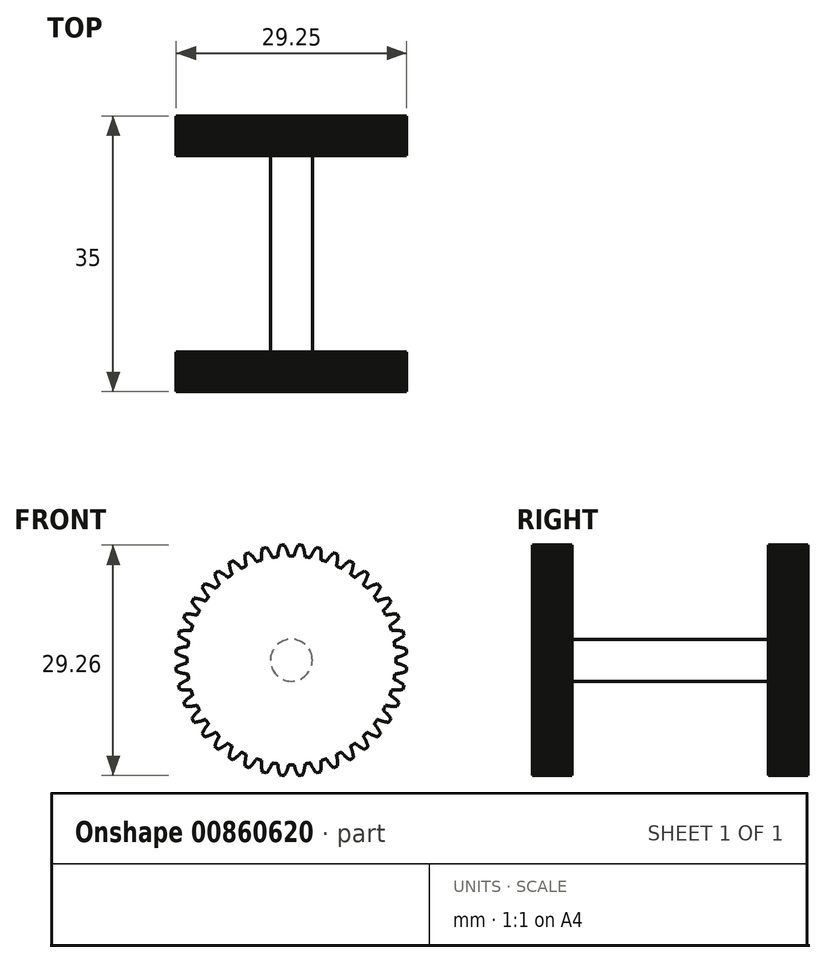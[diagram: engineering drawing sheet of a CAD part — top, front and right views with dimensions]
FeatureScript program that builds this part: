
annotation { "Feature Type Name" : "Feature", "Feature Type Description" : "" }
export const myFeature = defineFeature(function(context is Context, id is Id, definition is map)
    precondition{}
    {
        {
            var Q0;
            Q0=qCreatedBy(makeId("Front.planeOp"),FACE);
            var sketch = newSketch(context, id + "F0", { "sketchPlane" : qUnion([Q0])});
            skLineSegment(sketch, "E0", {"start": v(-13.67, 1.41) * mm, "end": v(-13.71, 1.13) * mm});
            skLineSegment(sketch, "E1", {"start": v(-13.71, 1.13) * mm, "end": v(-13.71, 0.85) * mm});
            skLineSegment(sketch, "E2", {"start": v(-13.71, 0.85) * mm, "end": v(-13.66, 0.82) * mm});
            skLineSegment(sketch, "E3", {"start": v(-13.66, 0.82) * mm, "end": v(-13.57, 0.77) * mm});
            skLineSegment(sketch, "E4", {"start": v(-13.57, 0.77) * mm, "end": v(-13.5, 0.73) * mm});
            skLineSegment(sketch, "E5", {"start": v(-13.5, 0.73) * mm, "end": v(-13.41, 0.7) * mm});
            skLineSegment(sketch, "E6", {"start": v(-13.41, 0.7) * mm, "end": v(-13.33, 0.65) * mm});
            skLineSegment(sketch, "E7", {"start": v(-13.33, 0.65) * mm, "end": v(-13.26, 0.62) * mm});
            skLineSegment(sketch, "E8", {"start": v(-13.26, 0.62) * mm, "end": v(-13.19, 0.59) * mm});
            skLineSegment(sketch, "E9", {"start": v(-13.19, 0.59) * mm, "end": v(-13.12, 0.56) * mm});
            skLineSegment(sketch, "E10", {"start": v(-13.12, 0.56) * mm, "end": v(-13.05, 0.53) * mm});
            skLineSegment(sketch, "E11", {"start": v(-13.05, 0.53) * mm, "end": v(-12.98, 0.5) * mm});
            skLineSegment(sketch, "E12", {"start": v(-12.98, 0.5) * mm, "end": v(-12.92, 0.49) * mm});
            skLineSegment(sketch, "E13", {"start": v(-12.92, 0.49) * mm, "end": v(-12.86, 0.47) * mm});
            skLineSegment(sketch, "E14", {"start": v(-12.86, 0.47) * mm, "end": v(-12.8, 0.45) * mm});
            skLineSegment(sketch, "E15", {"start": v(-12.8, 0.45) * mm, "end": v(-12.75, 0.43) * mm});
            skLineSegment(sketch, "E16", {"start": v(-12.75, 0.43) * mm, "end": v(-12.7, 0.42) * mm});
            skLineSegment(sketch, "E17", {"start": v(-12.7, 0.42) * mm, "end": v(-12.65, 0.4) * mm});
            skLineSegment(sketch, "E18", {"start": v(-12.65, 0.4) * mm, "end": v(-12.6, 0.4) * mm});
            skLineSegment(sketch, "E19", {"start": v(-12.6, 0.4) * mm, "end": v(-12.57, 0.38) * mm});
            skLineSegment(sketch, "E20", {"start": v(-12.57, 0.38) * mm, "end": v(-12.53, 0.37) * mm});
            skLineSegment(sketch, "E21", {"start": v(-12.53, 0.37) * mm, "end": v(-12.5, 0.37) * mm});
            skLineSegment(sketch, "E22", {"start": v(-12.5, 0.37) * mm, "end": v(-12.48, 0.36) * mm});
            skLineSegment(sketch, "E23", {"start": v(-12.48, 0.36) * mm, "end": v(-12.45, 0.35) * mm});
            skLineSegment(sketch, "E24", {"start": v(-12.45, 0.35) * mm, "end": v(-12.42, 0.34) * mm});
            skLineSegment(sketch, "E25", {"start": v(-12.42, 0.34) * mm, "end": v(-12.4, 0.33) * mm});
            skLineSegment(sketch, "E26", {"start": v(-12.4, 0.33) * mm, "end": v(-12.38, 0.32) * mm});
            skLineSegment(sketch, "E27", {"start": v(-12.38, 0.32) * mm, "end": v(-12.37, 0.31) * mm});
            skLineSegment(sketch, "E28", {"start": v(-12.37, 0.31) * mm, "end": v(-12.36, 0.3) * mm});
            skLineSegment(sketch, "E29", {"start": v(-12.36, 0.3) * mm, "end": v(-12.35, 0.3) * mm});
            skLineSegment(sketch, "E30", {"start": v(-12.35, 0.3) * mm, "end": v(-12.35, 0.28) * mm});
            skLineSegment(sketch, "E31", {"start": v(-12.35, 0.28) * mm, "end": v(-12.35, 0.08) * mm});
            skLineSegment(sketch, "E32", {"start": v(-12.35, 0.08) * mm, "end": v(-12.35, -0.12) * mm});
            skLineSegment(sketch, "E33", {"start": v(-12.35, -0.12) * mm, "end": v(-12.35, -0.32) * mm});
            skLineSegment(sketch, "E34", {"start": v(-12.35, -0.32) * mm, "end": v(-12.35, -0.33) * mm});
            skLineSegment(sketch, "E35", {"start": v(-12.35, -0.33) * mm, "end": v(-12.36, -0.34) * mm});
            skLineSegment(sketch, "E36", {"start": v(-12.36, -0.34) * mm, "end": v(-12.37, -0.35) * mm});
            skLineSegment(sketch, "E37", {"start": v(-12.37, -0.35) * mm, "end": v(-12.38, -0.36) * mm});
            skLineSegment(sketch, "E38", {"start": v(-12.38, -0.36) * mm, "end": v(-12.4, -0.37) * mm});
            skLineSegment(sketch, "E39", {"start": v(-12.4, -0.37) * mm, "end": v(-12.42, -0.38) * mm});
            skLineSegment(sketch, "E40", {"start": v(-12.42, -0.38) * mm, "end": v(-12.45, -0.4) * mm});
            skLineSegment(sketch, "E41", {"start": v(-12.45, -0.4) * mm, "end": v(-12.48, -0.4) * mm});
            skLineSegment(sketch, "E42", {"start": v(-12.48, -0.4) * mm, "end": v(-12.5, -0.4) * mm});
            skLineSegment(sketch, "E43", {"start": v(-12.5, -0.4) * mm, "end": v(-12.53, -0.41) * mm});
            skLineSegment(sketch, "E44", {"start": v(-12.53, -0.41) * mm, "end": v(-12.57, -0.42) * mm});
            skLineSegment(sketch, "E45", {"start": v(-12.57, -0.42) * mm, "end": v(-12.6, -0.43) * mm});
            skLineSegment(sketch, "E46", {"start": v(-12.6, -0.43) * mm, "end": v(-12.65, -0.44) * mm});
            skLineSegment(sketch, "E47", {"start": v(-12.65, -0.44) * mm, "end": v(-12.7, -0.46) * mm});
            skLineSegment(sketch, "E48", {"start": v(-12.7, -0.46) * mm, "end": v(-12.75, -0.47) * mm});
            skLineSegment(sketch, "E49", {"start": v(-12.75, -0.47) * mm, "end": v(-12.8, -0.49) * mm});
            skLineSegment(sketch, "E50", {"start": v(-12.8, -0.49) * mm, "end": v(-12.86, -0.5) * mm});
            skLineSegment(sketch, "E51", {"start": v(-12.86, -0.5) * mm, "end": v(-12.92, -0.53) * mm});
            skLineSegment(sketch, "E52", {"start": v(-12.92, -0.53) * mm, "end": v(-12.98, -0.55) * mm});
            skLineSegment(sketch, "E53", {"start": v(-12.98, -0.55) * mm, "end": v(-13.05, -0.57) * mm});
            skLineSegment(sketch, "E54", {"start": v(-13.05, -0.57) * mm, "end": v(-13.12, -0.6) * mm});
            skLineSegment(sketch, "E55", {"start": v(-13.12, -0.6) * mm, "end": v(-13.19, -0.63) * mm});
            skLineSegment(sketch, "E56", {"start": v(-13.19, -0.63) * mm, "end": v(-13.26, -0.66) * mm});
            skLineSegment(sketch, "E57", {"start": v(-13.26, -0.66) * mm, "end": v(-13.33, -0.7) * mm});
            skLineSegment(sketch, "E58", {"start": v(-13.33, -0.7) * mm, "end": v(-13.41, -0.73) * mm});
            skLineSegment(sketch, "E59", {"start": v(-13.41, -0.73) * mm, "end": v(-13.5, -0.77) * mm});
            skLineSegment(sketch, "E60", {"start": v(-13.5, -0.77) * mm, "end": v(-13.57, -0.81) * mm});
            skLineSegment(sketch, "E61", {"start": v(-13.57, -0.81) * mm, "end": v(-13.66, -0.86) * mm});
            skLineSegment(sketch, "E62", {"start": v(-13.66, -0.86) * mm, "end": v(-13.71, -0.89) * mm});
            skLineSegment(sketch, "E63", {"start": v(-13.71, -0.89) * mm, "end": v(-13.71, -1.17) * mm});
            skLineSegment(sketch, "E64", {"start": v(-13.71, -1.17) * mm, "end": v(-13.67, -1.45) * mm});
            skLineSegment(sketch, "E65", {"start": v(-13.67, -1.45) * mm, "end": v(-13.6, -1.47) * mm});
            skLineSegment(sketch, "E66", {"start": v(-13.6, -1.47) * mm, "end": v(-13.52, -1.5) * mm});
            skLineSegment(sketch, "E67", {"start": v(-13.52, -1.5) * mm, "end": v(-13.43, -1.53) * mm});
            skLineSegment(sketch, "E68", {"start": v(-13.43, -1.53) * mm, "end": v(-13.35, -1.56) * mm});
            skLineSegment(sketch, "E69", {"start": v(-13.35, -1.56) * mm, "end": v(-13.26, -1.58) * mm});
            skLineSegment(sketch, "E70", {"start": v(-13.26, -1.58) * mm, "end": v(-13.18, -1.6) * mm});
            skLineSegment(sketch, "E71", {"start": v(-13.18, -1.6) * mm, "end": v(-13.1, -1.62) * mm});
            skLineSegment(sketch, "E72", {"start": v(-13.1, -1.62) * mm, "end": v(-13.03, -1.64) * mm});
            skLineSegment(sketch, "E73", {"start": v(-13.03, -1.64) * mm, "end": v(-12.96, -1.66) * mm});
            skLineSegment(sketch, "E74", {"start": v(-12.96, -1.66) * mm, "end": v(-12.9, -1.67) * mm});
            skLineSegment(sketch, "E75", {"start": v(-12.9, -1.67) * mm, "end": v(-12.83, -1.68) * mm});
            skLineSegment(sketch, "E76", {"start": v(-12.83, -1.68) * mm, "end": v(-12.77, -1.7) * mm});
            skLineSegment(sketch, "E77", {"start": v(-12.77, -1.7) * mm, "end": v(-12.7, -1.7) * mm});
            skLineSegment(sketch, "E78", {"start": v(-12.7, -1.7) * mm, "end": v(-12.65, -1.71) * mm});
            skLineSegment(sketch, "E79", {"start": v(-12.65, -1.71) * mm, "end": v(-12.6, -1.72) * mm});
            skLineSegment(sketch, "E80", {"start": v(-12.6, -1.72) * mm, "end": v(-12.55, -1.72) * mm});
            skLineSegment(sketch, "E81", {"start": v(-12.55, -1.72) * mm, "end": v(-12.5, -1.73) * mm});
            skLineSegment(sketch, "E82", {"start": v(-12.5, -1.73) * mm, "end": v(-12.46, -1.73) * mm});
            skLineSegment(sketch, "E83", {"start": v(-12.46, -1.73) * mm, "end": v(-12.42, -1.73) * mm});
            skLineSegment(sketch, "E84", {"start": v(-12.42, -1.73) * mm, "end": v(-12.4, -1.74) * mm});
            skLineSegment(sketch, "E85", {"start": v(-12.4, -1.74) * mm, "end": v(-12.37, -1.74) * mm});
            skLineSegment(sketch, "E86", {"start": v(-12.37, -1.74) * mm, "end": v(-12.34, -1.74) * mm});
            skLineSegment(sketch, "E87", {"start": v(-12.34, -1.74) * mm, "end": v(-12.32, -1.75) * mm});
            skLineSegment(sketch, "E88", {"start": v(-12.32, -1.75) * mm, "end": v(-12.3, -1.75) * mm});
            skLineSegment(sketch, "E89", {"start": v(-12.3, -1.75) * mm, "end": v(-12.27, -1.76) * mm});
            skLineSegment(sketch, "E90", {"start": v(-12.27, -1.76) * mm, "end": v(-12.26, -1.77) * mm});
            skLineSegment(sketch, "E91", {"start": v(-12.26, -1.77) * mm, "end": v(-12.25, -1.78) * mm});
            skLineSegment(sketch, "E92", {"start": v(-12.25, -1.78) * mm, "end": v(-12.24, -1.79) * mm});
            skLineSegment(sketch, "E93", {"start": v(-12.24, -1.79) * mm, "end": v(-12.23, -1.8) * mm});
            skLineSegment(sketch, "E94", {"start": v(-12.23, -1.8) * mm, "end": v(-12.2, -2) * mm});
            skLineSegment(sketch, "E95", {"start": v(-12.2, -2) * mm, "end": v(-12.17, -2.2) * mm});
            skLineSegment(sketch, "E96", {"start": v(-12.17, -2.2) * mm, "end": v(-12.14, -2.4) * mm});
            skLineSegment(sketch, "E97", {"start": v(-12.14, -2.4) * mm, "end": v(-12.14, -2.4) * mm});
            skLineSegment(sketch, "E98", {"start": v(-12.14, -2.4) * mm, "end": v(-12.15, -2.41) * mm});
            skLineSegment(sketch, "E99", {"start": v(-12.15, -2.41) * mm, "end": v(-12.15, -2.43) * mm});
            skLineSegment(sketch, "E100", {"start": v(-12.15, -2.43) * mm, "end": v(-12.17, -2.44) * mm});
            skLineSegment(sketch, "E101", {"start": v(-12.17, -2.44) * mm, "end": v(-12.18, -2.45) * mm});
            skLineSegment(sketch, "E102", {"start": v(-12.18, -2.45) * mm, "end": v(-12.2, -2.47) * mm});
            skLineSegment(sketch, "E103", {"start": v(-12.2, -2.47) * mm, "end": v(-12.22, -2.48) * mm});
            skLineSegment(sketch, "E104", {"start": v(-12.22, -2.48) * mm, "end": v(-12.25, -2.5) * mm});
            skLineSegment(sketch, "E105", {"start": v(-12.25, -2.5) * mm, "end": v(-12.28, -2.5) * mm});
            skLineSegment(sketch, "E106", {"start": v(-12.28, -2.5) * mm, "end": v(-12.3, -2.5) * mm});
            skLineSegment(sketch, "E107", {"start": v(-12.3, -2.5) * mm, "end": v(-12.34, -2.52) * mm});
            skLineSegment(sketch, "E108", {"start": v(-12.34, -2.52) * mm, "end": v(-12.38, -2.54) * mm});
            skLineSegment(sketch, "E109", {"start": v(-12.38, -2.54) * mm, "end": v(-12.42, -2.56) * mm});
            skLineSegment(sketch, "E110", {"start": v(-12.42, -2.56) * mm, "end": v(-12.46, -2.58) * mm});
            skLineSegment(sketch, "E111", {"start": v(-12.46, -2.58) * mm, "end": v(-12.51, -2.6) * mm});
            skLineSegment(sketch, "E112", {"start": v(-12.51, -2.6) * mm, "end": v(-12.56, -2.63) * mm});
            skLineSegment(sketch, "E113", {"start": v(-12.56, -2.63) * mm, "end": v(-12.62, -2.65) * mm});
            skLineSegment(sketch, "E114", {"start": v(-12.62, -2.65) * mm, "end": v(-12.67, -2.68) * mm});
            skLineSegment(sketch, "E115", {"start": v(-12.67, -2.68) * mm, "end": v(-12.73, -2.72) * mm});
            skLineSegment(sketch, "E116", {"start": v(-12.73, -2.72) * mm, "end": v(-12.79, -2.75) * mm});
            skLineSegment(sketch, "E117", {"start": v(-12.79, -2.75) * mm, "end": v(-12.85, -2.79) * mm});
            skLineSegment(sketch, "E118", {"start": v(-12.85, -2.79) * mm, "end": v(-12.92, -2.83) * mm});
            skLineSegment(sketch, "E119", {"start": v(-12.92, -2.83) * mm, "end": v(-12.98, -2.87) * mm});
            skLineSegment(sketch, "E120", {"start": v(-12.98, -2.87) * mm, "end": v(-13.05, -2.91) * mm});
            skLineSegment(sketch, "E121", {"start": v(-13.05, -2.91) * mm, "end": v(-13.12, -2.96) * mm});
            skLineSegment(sketch, "E122", {"start": v(-13.12, -2.96) * mm, "end": v(-13.2, -3.01) * mm});
            skLineSegment(sketch, "E123", {"start": v(-13.2, -3.01) * mm, "end": v(-13.27, -3.07) * mm});
            skLineSegment(sketch, "E124", {"start": v(-13.27, -3.07) * mm, "end": v(-13.35, -3.12) * mm});
            skLineSegment(sketch, "E125", {"start": v(-13.35, -3.12) * mm, "end": v(-13.4, -3.16) * mm});
            skLineSegment(sketch, "E126", {"start": v(-13.4, -3.16) * mm, "end": v(-13.35, -3.45) * mm});
            skLineSegment(sketch, "E127", {"start": v(-13.35, -3.45) * mm, "end": v(-13.27, -3.72) * mm});
            skLineSegment(sketch, "E128", {"start": v(-13.27, -3.72) * mm, "end": v(-13.2, -3.73) * mm});
            skLineSegment(sketch, "E129", {"start": v(-13.2, -3.73) * mm, "end": v(-13.1, -3.74) * mm});
            skLineSegment(sketch, "E130", {"start": v(-13.1, -3.74) * mm, "end": v(-13.02, -3.76) * mm});
            skLineSegment(sketch, "E131", {"start": v(-13.02, -3.76) * mm, "end": v(-12.93, -3.77) * mm});
            skLineSegment(sketch, "E132", {"start": v(-12.93, -3.77) * mm, "end": v(-12.84, -3.78) * mm});
            skLineSegment(sketch, "E133", {"start": v(-12.84, -3.78) * mm, "end": v(-12.76, -3.8) * mm});
            skLineSegment(sketch, "E134", {"start": v(-12.76, -3.8) * mm, "end": v(-12.68, -3.8) * mm});
            skLineSegment(sketch, "E135", {"start": v(-12.68, -3.8) * mm, "end": v(-12.6, -3.8) * mm});
            skLineSegment(sketch, "E136", {"start": v(-12.6, -3.8) * mm, "end": v(-12.54, -3.8) * mm});
            skLineSegment(sketch, "E137", {"start": v(-12.54, -3.8) * mm, "end": v(-12.47, -3.81) * mm});
            skLineSegment(sketch, "E138", {"start": v(-12.47, -3.81) * mm, "end": v(-12.4, -3.81) * mm});
            skLineSegment(sketch, "E139", {"start": v(-12.4, -3.81) * mm, "end": v(-12.34, -3.81) * mm});
            skLineSegment(sketch, "E140", {"start": v(-12.34, -3.81) * mm, "end": v(-12.28, -3.81) * mm});
            skLineSegment(sketch, "E141", {"start": v(-12.28, -3.81) * mm, "end": v(-12.22, -3.81) * mm});
            skLineSegment(sketch, "E142", {"start": v(-12.22, -3.81) * mm, "end": v(-12.17, -3.81) * mm});
            skLineSegment(sketch, "E143", {"start": v(-12.17, -3.81) * mm, "end": v(-12.12, -3.8) * mm});
            skLineSegment(sketch, "E144", {"start": v(-12.12, -3.8) * mm, "end": v(-12.07, -3.8) * mm});
            skLineSegment(sketch, "E145", {"start": v(-12.07, -3.8) * mm, "end": v(-12.03, -3.8) * mm});
            skLineSegment(sketch, "E146", {"start": v(-12.03, -3.8) * mm, "end": v(-11.99, -3.8) * mm});
            skLineSegment(sketch, "E147", {"start": v(-11.99, -3.8) * mm, "end": v(-11.97, -3.8) * mm});
            skLineSegment(sketch, "E148", {"start": v(-11.97, -3.8) * mm, "end": v(-11.94, -3.8) * mm});
            skLineSegment(sketch, "E149", {"start": v(-11.94, -3.8) * mm, "end": v(-11.9, -3.8) * mm});
            skLineSegment(sketch, "E150", {"start": v(-11.9, -3.8) * mm, "end": v(-11.88, -3.8) * mm});
            skLineSegment(sketch, "E151", {"start": v(-11.88, -3.8) * mm, "end": v(-11.86, -3.8) * mm});
            skLineSegment(sketch, "E152", {"start": v(-11.86, -3.8) * mm, "end": v(-11.84, -3.8) * mm});
            skLineSegment(sketch, "E153", {"start": v(-11.84, -3.8) * mm, "end": v(-11.82, -3.8) * mm});
            skLineSegment(sketch, "E154", {"start": v(-11.82, -3.8) * mm, "end": v(-11.8, -3.81) * mm});
            skLineSegment(sketch, "E155", {"start": v(-11.8, -3.81) * mm, "end": v(-11.8, -3.82) * mm});
            skLineSegment(sketch, "E156", {"start": v(-11.8, -3.82) * mm, "end": v(-11.8, -3.83) * mm});
            skLineSegment(sketch, "E157", {"start": v(-11.8, -3.83) * mm, "end": v(-11.74, -4.02) * mm});
            skLineSegment(sketch, "E158", {"start": v(-11.74, -4.02) * mm, "end": v(-11.67, -4.22) * mm});
            skLineSegment(sketch, "E159", {"start": v(-11.67, -4.22) * mm, "end": v(-11.6, -4.4) * mm});
            skLineSegment(sketch, "E160", {"start": v(-11.6, -4.4) * mm, "end": v(-11.6, -4.42) * mm});
            skLineSegment(sketch, "E161", {"start": v(-11.6, -4.42) * mm, "end": v(-11.61, -4.43) * mm});
            skLineSegment(sketch, "E162", {"start": v(-11.61, -4.43) * mm, "end": v(-11.62, -4.44) * mm});
            skLineSegment(sketch, "E163", {"start": v(-11.62, -4.44) * mm, "end": v(-11.63, -4.46) * mm});
            skLineSegment(sketch, "E164", {"start": v(-11.63, -4.46) * mm, "end": v(-11.64, -4.47) * mm});
            skLineSegment(sketch, "E165", {"start": v(-11.64, -4.47) * mm, "end": v(-11.66, -4.49) * mm});
            skLineSegment(sketch, "E166", {"start": v(-11.66, -4.49) * mm, "end": v(-11.68, -4.5) * mm});
            skLineSegment(sketch, "E167", {"start": v(-11.68, -4.5) * mm, "end": v(-11.7, -4.52) * mm});
            skLineSegment(sketch, "E168", {"start": v(-11.7, -4.52) * mm, "end": v(-11.73, -4.54) * mm});
            skLineSegment(sketch, "E169", {"start": v(-11.73, -4.54) * mm, "end": v(-11.75, -4.55) * mm});
            skLineSegment(sketch, "E170", {"start": v(-11.75, -4.55) * mm, "end": v(-11.78, -4.57) * mm});
            skLineSegment(sketch, "E171", {"start": v(-11.78, -4.57) * mm, "end": v(-11.82, -4.59) * mm});
            skLineSegment(sketch, "E172", {"start": v(-11.82, -4.59) * mm, "end": v(-11.86, -4.61) * mm});
            skLineSegment(sketch, "E173", {"start": v(-11.86, -4.61) * mm, "end": v(-11.9, -4.64) * mm});
            skLineSegment(sketch, "E174", {"start": v(-11.9, -4.64) * mm, "end": v(-11.94, -4.67) * mm});
            skLineSegment(sketch, "E175", {"start": v(-11.94, -4.67) * mm, "end": v(-11.99, -4.7) * mm});
            skLineSegment(sketch, "E176", {"start": v(-11.99, -4.7) * mm, "end": v(-12.04, -4.74) * mm});
            skLineSegment(sketch, "E177", {"start": v(-12.04, -4.74) * mm, "end": v(-12.09, -4.78) * mm});
            skLineSegment(sketch, "E178", {"start": v(-12.09, -4.78) * mm, "end": v(-12.14, -4.82) * mm});
            skLineSegment(sketch, "E179", {"start": v(-12.14, -4.82) * mm, "end": v(-12.2, -4.86) * mm});
            skLineSegment(sketch, "E180", {"start": v(-12.2, -4.86) * mm, "end": v(-12.25, -4.9) * mm});
            skLineSegment(sketch, "E181", {"start": v(-12.25, -4.9) * mm, "end": v(-12.3, -4.96) * mm});
            skLineSegment(sketch, "E182", {"start": v(-12.3, -4.96) * mm, "end": v(-12.37, -5) * mm});
            skLineSegment(sketch, "E183", {"start": v(-12.37, -5) * mm, "end": v(-12.43, -5.06) * mm});
            skLineSegment(sketch, "E184", {"start": v(-12.43, -5.06) * mm, "end": v(-12.5, -5.12) * mm});
            skLineSegment(sketch, "E185", {"start": v(-12.5, -5.12) * mm, "end": v(-12.55, -5.18) * mm});
            skLineSegment(sketch, "E186", {"start": v(-12.55, -5.18) * mm, "end": v(-12.62, -5.25) * mm});
            skLineSegment(sketch, "E187", {"start": v(-12.62, -5.25) * mm, "end": v(-12.69, -5.32) * mm});
            skLineSegment(sketch, "E188", {"start": v(-12.69, -5.32) * mm, "end": v(-12.73, -5.36) * mm});
            skLineSegment(sketch, "E189", {"start": v(-12.73, -5.36) * mm, "end": v(-12.64, -5.63) * mm});
            skLineSegment(sketch, "E190", {"start": v(-12.64, -5.63) * mm, "end": v(-12.51, -5.89) * mm});
            skLineSegment(sketch, "E191", {"start": v(-12.51, -5.89) * mm, "end": v(-12.45, -5.9) * mm});
            skLineSegment(sketch, "E192", {"start": v(-12.45, -5.9) * mm, "end": v(-12.35, -5.9) * mm});
            skLineSegment(sketch, "E193", {"start": v(-12.35, -5.9) * mm, "end": v(-12.26, -5.9) * mm});
            skLineSegment(sketch, "E194", {"start": v(-12.26, -5.9) * mm, "end": v(-12.17, -5.9) * mm});
            skLineSegment(sketch, "E195", {"start": v(-12.17, -5.9) * mm, "end": v(-12.09, -5.89) * mm});
            skLineSegment(sketch, "E196", {"start": v(-12.09, -5.89) * mm, "end": v(-12, -5.88) * mm});
            skLineSegment(sketch, "E197", {"start": v(-12, -5.88) * mm, "end": v(-11.93, -5.88) * mm});
            skLineSegment(sketch, "E198", {"start": v(-11.93, -5.88) * mm, "end": v(-11.85, -5.87) * mm});
            skLineSegment(sketch, "E199", {"start": v(-11.85, -5.87) * mm, "end": v(-11.78, -5.87) * mm});
            skLineSegment(sketch, "E200", {"start": v(-11.78, -5.87) * mm, "end": v(-11.7, -5.86) * mm});
            skLineSegment(sketch, "E201", {"start": v(-11.7, -5.86) * mm, "end": v(-11.64, -5.85) * mm});
            skLineSegment(sketch, "E202", {"start": v(-11.64, -5.85) * mm, "end": v(-11.58, -5.84) * mm});
            skLineSegment(sketch, "E203", {"start": v(-11.58, -5.84) * mm, "end": v(-11.52, -5.83) * mm});
            skLineSegment(sketch, "E204", {"start": v(-11.52, -5.83) * mm, "end": v(-11.47, -5.82) * mm});
            skLineSegment(sketch, "E205", {"start": v(-11.47, -5.82) * mm, "end": v(-11.41, -5.81) * mm});
            skLineSegment(sketch, "E206", {"start": v(-11.41, -5.81) * mm, "end": v(-11.37, -5.8) * mm});
            skLineSegment(sketch, "E207", {"start": v(-11.37, -5.8) * mm, "end": v(-11.32, -5.8) * mm});
            skLineSegment(sketch, "E208", {"start": v(-11.32, -5.8) * mm, "end": v(-11.28, -5.78) * mm});
            skLineSegment(sketch, "E209", {"start": v(-11.28, -5.78) * mm, "end": v(-11.24, -5.77) * mm});
            skLineSegment(sketch, "E210", {"start": v(-11.24, -5.77) * mm, "end": v(-11.22, -5.77) * mm});
            skLineSegment(sketch, "E211", {"start": v(-11.22, -5.77) * mm, "end": v(-11.19, -5.76) * mm});
            skLineSegment(sketch, "E212", {"start": v(-11.19, -5.76) * mm, "end": v(-11.16, -5.75) * mm});
            skLineSegment(sketch, "E213", {"start": v(-11.16, -5.75) * mm, "end": v(-11.13, -5.75) * mm});
            skLineSegment(sketch, "E214", {"start": v(-11.13, -5.75) * mm, "end": v(-11.11, -5.75) * mm});
            skLineSegment(sketch, "E215", {"start": v(-11.11, -5.75) * mm, "end": v(-11.1, -5.75) * mm});
            skLineSegment(sketch, "E216", {"start": v(-11.1, -5.75) * mm, "end": v(-11.07, -5.75) * mm});
            skLineSegment(sketch, "E217", {"start": v(-11.07, -5.75) * mm, "end": v(-11.06, -5.76) * mm});
            skLineSegment(sketch, "E218", {"start": v(-11.06, -5.76) * mm, "end": v(-11.05, -5.77) * mm});
            skLineSegment(sketch, "E219", {"start": v(-11.05, -5.77) * mm, "end": v(-11.04, -5.77) * mm});
            skLineSegment(sketch, "E220", {"start": v(-11.04, -5.77) * mm, "end": v(-10.95, -5.95) * mm});
            skLineSegment(sketch, "E221", {"start": v(-10.95, -5.95) * mm, "end": v(-10.86, -6.14) * mm});
            skLineSegment(sketch, "E222", {"start": v(-10.86, -6.14) * mm, "end": v(-10.77, -6.3) * mm});
            skLineSegment(sketch, "E223", {"start": v(-10.77, -6.3) * mm, "end": v(-10.77, -6.32) * mm});
            skLineSegment(sketch, "E224", {"start": v(-10.77, -6.32) * mm, "end": v(-10.77, -6.33) * mm});
            skLineSegment(sketch, "E225", {"start": v(-10.77, -6.33) * mm, "end": v(-10.77, -6.35) * mm});
            skLineSegment(sketch, "E226", {"start": v(-10.77, -6.35) * mm, "end": v(-10.78, -6.36) * mm});
            skLineSegment(sketch, "E227", {"start": v(-10.78, -6.36) * mm, "end": v(-10.79, -6.38) * mm});
            skLineSegment(sketch, "E228", {"start": v(-10.79, -6.38) * mm, "end": v(-10.8, -6.4) * mm});
            skLineSegment(sketch, "E229", {"start": v(-10.8, -6.4) * mm, "end": v(-10.82, -6.42) * mm});
            skLineSegment(sketch, "E230", {"start": v(-10.82, -6.42) * mm, "end": v(-10.84, -6.44) * mm});
            skLineSegment(sketch, "E231", {"start": v(-10.84, -6.44) * mm, "end": v(-10.87, -6.46) * mm});
            skLineSegment(sketch, "E232", {"start": v(-10.87, -6.46) * mm, "end": v(-10.88, -6.47) * mm});
            skLineSegment(sketch, "E233", {"start": v(-10.88, -6.47) * mm, "end": v(-10.91, -6.5) * mm});
            skLineSegment(sketch, "E234", {"start": v(-10.91, -6.5) * mm, "end": v(-10.95, -6.52) * mm});
            skLineSegment(sketch, "E235", {"start": v(-10.95, -6.52) * mm, "end": v(-10.98, -6.56) * mm});
            skLineSegment(sketch, "E236", {"start": v(-10.98, -6.56) * mm, "end": v(-11.02, -6.59) * mm});
            skLineSegment(sketch, "E237", {"start": v(-11.02, -6.59) * mm, "end": v(-11.06, -6.63) * mm});
            skLineSegment(sketch, "E238", {"start": v(-11.06, -6.63) * mm, "end": v(-11.1, -6.66) * mm});
            skLineSegment(sketch, "E239", {"start": v(-11.1, -6.66) * mm, "end": v(-11.14, -6.7) * mm});
            skLineSegment(sketch, "E240", {"start": v(-11.14, -6.7) * mm, "end": v(-11.18, -6.75) * mm});
            skLineSegment(sketch, "E241", {"start": v(-11.18, -6.75) * mm, "end": v(-11.23, -6.8) * mm});
            skLineSegment(sketch, "E242", {"start": v(-11.23, -6.8) * mm, "end": v(-11.28, -6.85) * mm});
            skLineSegment(sketch, "E243", {"start": v(-11.28, -6.85) * mm, "end": v(-11.32, -6.9) * mm});
            skLineSegment(sketch, "E244", {"start": v(-11.32, -6.9) * mm, "end": v(-11.37, -6.96) * mm});
            skLineSegment(sketch, "E245", {"start": v(-11.37, -6.96) * mm, "end": v(-11.42, -7.02) * mm});
            skLineSegment(sketch, "E246", {"start": v(-11.42, -7.02) * mm, "end": v(-11.47, -7.09) * mm});
            skLineSegment(sketch, "E247", {"start": v(-11.47, -7.09) * mm, "end": v(-11.53, -7.16) * mm});
            skLineSegment(sketch, "E248", {"start": v(-11.53, -7.16) * mm, "end": v(-11.58, -7.23) * mm});
            skLineSegment(sketch, "E249", {"start": v(-11.58, -7.23) * mm, "end": v(-11.63, -7.3) * mm});
            skLineSegment(sketch, "E250", {"start": v(-11.63, -7.3) * mm, "end": v(-11.69, -7.38) * mm});
            skLineSegment(sketch, "E251", {"start": v(-11.69, -7.38) * mm, "end": v(-11.73, -7.43) * mm});
            skLineSegment(sketch, "E252", {"start": v(-11.73, -7.43) * mm, "end": v(-11.6, -7.69) * mm});
            skLineSegment(sketch, "E253", {"start": v(-11.6, -7.69) * mm, "end": v(-11.43, -7.92) * mm});
            skLineSegment(sketch, "E254", {"start": v(-11.43, -7.92) * mm, "end": v(-11.37, -7.9) * mm});
            skLineSegment(sketch, "E255", {"start": v(-11.37, -7.9) * mm, "end": v(-11.27, -7.9) * mm});
            skLineSegment(sketch, "E256", {"start": v(-11.27, -7.9) * mm, "end": v(-11.18, -7.88) * mm});
            skLineSegment(sketch, "E257", {"start": v(-11.18, -7.88) * mm, "end": v(-11.1, -7.87) * mm});
            skLineSegment(sketch, "E258", {"start": v(-11.1, -7.87) * mm, "end": v(-11, -7.85) * mm});
            skLineSegment(sketch, "E259", {"start": v(-11, -7.85) * mm, "end": v(-10.93, -7.83) * mm});
            skLineSegment(sketch, "E260", {"start": v(-10.93, -7.83) * mm, "end": v(-10.85, -7.82) * mm});
            skLineSegment(sketch, "E261", {"start": v(-10.85, -7.82) * mm, "end": v(-10.78, -7.8) * mm});
            skLineSegment(sketch, "E262", {"start": v(-10.78, -7.8) * mm, "end": v(-10.7, -7.78) * mm});
            skLineSegment(sketch, "E263", {"start": v(-10.7, -7.78) * mm, "end": v(-10.64, -7.76) * mm});
            skLineSegment(sketch, "E264", {"start": v(-10.64, -7.76) * mm, "end": v(-10.58, -7.74) * mm});
            skLineSegment(sketch, "E265", {"start": v(-10.58, -7.74) * mm, "end": v(-10.52, -7.72) * mm});
            skLineSegment(sketch, "E266", {"start": v(-10.52, -7.72) * mm, "end": v(-10.46, -7.7) * mm});
            skLineSegment(sketch, "E267", {"start": v(-10.46, -7.7) * mm, "end": v(-10.4, -7.69) * mm});
            skLineSegment(sketch, "E268", {"start": v(-10.4, -7.69) * mm, "end": v(-10.36, -7.67) * mm});
            skLineSegment(sketch, "E269", {"start": v(-10.36, -7.67) * mm, "end": v(-10.31, -7.65) * mm});
            skLineSegment(sketch, "E270", {"start": v(-10.31, -7.65) * mm, "end": v(-10.27, -7.63) * mm});
            skLineSegment(sketch, "E271", {"start": v(-10.27, -7.63) * mm, "end": v(-10.23, -7.62) * mm});
            skLineSegment(sketch, "E272", {"start": v(-10.23, -7.62) * mm, "end": v(-10.2, -7.6) * mm});
            skLineSegment(sketch, "E273", {"start": v(-10.2, -7.6) * mm, "end": v(-10.17, -7.6) * mm});
            skLineSegment(sketch, "E274", {"start": v(-10.17, -7.6) * mm, "end": v(-10.14, -7.58) * mm});
            skLineSegment(sketch, "E275", {"start": v(-10.14, -7.58) * mm, "end": v(-10.11, -7.57) * mm});
            skLineSegment(sketch, "E276", {"start": v(-10.11, -7.57) * mm, "end": v(-10.09, -7.56) * mm});
            skLineSegment(sketch, "E277", {"start": v(-10.09, -7.56) * mm, "end": v(-10.07, -7.56) * mm});
            skLineSegment(sketch, "E278", {"start": v(-10.07, -7.56) * mm, "end": v(-10.05, -7.56) * mm});
            skLineSegment(sketch, "E279", {"start": v(-10.05, -7.56) * mm, "end": v(-10.03, -7.56) * mm});
            skLineSegment(sketch, "E280", {"start": v(-10.03, -7.56) * mm, "end": v(-10.01, -7.56) * mm});
            skLineSegment(sketch, "E281", {"start": v(-10.01, -7.56) * mm, "end": v(-10, -7.57) * mm});
            skLineSegment(sketch, "E282", {"start": v(-10, -7.57) * mm, "end": v(-10, -7.57) * mm});
            skLineSegment(sketch, "E283", {"start": v(-10, -7.57) * mm, "end": v(-9.88, -7.73) * mm});
            skLineSegment(sketch, "E284", {"start": v(-9.88, -7.73) * mm, "end": v(-9.76, -7.9) * mm});
            skLineSegment(sketch, "E285", {"start": v(-9.76, -7.9) * mm, "end": v(-9.64, -8.06) * mm});
            skLineSegment(sketch, "E286", {"start": v(-9.64, -8.06) * mm, "end": v(-9.64, -8.07) * mm});
            skLineSegment(sketch, "E287", {"start": v(-9.64, -8.07) * mm, "end": v(-9.63, -8.08) * mm});
            skLineSegment(sketch, "E288", {"start": v(-9.63, -8.08) * mm, "end": v(-9.64, -8.1) * mm});
            skLineSegment(sketch, "E289", {"start": v(-9.64, -8.1) * mm, "end": v(-9.64, -8.11) * mm});
            skLineSegment(sketch, "E290", {"start": v(-9.64, -8.11) * mm, "end": v(-9.65, -8.13) * mm});
            skLineSegment(sketch, "E291", {"start": v(-9.65, -8.13) * mm, "end": v(-9.66, -8.15) * mm});
            skLineSegment(sketch, "E292", {"start": v(-9.66, -8.15) * mm, "end": v(-9.68, -8.17) * mm});
            skLineSegment(sketch, "E293", {"start": v(-9.68, -8.17) * mm, "end": v(-9.7, -8.2) * mm});
            skLineSegment(sketch, "E294", {"start": v(-9.7, -8.2) * mm, "end": v(-9.72, -8.22) * mm});
            skLineSegment(sketch, "E295", {"start": v(-9.72, -8.22) * mm, "end": v(-9.73, -8.24) * mm});
            skLineSegment(sketch, "E296", {"start": v(-9.73, -8.24) * mm, "end": v(-9.76, -8.27) * mm});
            skLineSegment(sketch, "E297", {"start": v(-9.76, -8.27) * mm, "end": v(-9.78, -8.3) * mm});
            skLineSegment(sketch, "E298", {"start": v(-9.78, -8.3) * mm, "end": v(-9.81, -8.34) * mm});
            skLineSegment(sketch, "E299", {"start": v(-9.81, -8.34) * mm, "end": v(-9.84, -8.37) * mm});
            skLineSegment(sketch, "E300", {"start": v(-9.84, -8.37) * mm, "end": v(-9.88, -8.42) * mm});
            skLineSegment(sketch, "E301", {"start": v(-9.88, -8.42) * mm, "end": v(-9.91, -8.46) * mm});
            skLineSegment(sketch, "E302", {"start": v(-9.91, -8.46) * mm, "end": v(-9.95, -8.5) * mm});
            skLineSegment(sketch, "E303", {"start": v(-9.95, -8.5) * mm, "end": v(-9.98, -8.56) * mm});
            skLineSegment(sketch, "E304", {"start": v(-9.98, -8.56) * mm, "end": v(-10.02, -8.62) * mm});
            skLineSegment(sketch, "E305", {"start": v(-10.02, -8.62) * mm, "end": v(-10.06, -8.67) * mm});
            skLineSegment(sketch, "E306", {"start": v(-10.06, -8.67) * mm, "end": v(-10.1, -8.74) * mm});
            skLineSegment(sketch, "E307", {"start": v(-10.1, -8.74) * mm, "end": v(-10.14, -8.8) * mm});
            skLineSegment(sketch, "E308", {"start": v(-10.14, -8.8) * mm, "end": v(-10.18, -8.87) * mm});
            skLineSegment(sketch, "E309", {"start": v(-10.18, -8.87) * mm, "end": v(-10.22, -8.94) * mm});
            skLineSegment(sketch, "E310", {"start": v(-10.22, -8.94) * mm, "end": v(-10.26, -9.01) * mm});
            skLineSegment(sketch, "E311", {"start": v(-10.26, -9.01) * mm, "end": v(-10.3, -9.1) * mm});
            skLineSegment(sketch, "E312", {"start": v(-10.3, -9.1) * mm, "end": v(-10.34, -9.18) * mm});
            skLineSegment(sketch, "E313", {"start": v(-10.34, -9.18) * mm, "end": v(-10.38, -9.26) * mm});
            skLineSegment(sketch, "E314", {"start": v(-10.38, -9.26) * mm, "end": v(-10.41, -9.32) * mm});
            skLineSegment(sketch, "E315", {"start": v(-10.41, -9.32) * mm, "end": v(-10.24, -9.55) * mm});
            skLineSegment(sketch, "E316", {"start": v(-10.24, -9.55) * mm, "end": v(-10.04, -9.75) * mm});
            skLineSegment(sketch, "E317", {"start": v(-10.04, -9.75) * mm, "end": v(-9.98, -9.73) * mm});
            skLineSegment(sketch, "E318", {"start": v(-9.98, -9.73) * mm, "end": v(-9.89, -9.7) * mm});
            skLineSegment(sketch, "E319", {"start": v(-9.89, -9.7) * mm, "end": v(-9.8, -9.68) * mm});
            skLineSegment(sketch, "E320", {"start": v(-9.8, -9.68) * mm, "end": v(-9.72, -9.65) * mm});
            skLineSegment(sketch, "E321", {"start": v(-9.72, -9.65) * mm, "end": v(-9.64, -9.62) * mm});
            skLineSegment(sketch, "E322", {"start": v(-9.64, -9.62) * mm, "end": v(-9.56, -9.59) * mm});
            skLineSegment(sketch, "E323", {"start": v(-9.56, -9.59) * mm, "end": v(-9.49, -9.56) * mm});
            skLineSegment(sketch, "E324", {"start": v(-9.49, -9.56) * mm, "end": v(-9.42, -9.53) * mm});
            skLineSegment(sketch, "E325", {"start": v(-9.42, -9.53) * mm, "end": v(-9.35, -9.5) * mm});
            skLineSegment(sketch, "E326", {"start": v(-9.35, -9.5) * mm, "end": v(-9.29, -9.47) * mm});
            skLineSegment(sketch, "E327", {"start": v(-9.29, -9.47) * mm, "end": v(-9.23, -9.44) * mm});
            skLineSegment(sketch, "E328", {"start": v(-9.23, -9.44) * mm, "end": v(-9.17, -9.42) * mm});
            skLineSegment(sketch, "E329", {"start": v(-9.17, -9.42) * mm, "end": v(-9.12, -9.4) * mm});
            skLineSegment(sketch, "E330", {"start": v(-9.12, -9.4) * mm, "end": v(-9.07, -9.36) * mm});
            skLineSegment(sketch, "E331", {"start": v(-9.07, -9.36) * mm, "end": v(-9.02, -9.34) * mm});
            skLineSegment(sketch, "E332", {"start": v(-9.02, -9.34) * mm, "end": v(-8.98, -9.31) * mm});
            skLineSegment(sketch, "E333", {"start": v(-8.98, -9.31) * mm, "end": v(-8.94, -9.29) * mm});
            skLineSegment(sketch, "E334", {"start": v(-8.94, -9.29) * mm, "end": v(-8.9, -9.27) * mm});
            skLineSegment(sketch, "E335", {"start": v(-8.9, -9.27) * mm, "end": v(-8.87, -9.25) * mm});
            skLineSegment(sketch, "E336", {"start": v(-8.87, -9.25) * mm, "end": v(-8.85, -9.24) * mm});
            skLineSegment(sketch, "E337", {"start": v(-8.85, -9.24) * mm, "end": v(-8.82, -9.22) * mm});
            skLineSegment(sketch, "E338", {"start": v(-8.82, -9.22) * mm, "end": v(-8.8, -9.2) * mm});
            skLineSegment(sketch, "E339", {"start": v(-8.8, -9.2) * mm, "end": v(-8.77, -9.2) * mm});
            skLineSegment(sketch, "E340", {"start": v(-8.77, -9.2) * mm, "end": v(-8.75, -9.18) * mm});
            skLineSegment(sketch, "E341", {"start": v(-8.75, -9.18) * mm, "end": v(-8.73, -9.18) * mm});
            skLineSegment(sketch, "E342", {"start": v(-8.73, -9.18) * mm, "end": v(-8.71, -9.18) * mm});
            skLineSegment(sketch, "E343", {"start": v(-8.71, -9.18) * mm, "end": v(-8.7, -9.18) * mm});
            skLineSegment(sketch, "E344", {"start": v(-8.7, -9.18) * mm, "end": v(-8.69, -9.18) * mm});
            skLineSegment(sketch, "E345", {"start": v(-8.69, -9.18) * mm, "end": v(-8.68, -9.19) * mm});
            skLineSegment(sketch, "E346", {"start": v(-8.68, -9.19) * mm, "end": v(-8.54, -9.33) * mm});
            skLineSegment(sketch, "E347", {"start": v(-8.54, -9.33) * mm, "end": v(-8.4, -9.47) * mm});
            skLineSegment(sketch, "E348", {"start": v(-8.4, -9.47) * mm, "end": v(-8.25, -9.61) * mm});
            skLineSegment(sketch, "E349", {"start": v(-8.25, -9.61) * mm, "end": v(-8.25, -9.62) * mm});
            skLineSegment(sketch, "E350", {"start": v(-8.25, -9.62) * mm, "end": v(-8.24, -9.63) * mm});
            skLineSegment(sketch, "E351", {"start": v(-8.24, -9.63) * mm, "end": v(-8.24, -9.65) * mm});
            skLineSegment(sketch, "E352", {"start": v(-8.24, -9.65) * mm, "end": v(-8.25, -9.67) * mm});
            skLineSegment(sketch, "E353", {"start": v(-8.25, -9.67) * mm, "end": v(-8.25, -9.69) * mm});
            skLineSegment(sketch, "E354", {"start": v(-8.25, -9.69) * mm, "end": v(-8.26, -9.7) * mm});
            skLineSegment(sketch, "E355", {"start": v(-8.26, -9.7) * mm, "end": v(-8.27, -9.73) * mm});
            skLineSegment(sketch, "E356", {"start": v(-8.27, -9.73) * mm, "end": v(-8.28, -9.76) * mm});
            skLineSegment(sketch, "E357", {"start": v(-8.28, -9.76) * mm, "end": v(-8.3, -9.78) * mm});
            skLineSegment(sketch, "E358", {"start": v(-8.3, -9.78) * mm, "end": v(-8.31, -9.8) * mm});
            skLineSegment(sketch, "E359", {"start": v(-8.31, -9.8) * mm, "end": v(-8.33, -9.83) * mm});
            skLineSegment(sketch, "E360", {"start": v(-8.33, -9.83) * mm, "end": v(-8.36, -9.87) * mm});
            skLineSegment(sketch, "E361", {"start": v(-8.36, -9.87) * mm, "end": v(-8.38, -9.91) * mm});
            skLineSegment(sketch, "E362", {"start": v(-8.38, -9.91) * mm, "end": v(-8.4, -9.95) * mm});
            skLineSegment(sketch, "E363", {"start": v(-8.4, -9.95) * mm, "end": v(-8.43, -10) * mm});
            skLineSegment(sketch, "E364", {"start": v(-8.43, -10) * mm, "end": v(-8.46, -10.05) * mm});
            skLineSegment(sketch, "E365", {"start": v(-8.46, -10.05) * mm, "end": v(-8.48, -10.1) * mm});
            skLineSegment(sketch, "E366", {"start": v(-8.48, -10.1) * mm, "end": v(-8.51, -10.16) * mm});
            skLineSegment(sketch, "E367", {"start": v(-8.51, -10.16) * mm, "end": v(-8.54, -10.22) * mm});
            skLineSegment(sketch, "E368", {"start": v(-8.54, -10.22) * mm, "end": v(-8.57, -10.28) * mm});
            skLineSegment(sketch, "E369", {"start": v(-8.57, -10.28) * mm, "end": v(-8.6, -10.35) * mm});
            skLineSegment(sketch, "E370", {"start": v(-8.6, -10.35) * mm, "end": v(-8.63, -10.42) * mm});
            skLineSegment(sketch, "E371", {"start": v(-8.63, -10.42) * mm, "end": v(-8.66, -10.5) * mm});
            skLineSegment(sketch, "E372", {"start": v(-8.66, -10.5) * mm, "end": v(-8.68, -10.57) * mm});
            skLineSegment(sketch, "E373", {"start": v(-8.68, -10.57) * mm, "end": v(-8.71, -10.65) * mm});
            skLineSegment(sketch, "E374", {"start": v(-8.71, -10.65) * mm, "end": v(-8.74, -10.74) * mm});
            skLineSegment(sketch, "E375", {"start": v(-8.74, -10.74) * mm, "end": v(-8.77, -10.82) * mm});
            skLineSegment(sketch, "E376", {"start": v(-8.77, -10.82) * mm, "end": v(-8.8, -10.91) * mm});
            skLineSegment(sketch, "E377", {"start": v(-8.8, -10.91) * mm, "end": v(-8.82, -10.98) * mm});
            skLineSegment(sketch, "E378", {"start": v(-8.82, -10.98) * mm, "end": v(-8.62, -11.18) * mm});
            skLineSegment(sketch, "E379", {"start": v(-8.62, -11.18) * mm, "end": v(-8.39, -11.34) * mm});
            skLineSegment(sketch, "E380", {"start": v(-8.39, -11.34) * mm, "end": v(-8.33, -11.32) * mm});
            skLineSegment(sketch, "E381", {"start": v(-8.33, -11.32) * mm, "end": v(-8.24, -11.28) * mm});
            skLineSegment(sketch, "E382", {"start": v(-8.24, -11.28) * mm, "end": v(-8.16, -11.23) * mm});
            skLineSegment(sketch, "E383", {"start": v(-8.16, -11.23) * mm, "end": v(-8.08, -11.2) * mm});
            skLineSegment(sketch, "E384", {"start": v(-8.08, -11.2) * mm, "end": v(-8, -11.15) * mm});
            skLineSegment(sketch, "E385", {"start": v(-8, -11.15) * mm, "end": v(-7.93, -11.1) * mm});
            skLineSegment(sketch, "E386", {"start": v(-7.93, -11.1) * mm, "end": v(-7.87, -11.07) * mm});
            skLineSegment(sketch, "E387", {"start": v(-7.87, -11.07) * mm, "end": v(-7.8, -11.03) * mm});
            skLineSegment(sketch, "E388", {"start": v(-7.8, -11.03) * mm, "end": v(-7.74, -11) * mm});
            skLineSegment(sketch, "E389", {"start": v(-7.74, -11) * mm, "end": v(-7.68, -10.95) * mm});
            skLineSegment(sketch, "E390", {"start": v(-7.68, -10.95) * mm, "end": v(-7.63, -10.92) * mm});
            skLineSegment(sketch, "E391", {"start": v(-7.63, -10.92) * mm, "end": v(-7.58, -10.88) * mm});
            skLineSegment(sketch, "E392", {"start": v(-7.58, -10.88) * mm, "end": v(-7.53, -10.84) * mm});
            skLineSegment(sketch, "E393", {"start": v(-7.53, -10.84) * mm, "end": v(-7.48, -10.81) * mm});
            skLineSegment(sketch, "E394", {"start": v(-7.48, -10.81) * mm, "end": v(-7.44, -10.78) * mm});
            skLineSegment(sketch, "E395", {"start": v(-7.44, -10.78) * mm, "end": v(-7.4, -10.75) * mm});
            skLineSegment(sketch, "E396", {"start": v(-7.4, -10.75) * mm, "end": v(-7.37, -10.72) * mm});
            skLineSegment(sketch, "E397", {"start": v(-7.37, -10.72) * mm, "end": v(-7.33, -10.69) * mm});
            skLineSegment(sketch, "E398", {"start": v(-7.33, -10.69) * mm, "end": v(-7.3, -10.66) * mm});
            skLineSegment(sketch, "E399", {"start": v(-7.3, -10.66) * mm, "end": v(-7.29, -10.65) * mm});
            skLineSegment(sketch, "E400", {"start": v(-7.29, -10.65) * mm, "end": v(-7.26, -10.63) * mm});
            skLineSegment(sketch, "E401", {"start": v(-7.26, -10.63) * mm, "end": v(-7.24, -10.6) * mm});
            skLineSegment(sketch, "E402", {"start": v(-7.24, -10.6) * mm, "end": v(-7.22, -10.6) * mm});
            skLineSegment(sketch, "E403", {"start": v(-7.22, -10.6) * mm, "end": v(-7.2, -10.58) * mm});
            skLineSegment(sketch, "E404", {"start": v(-7.2, -10.58) * mm, "end": v(-7.18, -10.58) * mm});
            skLineSegment(sketch, "E405", {"start": v(-7.18, -10.58) * mm, "end": v(-7.16, -10.57) * mm});
            skLineSegment(sketch, "E406", {"start": v(-7.16, -10.57) * mm, "end": v(-7.15, -10.57) * mm});
            skLineSegment(sketch, "E407", {"start": v(-7.15, -10.57) * mm, "end": v(-7.14, -10.57) * mm});
            skLineSegment(sketch, "E408", {"start": v(-7.14, -10.57) * mm, "end": v(-7.13, -10.57) * mm});
            skLineSegment(sketch, "E409", {"start": v(-7.13, -10.57) * mm, "end": v(-6.97, -10.7) * mm});
            skLineSegment(sketch, "E410", {"start": v(-6.97, -10.7) * mm, "end": v(-6.8, -10.81) * mm});
            skLineSegment(sketch, "E411", {"start": v(-6.8, -10.81) * mm, "end": v(-6.64, -10.93) * mm});
            skLineSegment(sketch, "E412", {"start": v(-6.64, -10.93) * mm, "end": v(-6.63, -10.94) * mm});
            skLineSegment(sketch, "E413", {"start": v(-6.63, -10.94) * mm, "end": v(-6.63, -10.95) * mm});
            skLineSegment(sketch, "E414", {"start": v(-6.63, -10.95) * mm, "end": v(-6.62, -10.96) * mm});
            skLineSegment(sketch, "E415", {"start": v(-6.62, -10.96) * mm, "end": v(-6.62, -10.98) * mm});
            skLineSegment(sketch, "E416", {"start": v(-6.62, -10.98) * mm, "end": v(-6.63, -11) * mm});
            skLineSegment(sketch, "E417", {"start": v(-6.63, -11) * mm, "end": v(-6.63, -11.02) * mm});
            skLineSegment(sketch, "E418", {"start": v(-6.63, -11.02) * mm, "end": v(-6.64, -11.05) * mm});
            skLineSegment(sketch, "E419", {"start": v(-6.64, -11.05) * mm, "end": v(-6.65, -11.08) * mm});
            skLineSegment(sketch, "E420", {"start": v(-6.65, -11.08) * mm, "end": v(-6.66, -11.1) * mm});
            skLineSegment(sketch, "E421", {"start": v(-6.66, -11.1) * mm, "end": v(-6.67, -11.12) * mm});
            skLineSegment(sketch, "E422", {"start": v(-6.67, -11.12) * mm, "end": v(-6.68, -11.16) * mm});
            skLineSegment(sketch, "E423", {"start": v(-6.68, -11.16) * mm, "end": v(-6.7, -11.2) * mm});
            skLineSegment(sketch, "E424", {"start": v(-6.7, -11.2) * mm, "end": v(-6.72, -11.24) * mm});
            skLineSegment(sketch, "E425", {"start": v(-6.72, -11.24) * mm, "end": v(-6.74, -11.3) * mm});
            skLineSegment(sketch, "E426", {"start": v(-6.74, -11.3) * mm, "end": v(-6.75, -11.34) * mm});
            skLineSegment(sketch, "E427", {"start": v(-6.75, -11.34) * mm, "end": v(-6.77, -11.4) * mm});
            skLineSegment(sketch, "E428", {"start": v(-6.77, -11.4) * mm, "end": v(-6.8, -11.45) * mm});
            skLineSegment(sketch, "E429", {"start": v(-6.8, -11.45) * mm, "end": v(-6.8, -11.51) * mm});
            skLineSegment(sketch, "E430", {"start": v(-6.8, -11.51) * mm, "end": v(-6.83, -11.57) * mm});
            skLineSegment(sketch, "E431", {"start": v(-6.83, -11.57) * mm, "end": v(-6.85, -11.64) * mm});
            skLineSegment(sketch, "E432", {"start": v(-6.85, -11.64) * mm, "end": v(-6.86, -11.71) * mm});
            skLineSegment(sketch, "E433", {"start": v(-6.86, -11.71) * mm, "end": v(-6.88, -11.78) * mm});
            skLineSegment(sketch, "E434", {"start": v(-6.88, -11.78) * mm, "end": v(-6.9, -11.86) * mm});
            skLineSegment(sketch, "E435", {"start": v(-6.9, -11.86) * mm, "end": v(-6.92, -11.94) * mm});
            skLineSegment(sketch, "E436", {"start": v(-6.92, -11.94) * mm, "end": v(-6.93, -12.03) * mm});
            skLineSegment(sketch, "E437", {"start": v(-6.93, -12.03) * mm, "end": v(-6.95, -12.11) * mm});
            skLineSegment(sketch, "E438", {"start": v(-6.95, -12.11) * mm, "end": v(-6.96, -12.2) * mm});
            skLineSegment(sketch, "E439", {"start": v(-6.96, -12.2) * mm, "end": v(-6.97, -12.3) * mm});
            skLineSegment(sketch, "E440", {"start": v(-6.97, -12.3) * mm, "end": v(-6.98, -12.36) * mm});
            skLineSegment(sketch, "E441", {"start": v(-6.98, -12.36) * mm, "end": v(-6.75, -12.53) * mm});
            skLineSegment(sketch, "E442", {"start": v(-6.75, -12.53) * mm, "end": v(-6.5, -12.66) * mm});
            skLineSegment(sketch, "E443", {"start": v(-6.5, -12.66) * mm, "end": v(-6.45, -12.62) * mm});
            skLineSegment(sketch, "E444", {"start": v(-6.45, -12.62) * mm, "end": v(-6.37, -12.57) * mm});
            skLineSegment(sketch, "E445", {"start": v(-6.37, -12.57) * mm, "end": v(-6.3, -12.51) * mm});
            skLineSegment(sketch, "E446", {"start": v(-6.3, -12.51) * mm, "end": v(-6.22, -12.46) * mm});
            skLineSegment(sketch, "E447", {"start": v(-6.22, -12.46) * mm, "end": v(-6.15, -12.4) * mm});
            skLineSegment(sketch, "E448", {"start": v(-6.15, -12.4) * mm, "end": v(-6.1, -12.36) * mm});
            skLineSegment(sketch, "E449", {"start": v(-6.1, -12.36) * mm, "end": v(-6.03, -12.3) * mm});
            skLineSegment(sketch, "E450", {"start": v(-6.03, -12.3) * mm, "end": v(-5.97, -12.26) * mm});
            skLineSegment(sketch, "E451", {"start": v(-5.97, -12.26) * mm, "end": v(-5.92, -12.2) * mm});
            skLineSegment(sketch, "E452", {"start": v(-5.92, -12.2) * mm, "end": v(-5.87, -12.16) * mm});
            skLineSegment(sketch, "E453", {"start": v(-5.87, -12.16) * mm, "end": v(-5.82, -12.12) * mm});
            skLineSegment(sketch, "E454", {"start": v(-5.82, -12.12) * mm, "end": v(-5.77, -12.07) * mm});
            skLineSegment(sketch, "E455", {"start": v(-5.77, -12.07) * mm, "end": v(-5.73, -12.03) * mm});
            skLineSegment(sketch, "E456", {"start": v(-5.73, -12.03) * mm, "end": v(-5.7, -12) * mm});
            skLineSegment(sketch, "E457", {"start": v(-5.7, -12) * mm, "end": v(-5.66, -11.95) * mm});
            skLineSegment(sketch, "E458", {"start": v(-5.66, -11.95) * mm, "end": v(-5.62, -11.92) * mm});
            skLineSegment(sketch, "E459", {"start": v(-5.62, -11.92) * mm, "end": v(-5.6, -11.88) * mm});
            skLineSegment(sketch, "E460", {"start": v(-5.6, -11.88) * mm, "end": v(-5.56, -11.85) * mm});
            skLineSegment(sketch, "E461", {"start": v(-5.56, -11.85) * mm, "end": v(-5.54, -11.82) * mm});
            skLineSegment(sketch, "E462", {"start": v(-5.54, -11.82) * mm, "end": v(-5.53, -11.8) * mm});
            skLineSegment(sketch, "E463", {"start": v(-5.53, -11.8) * mm, "end": v(-5.5, -11.78) * mm});
            skLineSegment(sketch, "E464", {"start": v(-5.5, -11.78) * mm, "end": v(-5.48, -11.76) * mm});
            skLineSegment(sketch, "E465", {"start": v(-5.48, -11.76) * mm, "end": v(-5.46, -11.74) * mm});
            skLineSegment(sketch, "E466", {"start": v(-5.46, -11.74) * mm, "end": v(-5.45, -11.72) * mm});
            skLineSegment(sketch, "E467", {"start": v(-5.45, -11.72) * mm, "end": v(-5.43, -11.71) * mm});
            skLineSegment(sketch, "E468", {"start": v(-5.43, -11.71) * mm, "end": v(-5.41, -11.7) * mm});
            skLineSegment(sketch, "E469", {"start": v(-5.41, -11.7) * mm, "end": v(-5.4, -11.7) * mm});
            skLineSegment(sketch, "E470", {"start": v(-5.4, -11.7) * mm, "end": v(-5.39, -11.7) * mm});
            skLineSegment(sketch, "E471", {"start": v(-5.39, -11.7) * mm, "end": v(-5.38, -11.7) * mm});
            skLineSegment(sketch, "E472", {"start": v(-5.38, -11.7) * mm, "end": v(-5.2, -11.8) * mm});
            skLineSegment(sketch, "E473", {"start": v(-5.2, -11.8) * mm, "end": v(-5.02, -11.89) * mm});
            skLineSegment(sketch, "E474", {"start": v(-5.02, -11.89) * mm, "end": v(-4.84, -11.97) * mm});
            skLineSegment(sketch, "E475", {"start": v(-4.84, -11.97) * mm, "end": v(-4.83, -11.98) * mm});
            skLineSegment(sketch, "E476", {"start": v(-4.83, -11.98) * mm, "end": v(-4.82, -12) * mm});
            skLineSegment(sketch, "E477", {"start": v(-4.82, -12) * mm, "end": v(-4.82, -12) * mm});
            skLineSegment(sketch, "E478", {"start": v(-4.82, -12) * mm, "end": v(-4.82, -12.02) * mm});
            skLineSegment(sketch, "E479", {"start": v(-4.82, -12.02) * mm, "end": v(-4.82, -12.04) * mm});
            skLineSegment(sketch, "E480", {"start": v(-4.82, -12.04) * mm, "end": v(-4.82, -12.07) * mm});
            skLineSegment(sketch, "E481", {"start": v(-4.82, -12.07) * mm, "end": v(-4.82, -12.1) * mm});
            skLineSegment(sketch, "E482", {"start": v(-4.82, -12.1) * mm, "end": v(-4.83, -12.12) * mm});
            skLineSegment(sketch, "E483", {"start": v(-4.83, -12.12) * mm, "end": v(-4.83, -12.15) * mm});
            skLineSegment(sketch, "E484", {"start": v(-4.83, -12.15) * mm, "end": v(-4.84, -12.17) * mm});
            skLineSegment(sketch, "E485", {"start": v(-4.84, -12.17) * mm, "end": v(-4.85, -12.21) * mm});
            skLineSegment(sketch, "E486", {"start": v(-4.85, -12.21) * mm, "end": v(-4.86, -12.25) * mm});
            skLineSegment(sketch, "E487", {"start": v(-4.86, -12.25) * mm, "end": v(-4.87, -12.3) * mm});
            skLineSegment(sketch, "E488", {"start": v(-4.87, -12.3) * mm, "end": v(-4.88, -12.35) * mm});
            skLineSegment(sketch, "E489", {"start": v(-4.88, -12.35) * mm, "end": v(-4.89, -12.4) * mm});
            skLineSegment(sketch, "E490", {"start": v(-4.89, -12.4) * mm, "end": v(-4.9, -12.46) * mm});
            skLineSegment(sketch, "E491", {"start": v(-4.9, -12.46) * mm, "end": v(-4.9, -12.51) * mm});
            skLineSegment(sketch, "E492", {"start": v(-4.9, -12.51) * mm, "end": v(-4.92, -12.58) * mm});
            skLineSegment(sketch, "E493", {"start": v(-4.92, -12.58) * mm, "end": v(-4.92, -12.64) * mm});
            skLineSegment(sketch, "E494", {"start": v(-4.92, -12.64) * mm, "end": v(-4.93, -12.71) * mm});
            skLineSegment(sketch, "E495", {"start": v(-4.93, -12.71) * mm, "end": v(-4.94, -12.78) * mm});
            skLineSegment(sketch, "E496", {"start": v(-4.94, -12.78) * mm, "end": v(-4.95, -12.86) * mm});
            skLineSegment(sketch, "E497", {"start": v(-4.95, -12.86) * mm, "end": v(-4.95, -12.94) * mm});
            skLineSegment(sketch, "E498", {"start": v(-4.95, -12.94) * mm, "end": v(-4.95, -13.02) * mm});
            skLineSegment(sketch, "E499", {"start": v(-4.95, -13.02) * mm, "end": v(-4.96, -13.1) * mm});
            skLineSegment(sketch, "E500", {"start": v(-4.96, -13.1) * mm, "end": v(-4.96, -13.2) * mm});
            skLineSegment(sketch, "E501", {"start": v(-4.96, -13.2) * mm, "end": v(-4.96, -13.29) * mm});
            skLineSegment(sketch, "E502", {"start": v(-4.96, -13.29) * mm, "end": v(-4.96, -13.38) * mm});
            skLineSegment(sketch, "E503", {"start": v(-4.96, -13.38) * mm, "end": v(-4.95, -13.45) * mm});
            skLineSegment(sketch, "E504", {"start": v(-4.95, -13.45) * mm, "end": v(-4.7, -13.58) * mm});
            skLineSegment(sketch, "E505", {"start": v(-4.7, -13.58) * mm, "end": v(-4.43, -13.66) * mm});
            skLineSegment(sketch, "E506", {"start": v(-4.43, -13.66) * mm, "end": v(-4.38, -13.62) * mm});
            skLineSegment(sketch, "E507", {"start": v(-4.38, -13.62) * mm, "end": v(-4.32, -13.55) * mm});
            skLineSegment(sketch, "E508", {"start": v(-4.32, -13.55) * mm, "end": v(-4.25, -13.49) * mm});
            skLineSegment(sketch, "E509", {"start": v(-4.25, -13.49) * mm, "end": v(-4.19, -13.42) * mm});
            skLineSegment(sketch, "E510", {"start": v(-4.19, -13.42) * mm, "end": v(-4.13, -13.36) * mm});
            skLineSegment(sketch, "E511", {"start": v(-4.13, -13.36) * mm, "end": v(-4.07, -13.3) * mm});
            skLineSegment(sketch, "E512", {"start": v(-4.07, -13.3) * mm, "end": v(-4.02, -13.24) * mm});
            skLineSegment(sketch, "E513", {"start": v(-4.02, -13.24) * mm, "end": v(-3.97, -13.18) * mm});
            skLineSegment(sketch, "E514", {"start": v(-3.97, -13.18) * mm, "end": v(-3.93, -13.13) * mm});
            skLineSegment(sketch, "E515", {"start": v(-3.93, -13.13) * mm, "end": v(-3.88, -13.07) * mm});
            skLineSegment(sketch, "E516", {"start": v(-3.88, -13.07) * mm, "end": v(-3.84, -13.02) * mm});
            skLineSegment(sketch, "E517", {"start": v(-3.84, -13.02) * mm, "end": v(-3.8, -12.97) * mm});
            skLineSegment(sketch, "E518", {"start": v(-3.8, -12.97) * mm, "end": v(-3.77, -12.92) * mm});
            skLineSegment(sketch, "E519", {"start": v(-3.77, -12.92) * mm, "end": v(-3.74, -12.88) * mm});
            skLineSegment(sketch, "E520", {"start": v(-3.74, -12.88) * mm, "end": v(-3.7, -12.83) * mm});
            skLineSegment(sketch, "E521", {"start": v(-3.7, -12.83) * mm, "end": v(-3.68, -12.8) * mm});
            skLineSegment(sketch, "E522", {"start": v(-3.68, -12.8) * mm, "end": v(-3.66, -12.75) * mm});
            skLineSegment(sketch, "E523", {"start": v(-3.66, -12.75) * mm, "end": v(-3.63, -12.72) * mm});
            skLineSegment(sketch, "E524", {"start": v(-3.63, -12.72) * mm, "end": v(-3.61, -12.68) * mm});
            skLineSegment(sketch, "E525", {"start": v(-3.61, -12.68) * mm, "end": v(-3.6, -12.66) * mm});
            skLineSegment(sketch, "E526", {"start": v(-3.6, -12.66) * mm, "end": v(-3.59, -12.64) * mm});
            skLineSegment(sketch, "E527", {"start": v(-3.59, -12.64) * mm, "end": v(-3.57, -12.61) * mm});
            skLineSegment(sketch, "E528", {"start": v(-3.57, -12.61) * mm, "end": v(-3.55, -12.6) * mm});
            skLineSegment(sketch, "E529", {"start": v(-3.55, -12.6) * mm, "end": v(-3.54, -12.57) * mm});
            skLineSegment(sketch, "E530", {"start": v(-3.54, -12.57) * mm, "end": v(-3.52, -12.56) * mm});
            skLineSegment(sketch, "E531", {"start": v(-3.52, -12.56) * mm, "end": v(-3.5, -12.55) * mm});
            skLineSegment(sketch, "E532", {"start": v(-3.5, -12.55) * mm, "end": v(-3.5, -12.54) * mm});
            skLineSegment(sketch, "E533", {"start": v(-3.5, -12.54) * mm, "end": v(-3.48, -12.54) * mm});
            skLineSegment(sketch, "E534", {"start": v(-3.48, -12.54) * mm, "end": v(-3.47, -12.54) * mm});
            skLineSegment(sketch, "E535", {"start": v(-3.47, -12.54) * mm, "end": v(-3.28, -12.6) * mm});
            skLineSegment(sketch, "E536", {"start": v(-3.28, -12.6) * mm, "end": v(-3.09, -12.67) * mm});
            skLineSegment(sketch, "E537", {"start": v(-3.09, -12.67) * mm, "end": v(-2.9, -12.73) * mm});
            skLineSegment(sketch, "E538", {"start": v(-2.9, -12.73) * mm, "end": v(-2.89, -12.73) * mm});
            skLineSegment(sketch, "E539", {"start": v(-2.89, -12.73) * mm, "end": v(-2.88, -12.74) * mm});
            skLineSegment(sketch, "E540", {"start": v(-2.88, -12.74) * mm, "end": v(-2.87, -12.76) * mm});
            skLineSegment(sketch, "E541", {"start": v(-2.87, -12.76) * mm, "end": v(-2.87, -12.77) * mm});
            skLineSegment(sketch, "E542", {"start": v(-2.87, -12.77) * mm, "end": v(-2.86, -12.8) * mm});
            skLineSegment(sketch, "E543", {"start": v(-2.86, -12.8) * mm, "end": v(-2.86, -12.82) * mm});
            skLineSegment(sketch, "E544", {"start": v(-2.86, -12.82) * mm, "end": v(-2.86, -12.84) * mm});
            skLineSegment(sketch, "E545", {"start": v(-2.86, -12.84) * mm, "end": v(-2.86, -12.87) * mm});
            skLineSegment(sketch, "E546", {"start": v(-2.86, -12.87) * mm, "end": v(-2.86, -12.9) * mm});
            skLineSegment(sketch, "E547", {"start": v(-2.86, -12.9) * mm, "end": v(-2.87, -12.92) * mm});
            skLineSegment(sketch, "E548", {"start": v(-2.87, -12.92) * mm, "end": v(-2.87, -12.96) * mm});
            skLineSegment(sketch, "E549", {"start": v(-2.87, -12.96) * mm, "end": v(-2.87, -13) * mm});
            skLineSegment(sketch, "E550", {"start": v(-2.87, -13) * mm, "end": v(-2.88, -13.05) * mm});
            skLineSegment(sketch, "E551", {"start": v(-2.88, -13.05) * mm, "end": v(-2.88, -13.1) * mm});
            skLineSegment(sketch, "E552", {"start": v(-2.88, -13.1) * mm, "end": v(-2.88, -13.16) * mm});
            skLineSegment(sketch, "E553", {"start": v(-2.88, -13.16) * mm, "end": v(-2.88, -13.21) * mm});
            skLineSegment(sketch, "E554", {"start": v(-2.88, -13.21) * mm, "end": v(-2.88, -13.27) * mm});
            skLineSegment(sketch, "E555", {"start": v(-2.88, -13.27) * mm, "end": v(-2.88, -13.33) * mm});
            skLineSegment(sketch, "E556", {"start": v(-2.88, -13.33) * mm, "end": v(-2.88, -13.4) * mm});
            skLineSegment(sketch, "E557", {"start": v(-2.88, -13.4) * mm, "end": v(-2.87, -13.47) * mm});
            skLineSegment(sketch, "E558", {"start": v(-2.87, -13.47) * mm, "end": v(-2.87, -13.54) * mm});
            skLineSegment(sketch, "E559", {"start": v(-2.87, -13.54) * mm, "end": v(-2.86, -13.62) * mm});
            skLineSegment(sketch, "E560", {"start": v(-2.86, -13.62) * mm, "end": v(-2.86, -13.7) * mm});
            skLineSegment(sketch, "E561", {"start": v(-2.86, -13.7) * mm, "end": v(-2.85, -13.78) * mm});
            skLineSegment(sketch, "E562", {"start": v(-2.85, -13.78) * mm, "end": v(-2.84, -13.86) * mm});
            skLineSegment(sketch, "E563", {"start": v(-2.84, -13.86) * mm, "end": v(-2.82, -13.95) * mm});
            skLineSegment(sketch, "E564", {"start": v(-2.82, -13.95) * mm, "end": v(-2.81, -14.04) * mm});
            skLineSegment(sketch, "E565", {"start": v(-2.81, -14.04) * mm, "end": v(-2.8, -14.14) * mm});
            skLineSegment(sketch, "E566", {"start": v(-2.8, -14.14) * mm, "end": v(-2.78, -14.2) * mm});
            skLineSegment(sketch, "E567", {"start": v(-2.78, -14.2) * mm, "end": v(-2.51, -14.29) * mm});
            skLineSegment(sketch, "E568", {"start": v(-2.51, -14.29) * mm, "end": v(-2.23, -14.33) * mm});
            skLineSegment(sketch, "E569", {"start": v(-2.23, -14.33) * mm, "end": v(-2.2, -14.28) * mm});
            skLineSegment(sketch, "E570", {"start": v(-2.2, -14.28) * mm, "end": v(-2.13, -14.2) * mm});
            skLineSegment(sketch, "E571", {"start": v(-2.13, -14.2) * mm, "end": v(-2.08, -14.13) * mm});
            skLineSegment(sketch, "E572", {"start": v(-2.08, -14.13) * mm, "end": v(-2.03, -14.06) * mm});
            skLineSegment(sketch, "E573", {"start": v(-2.03, -14.06) * mm, "end": v(-1.98, -13.99) * mm});
            skLineSegment(sketch, "E574", {"start": v(-1.98, -13.99) * mm, "end": v(-1.94, -13.92) * mm});
            skLineSegment(sketch, "E575", {"start": v(-1.94, -13.92) * mm, "end": v(-1.9, -13.85) * mm});
            skLineSegment(sketch, "E576", {"start": v(-1.9, -13.85) * mm, "end": v(-1.85, -13.79) * mm});
            skLineSegment(sketch, "E577", {"start": v(-1.85, -13.79) * mm, "end": v(-1.82, -13.72) * mm});
            skLineSegment(sketch, "E578", {"start": v(-1.82, -13.72) * mm, "end": v(-1.78, -13.66) * mm});
            skLineSegment(sketch, "E579", {"start": v(-1.78, -13.66) * mm, "end": v(-1.75, -13.6) * mm});
            skLineSegment(sketch, "E580", {"start": v(-1.75, -13.6) * mm, "end": v(-1.72, -13.55) * mm});
            skLineSegment(sketch, "E581", {"start": v(-1.72, -13.55) * mm, "end": v(-1.7, -13.5) * mm});
            skLineSegment(sketch, "E582", {"start": v(-1.7, -13.5) * mm, "end": v(-1.67, -13.45) * mm});
            skLineSegment(sketch, "E583", {"start": v(-1.67, -13.45) * mm, "end": v(-1.65, -13.4) * mm});
            skLineSegment(sketch, "E584", {"start": v(-1.65, -13.4) * mm, "end": v(-1.63, -13.35) * mm});
            skLineSegment(sketch, "E585", {"start": v(-1.63, -13.35) * mm, "end": v(-1.6, -13.31) * mm});
            skLineSegment(sketch, "E586", {"start": v(-1.6, -13.31) * mm, "end": v(-1.6, -13.27) * mm});
            skLineSegment(sketch, "E587", {"start": v(-1.6, -13.27) * mm, "end": v(-1.58, -13.23) * mm});
            skLineSegment(sketch, "E588", {"start": v(-1.58, -13.23) * mm, "end": v(-1.57, -13.21) * mm});
            skLineSegment(sketch, "E589", {"start": v(-1.57, -13.21) * mm, "end": v(-1.56, -13.18) * mm});
            skLineSegment(sketch, "E590", {"start": v(-1.56, -13.18) * mm, "end": v(-1.54, -13.16) * mm});
            skLineSegment(sketch, "E591", {"start": v(-1.54, -13.16) * mm, "end": v(-1.53, -13.13) * mm});
            skLineSegment(sketch, "E592", {"start": v(-1.53, -13.13) * mm, "end": v(-1.52, -13.12) * mm});
            skLineSegment(sketch, "E593", {"start": v(-1.52, -13.12) * mm, "end": v(-1.5, -13.1) * mm});
            skLineSegment(sketch, "E594", {"start": v(-1.5, -13.1) * mm, "end": v(-1.5, -13.09) * mm});
            skLineSegment(sketch, "E595", {"start": v(-1.5, -13.09) * mm, "end": v(-1.48, -13.08) * mm});
            skLineSegment(sketch, "E596", {"start": v(-1.48, -13.08) * mm, "end": v(-1.47, -13.07) * mm});
            skLineSegment(sketch, "E597", {"start": v(-1.47, -13.07) * mm, "end": v(-1.46, -13.07) * mm});
            skLineSegment(sketch, "E598", {"start": v(-1.46, -13.07) * mm, "end": v(-1.26, -13.1) * mm});
            skLineSegment(sketch, "E599", {"start": v(-1.26, -13.1) * mm, "end": v(-1.06, -13.14) * mm});
            skLineSegment(sketch, "E600", {"start": v(-1.06, -13.14) * mm, "end": v(-0.86, -13.17) * mm});
            skLineSegment(sketch, "E601", {"start": v(-0.86, -13.17) * mm, "end": v(-0.85, -13.17) * mm});
            skLineSegment(sketch, "E602", {"start": v(-0.85, -13.17) * mm, "end": v(-0.84, -13.18) * mm});
            skLineSegment(sketch, "E603", {"start": v(-0.84, -13.18) * mm, "end": v(-0.83, -13.2) * mm});
            skLineSegment(sketch, "E604", {"start": v(-0.83, -13.2) * mm, "end": v(-0.83, -13.2) * mm});
            skLineSegment(sketch, "E605", {"start": v(-0.83, -13.2) * mm, "end": v(-0.82, -13.23) * mm});
            skLineSegment(sketch, "E606", {"start": v(-0.82, -13.23) * mm, "end": v(-0.81, -13.25) * mm});
            skLineSegment(sketch, "E607", {"start": v(-0.81, -13.25) * mm, "end": v(-0.8, -13.27) * mm});
            skLineSegment(sketch, "E608", {"start": v(-0.8, -13.27) * mm, "end": v(-0.8, -13.3) * mm});
            skLineSegment(sketch, "E609", {"start": v(-0.8, -13.3) * mm, "end": v(-0.8, -13.34) * mm});
            skLineSegment(sketch, "E610", {"start": v(-0.8, -13.34) * mm, "end": v(-0.8, -13.36) * mm});
            skLineSegment(sketch, "E611", {"start": v(-0.8, -13.36) * mm, "end": v(-0.8, -13.4) * mm});
            skLineSegment(sketch, "E612", {"start": v(-0.8, -13.4) * mm, "end": v(-0.8, -13.44) * mm});
            skLineSegment(sketch, "E613", {"start": v(-0.8, -13.44) * mm, "end": v(-0.8, -13.49) * mm});
            skLineSegment(sketch, "E614", {"start": v(-0.8, -13.49) * mm, "end": v(-0.79, -13.53) * mm});
            skLineSegment(sketch, "E615", {"start": v(-0.79, -13.53) * mm, "end": v(-0.78, -13.59) * mm});
            skLineSegment(sketch, "E616", {"start": v(-0.78, -13.59) * mm, "end": v(-0.77, -13.64) * mm});
            skLineSegment(sketch, "E617", {"start": v(-0.77, -13.64) * mm, "end": v(-0.76, -13.7) * mm});
            skLineSegment(sketch, "E618", {"start": v(-0.76, -13.7) * mm, "end": v(-0.75, -13.76) * mm});
            skLineSegment(sketch, "E619", {"start": v(-0.75, -13.76) * mm, "end": v(-0.74, -13.83) * mm});
            skLineSegment(sketch, "E620", {"start": v(-0.74, -13.83) * mm, "end": v(-0.72, -13.9) * mm});
            skLineSegment(sketch, "E621", {"start": v(-0.72, -13.9) * mm, "end": v(-0.7, -13.97) * mm});
            skLineSegment(sketch, "E622", {"start": v(-0.7, -13.97) * mm, "end": v(-0.7, -14.04) * mm});
            skLineSegment(sketch, "E623", {"start": v(-0.7, -14.04) * mm, "end": v(-0.67, -14.12) * mm});
            skLineSegment(sketch, "E624", {"start": v(-0.67, -14.12) * mm, "end": v(-0.65, -14.2) * mm});
            skLineSegment(sketch, "E625", {"start": v(-0.65, -14.2) * mm, "end": v(-0.63, -14.28) * mm});
            skLineSegment(sketch, "E626", {"start": v(-0.63, -14.28) * mm, "end": v(-0.6, -14.36) * mm});
            skLineSegment(sketch, "E627", {"start": v(-0.6, -14.36) * mm, "end": v(-0.57, -14.45) * mm});
            skLineSegment(sketch, "E628", {"start": v(-0.57, -14.45) * mm, "end": v(-0.54, -14.54) * mm});
            skLineSegment(sketch, "E629", {"start": v(-0.54, -14.54) * mm, "end": v(-0.52, -14.6) * mm});
            skLineSegment(sketch, "E630", {"start": v(-0.52, -14.6) * mm, "end": v(-0.24, -14.65) * mm});
            skLineSegment(sketch, "E631", {"start": v(-0.24, -14.65) * mm, "end": v(0.05, -14.65) * mm});
            skLineSegment(sketch, "E632", {"start": v(0.05, -14.65) * mm, "end": v(0.08, -14.6) * mm});
            skLineSegment(sketch, "E633", {"start": v(0.08, -14.6) * mm, "end": v(0.12, -14.5) * mm});
            skLineSegment(sketch, "E634", {"start": v(0.12, -14.5) * mm, "end": v(0.16, -14.42) * mm});
            skLineSegment(sketch, "E635", {"start": v(0.16, -14.42) * mm, "end": v(0.2, -14.34) * mm});
            skLineSegment(sketch, "E636", {"start": v(0.2, -14.34) * mm, "end": v(0.24, -14.27) * mm});
            skLineSegment(sketch, "E637", {"start": v(0.24, -14.27) * mm, "end": v(0.27, -14.2) * mm});
            skLineSegment(sketch, "E638", {"start": v(0.27, -14.2) * mm, "end": v(0.3, -14.12) * mm});
            skLineSegment(sketch, "E639", {"start": v(0.3, -14.12) * mm, "end": v(0.33, -14.05) * mm});
            skLineSegment(sketch, "E640", {"start": v(0.33, -14.05) * mm, "end": v(0.36, -13.98) * mm});
            skLineSegment(sketch, "E641", {"start": v(0.36, -13.98) * mm, "end": v(0.39, -13.92) * mm});
            skLineSegment(sketch, "E642", {"start": v(0.39, -13.92) * mm, "end": v(0.4, -13.85) * mm});
            skLineSegment(sketch, "E643", {"start": v(0.4, -13.85) * mm, "end": v(0.43, -13.8) * mm});
            skLineSegment(sketch, "E644", {"start": v(0.43, -13.8) * mm, "end": v(0.45, -13.74) * mm});
            skLineSegment(sketch, "E645", {"start": v(0.45, -13.74) * mm, "end": v(0.46, -13.69) * mm});
            skLineSegment(sketch, "E646", {"start": v(0.46, -13.69) * mm, "end": v(0.48, -13.63) * mm});
            skLineSegment(sketch, "E647", {"start": v(0.48, -13.63) * mm, "end": v(0.5, -13.59) * mm});
            skLineSegment(sketch, "E648", {"start": v(0.5, -13.59) * mm, "end": v(0.5, -13.54) * mm});
            skLineSegment(sketch, "E649", {"start": v(0.5, -13.54) * mm, "end": v(0.51, -13.5) * mm});
            skLineSegment(sketch, "E650", {"start": v(0.51, -13.5) * mm, "end": v(0.52, -13.46) * mm});
            skLineSegment(sketch, "E651", {"start": v(0.52, -13.46) * mm, "end": v(0.53, -13.44) * mm});
            skLineSegment(sketch, "E652", {"start": v(0.53, -13.44) * mm, "end": v(0.53, -13.4) * mm});
            skLineSegment(sketch, "E653", {"start": v(0.53, -13.4) * mm, "end": v(0.54, -13.38) * mm});
            skLineSegment(sketch, "E654", {"start": v(0.54, -13.38) * mm, "end": v(0.55, -13.36) * mm});
            skLineSegment(sketch, "E655", {"start": v(0.55, -13.36) * mm, "end": v(0.56, -13.33) * mm});
            skLineSegment(sketch, "E656", {"start": v(0.56, -13.33) * mm, "end": v(0.57, -13.32) * mm});
            skLineSegment(sketch, "E657", {"start": v(0.57, -13.32) * mm, "end": v(0.58, -13.3) * mm});
            skLineSegment(sketch, "E658", {"start": v(0.58, -13.3) * mm, "end": v(0.6, -13.3) * mm});
            skLineSegment(sketch, "E659", {"start": v(0.6, -13.3) * mm, "end": v(0.6, -13.29) * mm});
            skLineSegment(sketch, "E660", {"start": v(0.6, -13.29) * mm, "end": v(0.61, -13.28) * mm});
            skLineSegment(sketch, "E661", {"start": v(0.61, -13.28) * mm, "end": v(0.8, -13.29) * mm});
            skLineSegment(sketch, "E662", {"start": v(0.8, -13.29) * mm, "end": v(1.02, -13.29) * mm});
            skLineSegment(sketch, "E663", {"start": v(1.02, -13.29) * mm, "end": v(1.21, -13.28) * mm});
            skLineSegment(sketch, "E664", {"start": v(1.21, -13.28) * mm, "end": v(1.23, -13.29) * mm});
            skLineSegment(sketch, "E665", {"start": v(1.23, -13.29) * mm, "end": v(1.24, -13.3) * mm});
            skLineSegment(sketch, "E666", {"start": v(1.24, -13.3) * mm, "end": v(1.25, -13.3) * mm});
            skLineSegment(sketch, "E667", {"start": v(1.25, -13.3) * mm, "end": v(1.26, -13.32) * mm});
            skLineSegment(sketch, "E668", {"start": v(1.26, -13.32) * mm, "end": v(1.27, -13.33) * mm});
            skLineSegment(sketch, "E669", {"start": v(1.27, -13.33) * mm, "end": v(1.28, -13.36) * mm});
            skLineSegment(sketch, "E670", {"start": v(1.28, -13.36) * mm, "end": v(1.29, -13.38) * mm});
            skLineSegment(sketch, "E671", {"start": v(1.29, -13.38) * mm, "end": v(1.3, -13.4) * mm});
            skLineSegment(sketch, "E672", {"start": v(1.3, -13.4) * mm, "end": v(1.3, -13.44) * mm});
            skLineSegment(sketch, "E673", {"start": v(1.3, -13.44) * mm, "end": v(1.3, -13.46) * mm});
            skLineSegment(sketch, "E674", {"start": v(1.3, -13.46) * mm, "end": v(1.32, -13.5) * mm});
            skLineSegment(sketch, "E675", {"start": v(1.32, -13.5) * mm, "end": v(1.33, -13.54) * mm});
            skLineSegment(sketch, "E676", {"start": v(1.33, -13.54) * mm, "end": v(1.34, -13.59) * mm});
            skLineSegment(sketch, "E677", {"start": v(1.34, -13.59) * mm, "end": v(1.35, -13.63) * mm});
            skLineSegment(sketch, "E678", {"start": v(1.35, -13.63) * mm, "end": v(1.36, -13.69) * mm});
            skLineSegment(sketch, "E679", {"start": v(1.36, -13.69) * mm, "end": v(1.38, -13.74) * mm});
            skLineSegment(sketch, "E680", {"start": v(1.38, -13.74) * mm, "end": v(1.4, -13.8) * mm});
            skLineSegment(sketch, "E681", {"start": v(1.4, -13.8) * mm, "end": v(1.42, -13.85) * mm});
            skLineSegment(sketch, "E682", {"start": v(1.42, -13.85) * mm, "end": v(1.44, -13.92) * mm});
            skLineSegment(sketch, "E683", {"start": v(1.44, -13.92) * mm, "end": v(1.47, -13.98) * mm});
            skLineSegment(sketch, "E684", {"start": v(1.47, -13.98) * mm, "end": v(1.5, -14.05) * mm});
            skLineSegment(sketch, "E685", {"start": v(1.5, -14.05) * mm, "end": v(1.52, -14.12) * mm});
            skLineSegment(sketch, "E686", {"start": v(1.52, -14.12) * mm, "end": v(1.55, -14.2) * mm});
            skLineSegment(sketch, "E687", {"start": v(1.55, -14.2) * mm, "end": v(1.59, -14.27) * mm});
            skLineSegment(sketch, "E688", {"start": v(1.59, -14.27) * mm, "end": v(1.62, -14.34) * mm});
            skLineSegment(sketch, "E689", {"start": v(1.62, -14.34) * mm, "end": v(1.66, -14.42) * mm});
            skLineSegment(sketch, "E690", {"start": v(1.66, -14.42) * mm, "end": v(1.7, -14.5) * mm});
            skLineSegment(sketch, "E691", {"start": v(1.7, -14.5) * mm, "end": v(1.75, -14.6) * mm});
            skLineSegment(sketch, "E692", {"start": v(1.75, -14.6) * mm, "end": v(1.78, -14.65) * mm});
            skLineSegment(sketch, "E693", {"start": v(1.78, -14.65) * mm, "end": v(2.07, -14.65) * mm});
            skLineSegment(sketch, "E694", {"start": v(2.07, -14.65) * mm, "end": v(2.35, -14.6) * mm});
            skLineSegment(sketch, "E695", {"start": v(2.35, -14.6) * mm, "end": v(2.37, -14.54) * mm});
            skLineSegment(sketch, "E696", {"start": v(2.37, -14.54) * mm, "end": v(2.4, -14.45) * mm});
            skLineSegment(sketch, "E697", {"start": v(2.4, -14.45) * mm, "end": v(2.43, -14.36) * mm});
            skLineSegment(sketch, "E698", {"start": v(2.43, -14.36) * mm, "end": v(2.45, -14.28) * mm});
            skLineSegment(sketch, "E699", {"start": v(2.45, -14.28) * mm, "end": v(2.48, -14.2) * mm});
            skLineSegment(sketch, "E700", {"start": v(2.48, -14.2) * mm, "end": v(2.5, -14.12) * mm});
            skLineSegment(sketch, "E701", {"start": v(2.5, -14.12) * mm, "end": v(2.52, -14.04) * mm});
            skLineSegment(sketch, "E702", {"start": v(2.52, -14.04) * mm, "end": v(2.54, -13.97) * mm});
            skLineSegment(sketch, "E703", {"start": v(2.54, -13.97) * mm, "end": v(2.55, -13.9) * mm});
            skLineSegment(sketch, "E704", {"start": v(2.55, -13.9) * mm, "end": v(2.57, -13.83) * mm});
            skLineSegment(sketch, "E705", {"start": v(2.57, -13.83) * mm, "end": v(2.58, -13.76) * mm});
            skLineSegment(sketch, "E706", {"start": v(2.58, -13.76) * mm, "end": v(2.59, -13.7) * mm});
            skLineSegment(sketch, "E707", {"start": v(2.59, -13.7) * mm, "end": v(2.6, -13.64) * mm});
            skLineSegment(sketch, "E708", {"start": v(2.6, -13.64) * mm, "end": v(2.6, -13.59) * mm});
            skLineSegment(sketch, "E709", {"start": v(2.6, -13.59) * mm, "end": v(2.61, -13.53) * mm});
            skLineSegment(sketch, "E710", {"start": v(2.61, -13.53) * mm, "end": v(2.62, -13.49) * mm});
            skLineSegment(sketch, "E711", {"start": v(2.62, -13.49) * mm, "end": v(2.62, -13.44) * mm});
            skLineSegment(sketch, "E712", {"start": v(2.62, -13.44) * mm, "end": v(2.63, -13.4) * mm});
            skLineSegment(sketch, "E713", {"start": v(2.63, -13.4) * mm, "end": v(2.63, -13.36) * mm});
            skLineSegment(sketch, "E714", {"start": v(2.63, -13.36) * mm, "end": v(2.63, -13.34) * mm});
            skLineSegment(sketch, "E715", {"start": v(2.63, -13.34) * mm, "end": v(2.63, -13.3) * mm});
            skLineSegment(sketch, "E716", {"start": v(2.63, -13.3) * mm, "end": v(2.64, -13.27) * mm});
            skLineSegment(sketch, "E717", {"start": v(2.64, -13.27) * mm, "end": v(2.64, -13.25) * mm});
            skLineSegment(sketch, "E718", {"start": v(2.64, -13.25) * mm, "end": v(2.65, -13.23) * mm});
            skLineSegment(sketch, "E719", {"start": v(2.65, -13.23) * mm, "end": v(2.65, -13.2) * mm});
            skLineSegment(sketch, "E720", {"start": v(2.65, -13.2) * mm, "end": v(2.66, -13.2) * mm});
            skLineSegment(sketch, "E721", {"start": v(2.66, -13.2) * mm, "end": v(2.67, -13.18) * mm});
            skLineSegment(sketch, "E722", {"start": v(2.67, -13.18) * mm, "end": v(2.68, -13.17) * mm});
            skLineSegment(sketch, "E723", {"start": v(2.68, -13.17) * mm, "end": v(2.7, -13.17) * mm});
            skLineSegment(sketch, "E724", {"start": v(2.7, -13.17) * mm, "end": v(2.89, -13.14) * mm});
            skLineSegment(sketch, "E725", {"start": v(2.89, -13.14) * mm, "end": v(3.1, -13.1) * mm});
            skLineSegment(sketch, "E726", {"start": v(3.1, -13.1) * mm, "end": v(3.29, -13.07) * mm});
            skLineSegment(sketch, "E727", {"start": v(3.29, -13.07) * mm, "end": v(3.3, -13.07) * mm});
            skLineSegment(sketch, "E728", {"start": v(3.3, -13.07) * mm, "end": v(3.3, -13.08) * mm});
            skLineSegment(sketch, "E729", {"start": v(3.3, -13.08) * mm, "end": v(3.32, -13.09) * mm});
            skLineSegment(sketch, "E730", {"start": v(3.32, -13.09) * mm, "end": v(3.33, -13.1) * mm});
            skLineSegment(sketch, "E731", {"start": v(3.33, -13.1) * mm, "end": v(3.35, -13.12) * mm});
            skLineSegment(sketch, "E732", {"start": v(3.35, -13.12) * mm, "end": v(3.36, -13.13) * mm});
            skLineSegment(sketch, "E733", {"start": v(3.36, -13.13) * mm, "end": v(3.37, -13.16) * mm});
            skLineSegment(sketch, "E734", {"start": v(3.37, -13.16) * mm, "end": v(3.38, -13.18) * mm});
            skLineSegment(sketch, "E735", {"start": v(3.38, -13.18) * mm, "end": v(3.4, -13.21) * mm});
            skLineSegment(sketch, "E736", {"start": v(3.4, -13.21) * mm, "end": v(3.4, -13.23) * mm});
            skLineSegment(sketch, "E737", {"start": v(3.4, -13.23) * mm, "end": v(3.42, -13.27) * mm});
            skLineSegment(sketch, "E738", {"start": v(3.42, -13.27) * mm, "end": v(3.44, -13.31) * mm});
            skLineSegment(sketch, "E739", {"start": v(3.44, -13.31) * mm, "end": v(3.45, -13.35) * mm});
            skLineSegment(sketch, "E740", {"start": v(3.45, -13.35) * mm, "end": v(3.47, -13.4) * mm});
            skLineSegment(sketch, "E741", {"start": v(3.47, -13.4) * mm, "end": v(3.5, -13.45) * mm});
            skLineSegment(sketch, "E742", {"start": v(3.5, -13.45) * mm, "end": v(3.52, -13.5) * mm});
            skLineSegment(sketch, "E743", {"start": v(3.52, -13.5) * mm, "end": v(3.55, -13.55) * mm});
            skLineSegment(sketch, "E744", {"start": v(3.55, -13.55) * mm, "end": v(3.58, -13.6) * mm});
            skLineSegment(sketch, "E745", {"start": v(3.58, -13.6) * mm, "end": v(3.6, -13.66) * mm});
            skLineSegment(sketch, "E746", {"start": v(3.6, -13.66) * mm, "end": v(3.64, -13.72) * mm});
            skLineSegment(sketch, "E747", {"start": v(3.64, -13.72) * mm, "end": v(3.68, -13.79) * mm});
            skLineSegment(sketch, "E748", {"start": v(3.68, -13.79) * mm, "end": v(3.72, -13.85) * mm});
            skLineSegment(sketch, "E749", {"start": v(3.72, -13.85) * mm, "end": v(3.76, -13.92) * mm});
            skLineSegment(sketch, "E750", {"start": v(3.76, -13.92) * mm, "end": v(3.8, -13.99) * mm});
            skLineSegment(sketch, "E751", {"start": v(3.8, -13.99) * mm, "end": v(3.86, -14.06) * mm});
            skLineSegment(sketch, "E752", {"start": v(3.86, -14.06) * mm, "end": v(3.9, -14.13) * mm});
            skLineSegment(sketch, "E753", {"start": v(3.9, -14.13) * mm, "end": v(3.96, -14.2) * mm});
            skLineSegment(sketch, "E754", {"start": v(3.96, -14.2) * mm, "end": v(4.02, -14.28) * mm});
            skLineSegment(sketch, "E755", {"start": v(4.02, -14.28) * mm, "end": v(4.06, -14.33) * mm});
            skLineSegment(sketch, "E756", {"start": v(4.06, -14.33) * mm, "end": v(4.34, -14.29) * mm});
            skLineSegment(sketch, "E757", {"start": v(4.34, -14.29) * mm, "end": v(4.6, -14.2) * mm});
            skLineSegment(sketch, "E758", {"start": v(4.6, -14.2) * mm, "end": v(4.62, -14.14) * mm});
            skLineSegment(sketch, "E759", {"start": v(4.62, -14.14) * mm, "end": v(4.64, -14.04) * mm});
            skLineSegment(sketch, "E760", {"start": v(4.64, -14.04) * mm, "end": v(4.65, -13.95) * mm});
            skLineSegment(sketch, "E761", {"start": v(4.65, -13.95) * mm, "end": v(4.67, -13.86) * mm});
            skLineSegment(sketch, "E762", {"start": v(4.67, -13.86) * mm, "end": v(4.68, -13.78) * mm});
            skLineSegment(sketch, "E763", {"start": v(4.68, -13.78) * mm, "end": v(4.68, -13.7) * mm});
            skLineSegment(sketch, "E764", {"start": v(4.68, -13.7) * mm, "end": v(4.7, -13.62) * mm});
            skLineSegment(sketch, "E765", {"start": v(4.7, -13.62) * mm, "end": v(4.7, -13.54) * mm});
            skLineSegment(sketch, "E766", {"start": v(4.7, -13.54) * mm, "end": v(4.7, -13.47) * mm});
            skLineSegment(sketch, "E767", {"start": v(4.7, -13.47) * mm, "end": v(4.7, -13.4) * mm});
            skLineSegment(sketch, "E768", {"start": v(4.7, -13.4) * mm, "end": v(4.7, -13.33) * mm});
            skLineSegment(sketch, "E769", {"start": v(4.7, -13.33) * mm, "end": v(4.7, -13.27) * mm});
            skLineSegment(sketch, "E770", {"start": v(4.7, -13.27) * mm, "end": v(4.7, -13.21) * mm});
            skLineSegment(sketch, "E771", {"start": v(4.7, -13.21) * mm, "end": v(4.7, -13.16) * mm});
            skLineSegment(sketch, "E772", {"start": v(4.7, -13.16) * mm, "end": v(4.7, -13.1) * mm});
            skLineSegment(sketch, "E773", {"start": v(4.7, -13.1) * mm, "end": v(4.7, -13.05) * mm});
            skLineSegment(sketch, "E774", {"start": v(4.7, -13.05) * mm, "end": v(4.7, -13) * mm});
            skLineSegment(sketch, "E775", {"start": v(4.7, -13) * mm, "end": v(4.7, -12.96) * mm});
            skLineSegment(sketch, "E776", {"start": v(4.7, -12.96) * mm, "end": v(4.7, -12.92) * mm});
            skLineSegment(sketch, "E777", {"start": v(4.7, -12.92) * mm, "end": v(4.7, -12.9) * mm});
            skLineSegment(sketch, "E778", {"start": v(4.7, -12.9) * mm, "end": v(4.69, -12.87) * mm});
            skLineSegment(sketch, "E779", {"start": v(4.69, -12.87) * mm, "end": v(4.69, -12.84) * mm});
            skLineSegment(sketch, "E780", {"start": v(4.69, -12.84) * mm, "end": v(4.69, -12.82) * mm});
            skLineSegment(sketch, "E781", {"start": v(4.69, -12.82) * mm, "end": v(4.7, -12.8) * mm});
            skLineSegment(sketch, "E782", {"start": v(4.7, -12.8) * mm, "end": v(4.7, -12.77) * mm});
            skLineSegment(sketch, "E783", {"start": v(4.7, -12.77) * mm, "end": v(4.7, -12.76) * mm});
            skLineSegment(sketch, "E784", {"start": v(4.7, -12.76) * mm, "end": v(4.7, -12.74) * mm});
            skLineSegment(sketch, "E785", {"start": v(4.7, -12.74) * mm, "end": v(4.72, -12.73) * mm});
            skLineSegment(sketch, "E786", {"start": v(4.72, -12.73) * mm, "end": v(4.73, -12.73) * mm});
            skLineSegment(sketch, "E787", {"start": v(4.73, -12.73) * mm, "end": v(4.91, -12.67) * mm});
            skLineSegment(sketch, "E788", {"start": v(4.91, -12.67) * mm, "end": v(5.11, -12.6) * mm});
            skLineSegment(sketch, "E789", {"start": v(5.11, -12.6) * mm, "end": v(5.3, -12.54) * mm});
            skLineSegment(sketch, "E790", {"start": v(5.3, -12.54) * mm, "end": v(5.3, -12.54) * mm});
            skLineSegment(sketch, "E791", {"start": v(5.3, -12.54) * mm, "end": v(5.32, -12.54) * mm});
            skLineSegment(sketch, "E792", {"start": v(5.32, -12.54) * mm, "end": v(5.34, -12.55) * mm});
            skLineSegment(sketch, "E793", {"start": v(5.34, -12.55) * mm, "end": v(5.35, -12.56) * mm});
            skLineSegment(sketch, "E794", {"start": v(5.35, -12.56) * mm, "end": v(5.37, -12.57) * mm});
            skLineSegment(sketch, "E795", {"start": v(5.37, -12.57) * mm, "end": v(5.38, -12.6) * mm});
            skLineSegment(sketch, "E796", {"start": v(5.38, -12.6) * mm, "end": v(5.4, -12.61) * mm});
            skLineSegment(sketch, "E797", {"start": v(5.4, -12.61) * mm, "end": v(5.41, -12.64) * mm});
            skLineSegment(sketch, "E798", {"start": v(5.41, -12.64) * mm, "end": v(5.43, -12.66) * mm});
            skLineSegment(sketch, "E799", {"start": v(5.43, -12.66) * mm, "end": v(5.44, -12.68) * mm});
            skLineSegment(sketch, "E800", {"start": v(5.44, -12.68) * mm, "end": v(5.46, -12.72) * mm});
            skLineSegment(sketch, "E801", {"start": v(5.46, -12.72) * mm, "end": v(5.48, -12.75) * mm});
            skLineSegment(sketch, "E802", {"start": v(5.48, -12.75) * mm, "end": v(5.5, -12.8) * mm});
            skLineSegment(sketch, "E803", {"start": v(5.5, -12.8) * mm, "end": v(5.54, -12.83) * mm});
            skLineSegment(sketch, "E804", {"start": v(5.54, -12.83) * mm, "end": v(5.57, -12.88) * mm});
            skLineSegment(sketch, "E805", {"start": v(5.57, -12.88) * mm, "end": v(5.6, -12.92) * mm});
            skLineSegment(sketch, "E806", {"start": v(5.6, -12.92) * mm, "end": v(5.63, -12.97) * mm});
            skLineSegment(sketch, "E807", {"start": v(5.63, -12.97) * mm, "end": v(5.67, -13.02) * mm});
            skLineSegment(sketch, "E808", {"start": v(5.67, -13.02) * mm, "end": v(5.71, -13.07) * mm});
            skLineSegment(sketch, "E809", {"start": v(5.71, -13.07) * mm, "end": v(5.75, -13.13) * mm});
            skLineSegment(sketch, "E810", {"start": v(5.75, -13.13) * mm, "end": v(5.8, -13.18) * mm});
            skLineSegment(sketch, "E811", {"start": v(5.8, -13.18) * mm, "end": v(5.85, -13.24) * mm});
            skLineSegment(sketch, "E812", {"start": v(5.85, -13.24) * mm, "end": v(5.9, -13.3) * mm});
            skLineSegment(sketch, "E813", {"start": v(5.9, -13.3) * mm, "end": v(5.96, -13.36) * mm});
            skLineSegment(sketch, "E814", {"start": v(5.96, -13.36) * mm, "end": v(6.02, -13.42) * mm});
            skLineSegment(sketch, "E815", {"start": v(6.02, -13.42) * mm, "end": v(6.08, -13.49) * mm});
            skLineSegment(sketch, "E816", {"start": v(6.08, -13.49) * mm, "end": v(6.14, -13.55) * mm});
            skLineSegment(sketch, "E817", {"start": v(6.14, -13.55) * mm, "end": v(6.21, -13.62) * mm});
            skLineSegment(sketch, "E818", {"start": v(6.21, -13.62) * mm, "end": v(6.26, -13.66) * mm});
            skLineSegment(sketch, "E819", {"start": v(6.26, -13.66) * mm, "end": v(6.53, -13.58) * mm});
            skLineSegment(sketch, "E820", {"start": v(6.53, -13.58) * mm, "end": v(6.78, -13.45) * mm});
            skLineSegment(sketch, "E821", {"start": v(6.78, -13.45) * mm, "end": v(6.78, -13.38) * mm});
            skLineSegment(sketch, "E822", {"start": v(6.78, -13.38) * mm, "end": v(6.79, -13.29) * mm});
            skLineSegment(sketch, "E823", {"start": v(6.79, -13.29) * mm, "end": v(6.79, -13.2) * mm});
            skLineSegment(sketch, "E824", {"start": v(6.79, -13.2) * mm, "end": v(6.78, -13.1) * mm});
            skLineSegment(sketch, "E825", {"start": v(6.78, -13.1) * mm, "end": v(6.78, -13.02) * mm});
            skLineSegment(sketch, "E826", {"start": v(6.78, -13.02) * mm, "end": v(6.78, -12.94) * mm});
            skLineSegment(sketch, "E827", {"start": v(6.78, -12.94) * mm, "end": v(6.77, -12.86) * mm});
            skLineSegment(sketch, "E828", {"start": v(6.77, -12.86) * mm, "end": v(6.77, -12.78) * mm});
            skLineSegment(sketch, "E829", {"start": v(6.77, -12.78) * mm, "end": v(6.76, -12.71) * mm});
            skLineSegment(sketch, "E830", {"start": v(6.76, -12.71) * mm, "end": v(6.75, -12.64) * mm});
            skLineSegment(sketch, "E831", {"start": v(6.75, -12.64) * mm, "end": v(6.74, -12.58) * mm});
            skLineSegment(sketch, "E832", {"start": v(6.74, -12.58) * mm, "end": v(6.74, -12.51) * mm});
            skLineSegment(sketch, "E833", {"start": v(6.74, -12.51) * mm, "end": v(6.73, -12.46) * mm});
            skLineSegment(sketch, "E834", {"start": v(6.73, -12.46) * mm, "end": v(6.72, -12.4) * mm});
            skLineSegment(sketch, "E835", {"start": v(6.72, -12.4) * mm, "end": v(6.7, -12.35) * mm});
            skLineSegment(sketch, "E836", {"start": v(6.7, -12.35) * mm, "end": v(6.7, -12.3) * mm});
            skLineSegment(sketch, "E837", {"start": v(6.7, -12.3) * mm, "end": v(6.69, -12.25) * mm});
            skLineSegment(sketch, "E838", {"start": v(6.69, -12.25) * mm, "end": v(6.68, -12.21) * mm});
            skLineSegment(sketch, "E839", {"start": v(6.68, -12.21) * mm, "end": v(6.67, -12.17) * mm});
            skLineSegment(sketch, "E840", {"start": v(6.67, -12.17) * mm, "end": v(6.66, -12.15) * mm});
            skLineSegment(sketch, "E841", {"start": v(6.66, -12.15) * mm, "end": v(6.65, -12.12) * mm});
            skLineSegment(sketch, "E842", {"start": v(6.65, -12.12) * mm, "end": v(6.65, -12.1) * mm});
            skLineSegment(sketch, "E843", {"start": v(6.65, -12.1) * mm, "end": v(6.64, -12.07) * mm});
            skLineSegment(sketch, "E844", {"start": v(6.64, -12.07) * mm, "end": v(6.64, -12.04) * mm});
            skLineSegment(sketch, "E845", {"start": v(6.64, -12.04) * mm, "end": v(6.64, -12.02) * mm});
            skLineSegment(sketch, "E846", {"start": v(6.64, -12.02) * mm, "end": v(6.65, -12) * mm});
            skLineSegment(sketch, "E847", {"start": v(6.65, -12) * mm, "end": v(6.65, -12) * mm});
            skLineSegment(sketch, "E848", {"start": v(6.65, -12) * mm, "end": v(6.66, -11.98) * mm});
            skLineSegment(sketch, "E849", {"start": v(6.66, -11.98) * mm, "end": v(6.67, -11.97) * mm});
            skLineSegment(sketch, "E850", {"start": v(6.67, -11.97) * mm, "end": v(6.84, -11.89) * mm});
            skLineSegment(sketch, "E851", {"start": v(6.84, -11.89) * mm, "end": v(7.03, -11.8) * mm});
            skLineSegment(sketch, "E852", {"start": v(7.03, -11.8) * mm, "end": v(7.2, -11.7) * mm});
            skLineSegment(sketch, "E853", {"start": v(7.2, -11.7) * mm, "end": v(7.21, -11.7) * mm});
            skLineSegment(sketch, "E854", {"start": v(7.21, -11.7) * mm, "end": v(7.23, -11.7) * mm});
            skLineSegment(sketch, "E855", {"start": v(7.23, -11.7) * mm, "end": v(7.24, -11.7) * mm});
            skLineSegment(sketch, "E856", {"start": v(7.24, -11.7) * mm, "end": v(7.26, -11.71) * mm});
            skLineSegment(sketch, "E857", {"start": v(7.26, -11.71) * mm, "end": v(7.27, -11.72) * mm});
            skLineSegment(sketch, "E858", {"start": v(7.27, -11.72) * mm, "end": v(7.3, -11.74) * mm});
            skLineSegment(sketch, "E859", {"start": v(7.3, -11.74) * mm, "end": v(7.31, -11.76) * mm});
            skLineSegment(sketch, "E860", {"start": v(7.31, -11.76) * mm, "end": v(7.33, -11.78) * mm});
            skLineSegment(sketch, "E861", {"start": v(7.33, -11.78) * mm, "end": v(7.35, -11.8) * mm});
            skLineSegment(sketch, "E862", {"start": v(7.35, -11.8) * mm, "end": v(7.37, -11.82) * mm});
            skLineSegment(sketch, "E863", {"start": v(7.37, -11.82) * mm, "end": v(7.4, -11.85) * mm});
            skLineSegment(sketch, "E864", {"start": v(7.4, -11.85) * mm, "end": v(7.42, -11.88) * mm});
            skLineSegment(sketch, "E865", {"start": v(7.42, -11.88) * mm, "end": v(7.45, -11.92) * mm});
            skLineSegment(sketch, "E866", {"start": v(7.45, -11.92) * mm, "end": v(7.48, -11.95) * mm});
            skLineSegment(sketch, "E867", {"start": v(7.48, -11.95) * mm, "end": v(7.52, -12) * mm});
            skLineSegment(sketch, "E868", {"start": v(7.52, -12) * mm, "end": v(7.56, -12.03) * mm});
            skLineSegment(sketch, "E869", {"start": v(7.56, -12.03) * mm, "end": v(7.6, -12.07) * mm});
            skLineSegment(sketch, "E870", {"start": v(7.6, -12.07) * mm, "end": v(7.65, -12.12) * mm});
            skLineSegment(sketch, "E871", {"start": v(7.65, -12.12) * mm, "end": v(7.7, -12.16) * mm});
            skLineSegment(sketch, "E872", {"start": v(7.7, -12.16) * mm, "end": v(7.75, -12.2) * mm});
            skLineSegment(sketch, "E873", {"start": v(7.75, -12.2) * mm, "end": v(7.8, -12.26) * mm});
            skLineSegment(sketch, "E874", {"start": v(7.8, -12.26) * mm, "end": v(7.86, -12.3) * mm});
            skLineSegment(sketch, "E875", {"start": v(7.86, -12.3) * mm, "end": v(7.92, -12.36) * mm});
            skLineSegment(sketch, "E876", {"start": v(7.92, -12.36) * mm, "end": v(7.98, -12.4) * mm});
            skLineSegment(sketch, "E877", {"start": v(7.98, -12.4) * mm, "end": v(8.05, -12.46) * mm});
            skLineSegment(sketch, "E878", {"start": v(8.05, -12.46) * mm, "end": v(8.12, -12.51) * mm});
            skLineSegment(sketch, "E879", {"start": v(8.12, -12.51) * mm, "end": v(8.2, -12.57) * mm});
            skLineSegment(sketch, "E880", {"start": v(8.2, -12.57) * mm, "end": v(8.27, -12.62) * mm});
            skLineSegment(sketch, "E881", {"start": v(8.27, -12.62) * mm, "end": v(8.33, -12.66) * mm});
            skLineSegment(sketch, "E882", {"start": v(8.33, -12.66) * mm, "end": v(8.58, -12.53) * mm});
            skLineSegment(sketch, "E883", {"start": v(8.58, -12.53) * mm, "end": v(8.81, -12.36) * mm});
            skLineSegment(sketch, "E884", {"start": v(8.81, -12.36) * mm, "end": v(8.8, -12.3) * mm});
            skLineSegment(sketch, "E885", {"start": v(8.8, -12.3) * mm, "end": v(8.79, -12.2) * mm});
            skLineSegment(sketch, "E886", {"start": v(8.79, -12.2) * mm, "end": v(8.77, -12.11) * mm});
            skLineSegment(sketch, "E887", {"start": v(8.77, -12.11) * mm, "end": v(8.76, -12.03) * mm});
            skLineSegment(sketch, "E888", {"start": v(8.76, -12.03) * mm, "end": v(8.74, -11.94) * mm});
            skLineSegment(sketch, "E889", {"start": v(8.74, -11.94) * mm, "end": v(8.73, -11.86) * mm});
            skLineSegment(sketch, "E890", {"start": v(8.73, -11.86) * mm, "end": v(8.7, -11.78) * mm});
            skLineSegment(sketch, "E891", {"start": v(8.7, -11.78) * mm, "end": v(8.7, -11.71) * mm});
            skLineSegment(sketch, "E892", {"start": v(8.7, -11.71) * mm, "end": v(8.67, -11.64) * mm});
            skLineSegment(sketch, "E893", {"start": v(8.67, -11.64) * mm, "end": v(8.66, -11.57) * mm});
            skLineSegment(sketch, "E894", {"start": v(8.66, -11.57) * mm, "end": v(8.64, -11.51) * mm});
            skLineSegment(sketch, "E895", {"start": v(8.64, -11.51) * mm, "end": v(8.62, -11.45) * mm});
            skLineSegment(sketch, "E896", {"start": v(8.62, -11.45) * mm, "end": v(8.6, -11.4) * mm});
            skLineSegment(sketch, "E897", {"start": v(8.6, -11.4) * mm, "end": v(8.58, -11.34) * mm});
            skLineSegment(sketch, "E898", {"start": v(8.58, -11.34) * mm, "end": v(8.56, -11.3) * mm});
            skLineSegment(sketch, "E899", {"start": v(8.56, -11.3) * mm, "end": v(8.55, -11.24) * mm});
            skLineSegment(sketch, "E900", {"start": v(8.55, -11.24) * mm, "end": v(8.53, -11.2) * mm});
            skLineSegment(sketch, "E901", {"start": v(8.53, -11.2) * mm, "end": v(8.51, -11.16) * mm});
            skLineSegment(sketch, "E902", {"start": v(8.51, -11.16) * mm, "end": v(8.5, -11.12) * mm});
            skLineSegment(sketch, "E903", {"start": v(8.5, -11.12) * mm, "end": v(8.49, -11.1) * mm});
            skLineSegment(sketch, "E904", {"start": v(8.49, -11.1) * mm, "end": v(8.48, -11.08) * mm});
            skLineSegment(sketch, "E905", {"start": v(8.48, -11.08) * mm, "end": v(8.47, -11.05) * mm});
            skLineSegment(sketch, "E906", {"start": v(8.47, -11.05) * mm, "end": v(8.46, -11.02) * mm});
            skLineSegment(sketch, "E907", {"start": v(8.46, -11.02) * mm, "end": v(8.45, -11) * mm});
            skLineSegment(sketch, "E908", {"start": v(8.45, -11) * mm, "end": v(8.45, -10.98) * mm});
            skLineSegment(sketch, "E909", {"start": v(8.45, -10.98) * mm, "end": v(8.45, -10.96) * mm});
            skLineSegment(sketch, "E910", {"start": v(8.45, -10.96) * mm, "end": v(8.45, -10.95) * mm});
            skLineSegment(sketch, "E911", {"start": v(8.45, -10.95) * mm, "end": v(8.46, -10.94) * mm});
            skLineSegment(sketch, "E912", {"start": v(8.46, -10.94) * mm, "end": v(8.47, -10.93) * mm});
            skLineSegment(sketch, "E913", {"start": v(8.47, -10.93) * mm, "end": v(8.63, -10.81) * mm});
            skLineSegment(sketch, "E914", {"start": v(8.63, -10.81) * mm, "end": v(8.8, -10.7) * mm});
            skLineSegment(sketch, "E915", {"start": v(8.8, -10.7) * mm, "end": v(8.95, -10.57) * mm});
            skLineSegment(sketch, "E916", {"start": v(8.95, -10.57) * mm, "end": v(8.96, -10.57) * mm});
            skLineSegment(sketch, "E917", {"start": v(8.96, -10.57) * mm, "end": v(8.98, -10.57) * mm});
            skLineSegment(sketch, "E918", {"start": v(8.98, -10.57) * mm, "end": v(9, -10.57) * mm});
            skLineSegment(sketch, "E919", {"start": v(9, -10.57) * mm, "end": v(9, -10.58) * mm});
            skLineSegment(sketch, "E920", {"start": v(9, -10.58) * mm, "end": v(9.03, -10.58) * mm});
            skLineSegment(sketch, "E921", {"start": v(9.03, -10.58) * mm, "end": v(9.05, -10.6) * mm});
            skLineSegment(sketch, "E922", {"start": v(9.05, -10.6) * mm, "end": v(9.07, -10.6) * mm});
            skLineSegment(sketch, "E923", {"start": v(9.07, -10.6) * mm, "end": v(9.1, -10.63) * mm});
            skLineSegment(sketch, "E924", {"start": v(9.1, -10.63) * mm, "end": v(9.12, -10.65) * mm});
            skLineSegment(sketch, "E925", {"start": v(9.12, -10.65) * mm, "end": v(9.13, -10.66) * mm});
            skLineSegment(sketch, "E926", {"start": v(9.13, -10.66) * mm, "end": v(9.16, -10.69) * mm});
            skLineSegment(sketch, "E927", {"start": v(9.16, -10.69) * mm, "end": v(9.2, -10.72) * mm});
            skLineSegment(sketch, "E928", {"start": v(9.2, -10.72) * mm, "end": v(9.23, -10.75) * mm});
            skLineSegment(sketch, "E929", {"start": v(9.23, -10.75) * mm, "end": v(9.27, -10.78) * mm});
            skLineSegment(sketch, "E930", {"start": v(9.27, -10.78) * mm, "end": v(9.31, -10.81) * mm});
            skLineSegment(sketch, "E931", {"start": v(9.31, -10.81) * mm, "end": v(9.36, -10.84) * mm});
            skLineSegment(sketch, "E932", {"start": v(9.36, -10.84) * mm, "end": v(9.4, -10.88) * mm});
            skLineSegment(sketch, "E933", {"start": v(9.4, -10.88) * mm, "end": v(9.46, -10.92) * mm});
            skLineSegment(sketch, "E934", {"start": v(9.46, -10.92) * mm, "end": v(9.51, -10.95) * mm});
            skLineSegment(sketch, "E935", {"start": v(9.51, -10.95) * mm, "end": v(9.57, -11) * mm});
            skLineSegment(sketch, "E936", {"start": v(9.57, -11) * mm, "end": v(9.63, -11.03) * mm});
            skLineSegment(sketch, "E937", {"start": v(9.63, -11.03) * mm, "end": v(9.7, -11.07) * mm});
            skLineSegment(sketch, "E938", {"start": v(9.7, -11.07) * mm, "end": v(9.76, -11.1) * mm});
            skLineSegment(sketch, "E939", {"start": v(9.76, -11.1) * mm, "end": v(9.83, -11.15) * mm});
            skLineSegment(sketch, "E940", {"start": v(9.83, -11.15) * mm, "end": v(9.9, -11.2) * mm});
            skLineSegment(sketch, "E941", {"start": v(9.9, -11.2) * mm, "end": v(9.99, -11.23) * mm});
            skLineSegment(sketch, "E942", {"start": v(9.99, -11.23) * mm, "end": v(10.07, -11.28) * mm});
            skLineSegment(sketch, "E943", {"start": v(10.07, -11.28) * mm, "end": v(10.16, -11.32) * mm});
            skLineSegment(sketch, "E944", {"start": v(10.16, -11.32) * mm, "end": v(10.21, -11.34) * mm});
            skLineSegment(sketch, "E945", {"start": v(10.21, -11.34) * mm, "end": v(10.44, -11.18) * mm});
            skLineSegment(sketch, "E946", {"start": v(10.44, -11.18) * mm, "end": v(10.64, -10.98) * mm});
            skLineSegment(sketch, "E947", {"start": v(10.64, -10.98) * mm, "end": v(10.63, -10.91) * mm});
            skLineSegment(sketch, "E948", {"start": v(10.63, -10.91) * mm, "end": v(10.6, -10.82) * mm});
            skLineSegment(sketch, "E949", {"start": v(10.6, -10.82) * mm, "end": v(10.57, -10.74) * mm});
            skLineSegment(sketch, "E950", {"start": v(10.57, -10.74) * mm, "end": v(10.54, -10.65) * mm});
            skLineSegment(sketch, "E951", {"start": v(10.54, -10.65) * mm, "end": v(10.51, -10.57) * mm});
            skLineSegment(sketch, "E952", {"start": v(10.51, -10.57) * mm, "end": v(10.48, -10.5) * mm});
            skLineSegment(sketch, "E953", {"start": v(10.48, -10.5) * mm, "end": v(10.45, -10.42) * mm});
            skLineSegment(sketch, "E954", {"start": v(10.45, -10.42) * mm, "end": v(10.42, -10.35) * mm});
            skLineSegment(sketch, "E955", {"start": v(10.42, -10.35) * mm, "end": v(10.4, -10.28) * mm});
            skLineSegment(sketch, "E956", {"start": v(10.4, -10.28) * mm, "end": v(10.37, -10.22) * mm});
            skLineSegment(sketch, "E957", {"start": v(10.37, -10.22) * mm, "end": v(10.34, -10.16) * mm});
            skLineSegment(sketch, "E958", {"start": v(10.34, -10.16) * mm, "end": v(10.31, -10.1) * mm});
            skLineSegment(sketch, "E959", {"start": v(10.31, -10.1) * mm, "end": v(10.28, -10.05) * mm});
            skLineSegment(sketch, "E960", {"start": v(10.28, -10.05) * mm, "end": v(10.26, -10) * mm});
            skLineSegment(sketch, "E961", {"start": v(10.26, -10) * mm, "end": v(10.23, -9.95) * mm});
            skLineSegment(sketch, "E962", {"start": v(10.23, -9.95) * mm, "end": v(10.2, -9.91) * mm});
            skLineSegment(sketch, "E963", {"start": v(10.2, -9.91) * mm, "end": v(10.18, -9.87) * mm});
            skLineSegment(sketch, "E964", {"start": v(10.18, -9.87) * mm, "end": v(10.16, -9.83) * mm});
            skLineSegment(sketch, "E965", {"start": v(10.16, -9.83) * mm, "end": v(10.14, -9.8) * mm});
            skLineSegment(sketch, "E966", {"start": v(10.14, -9.8) * mm, "end": v(10.13, -9.78) * mm});
            skLineSegment(sketch, "E967", {"start": v(10.13, -9.78) * mm, "end": v(10.11, -9.76) * mm});
            skLineSegment(sketch, "E968", {"start": v(10.11, -9.76) * mm, "end": v(10.1, -9.73) * mm});
            skLineSegment(sketch, "E969", {"start": v(10.1, -9.73) * mm, "end": v(10.09, -9.7) * mm});
            skLineSegment(sketch, "E970", {"start": v(10.09, -9.7) * mm, "end": v(10.08, -9.69) * mm});
            skLineSegment(sketch, "E971", {"start": v(10.08, -9.69) * mm, "end": v(10.07, -9.67) * mm});
            skLineSegment(sketch, "E972", {"start": v(10.07, -9.67) * mm, "end": v(10.07, -9.65) * mm});
            skLineSegment(sketch, "E973", {"start": v(10.07, -9.65) * mm, "end": v(10.07, -9.63) * mm});
            skLineSegment(sketch, "E974", {"start": v(10.07, -9.63) * mm, "end": v(10.07, -9.62) * mm});
            skLineSegment(sketch, "E975", {"start": v(10.07, -9.62) * mm, "end": v(10.08, -9.61) * mm});
            skLineSegment(sketch, "E976", {"start": v(10.08, -9.61) * mm, "end": v(10.22, -9.47) * mm});
            skLineSegment(sketch, "E977", {"start": v(10.22, -9.47) * mm, "end": v(10.37, -9.33) * mm});
            skLineSegment(sketch, "E978", {"start": v(10.37, -9.33) * mm, "end": v(10.5, -9.19) * mm});
            skLineSegment(sketch, "E979", {"start": v(10.5, -9.19) * mm, "end": v(10.52, -9.18) * mm});
            skLineSegment(sketch, "E980", {"start": v(10.52, -9.18) * mm, "end": v(10.53, -9.18) * mm});
            skLineSegment(sketch, "E981", {"start": v(10.53, -9.18) * mm, "end": v(10.54, -9.18) * mm});
            skLineSegment(sketch, "E982", {"start": v(10.54, -9.18) * mm, "end": v(10.56, -9.18) * mm});
            skLineSegment(sketch, "E983", {"start": v(10.56, -9.18) * mm, "end": v(10.58, -9.18) * mm});
            skLineSegment(sketch, "E984", {"start": v(10.58, -9.18) * mm, "end": v(10.6, -9.2) * mm});
            skLineSegment(sketch, "E985", {"start": v(10.6, -9.2) * mm, "end": v(10.63, -9.2) * mm});
            skLineSegment(sketch, "E986", {"start": v(10.63, -9.2) * mm, "end": v(10.65, -9.22) * mm});
            skLineSegment(sketch, "E987", {"start": v(10.65, -9.22) * mm, "end": v(10.68, -9.24) * mm});
            skLineSegment(sketch, "E988", {"start": v(10.68, -9.24) * mm, "end": v(10.7, -9.25) * mm});
            skLineSegment(sketch, "E989", {"start": v(10.7, -9.25) * mm, "end": v(10.73, -9.27) * mm});
            skLineSegment(sketch, "E990", {"start": v(10.73, -9.27) * mm, "end": v(10.77, -9.29) * mm});
            skLineSegment(sketch, "E991", {"start": v(10.77, -9.29) * mm, "end": v(10.8, -9.31) * mm});
            skLineSegment(sketch, "E992", {"start": v(10.8, -9.31) * mm, "end": v(10.85, -9.34) * mm});
            skLineSegment(sketch, "E993", {"start": v(10.85, -9.34) * mm, "end": v(10.9, -9.36) * mm});
            skLineSegment(sketch, "E994", {"start": v(10.9, -9.36) * mm, "end": v(10.95, -9.4) * mm});
            skLineSegment(sketch, "E995", {"start": v(10.95, -9.4) * mm, "end": v(11, -9.42) * mm});
            skLineSegment(sketch, "E996", {"start": v(11, -9.42) * mm, "end": v(11.05, -9.44) * mm});
            skLineSegment(sketch, "E997", {"start": v(11.05, -9.44) * mm, "end": v(11.11, -9.47) * mm});
            skLineSegment(sketch, "E998", {"start": v(11.11, -9.47) * mm, "end": v(11.18, -9.5) * mm});
            skLineSegment(sketch, "E999", {"start": v(11.18, -9.5) * mm, "end": v(11.24, -9.53) * mm});
            skLineSegment(sketch, "E1000", {"start": v(11.24, -9.53) * mm, "end": v(11.31, -9.56) * mm});
            skLineSegment(sketch, "E1001", {"start": v(11.31, -9.56) * mm, "end": v(11.39, -9.59) * mm});
            skLineSegment(sketch, "E1002", {"start": v(11.39, -9.59) * mm, "end": v(11.47, -9.62) * mm});
            skLineSegment(sketch, "E1003", {"start": v(11.47, -9.62) * mm, "end": v(11.55, -9.65) * mm});
            skLineSegment(sketch, "E1004", {"start": v(11.55, -9.65) * mm, "end": v(11.63, -9.68) * mm});
            skLineSegment(sketch, "E1005", {"start": v(11.63, -9.68) * mm, "end": v(11.72, -9.7) * mm});
            skLineSegment(sketch, "E1006", {"start": v(11.72, -9.7) * mm, "end": v(11.8, -9.73) * mm});
            skLineSegment(sketch, "E1007", {"start": v(11.8, -9.73) * mm, "end": v(11.87, -9.75) * mm});
            skLineSegment(sketch, "E1008", {"start": v(11.87, -9.75) * mm, "end": v(12.07, -9.55) * mm});
            skLineSegment(sketch, "E1009", {"start": v(12.07, -9.55) * mm, "end": v(12.24, -9.32) * mm});
            skLineSegment(sketch, "E1010", {"start": v(12.24, -9.32) * mm, "end": v(12.21, -9.26) * mm});
            skLineSegment(sketch, "E1011", {"start": v(12.21, -9.26) * mm, "end": v(12.17, -9.18) * mm});
            skLineSegment(sketch, "E1012", {"start": v(12.17, -9.18) * mm, "end": v(12.13, -9.1) * mm});
            skLineSegment(sketch, "E1013", {"start": v(12.13, -9.1) * mm, "end": v(12.09, -9.01) * mm});
            skLineSegment(sketch, "E1014", {"start": v(12.09, -9.01) * mm, "end": v(12.04, -8.94) * mm});
            skLineSegment(sketch, "E1015", {"start": v(12.04, -8.94) * mm, "end": v(12, -8.87) * mm});
            skLineSegment(sketch, "E1016", {"start": v(12, -8.87) * mm, "end": v(11.96, -8.8) * mm});
            skLineSegment(sketch, "E1017", {"start": v(11.96, -8.8) * mm, "end": v(11.92, -8.74) * mm});
            skLineSegment(sketch, "E1018", {"start": v(11.92, -8.74) * mm, "end": v(11.88, -8.67) * mm});
            skLineSegment(sketch, "E1019", {"start": v(11.88, -8.67) * mm, "end": v(11.85, -8.62) * mm});
            skLineSegment(sketch, "E1020", {"start": v(11.85, -8.62) * mm, "end": v(11.8, -8.56) * mm});
            skLineSegment(sketch, "E1021", {"start": v(11.8, -8.56) * mm, "end": v(11.77, -8.5) * mm});
            skLineSegment(sketch, "E1022", {"start": v(11.77, -8.5) * mm, "end": v(11.74, -8.46) * mm});
            skLineSegment(sketch, "E1023", {"start": v(11.74, -8.46) * mm, "end": v(11.7, -8.42) * mm});
            skLineSegment(sketch, "E1024", {"start": v(11.7, -8.42) * mm, "end": v(11.67, -8.37) * mm});
            skLineSegment(sketch, "E1025", {"start": v(11.67, -8.37) * mm, "end": v(11.64, -8.34) * mm});
            skLineSegment(sketch, "E1026", {"start": v(11.64, -8.34) * mm, "end": v(11.61, -8.3) * mm});
            skLineSegment(sketch, "E1027", {"start": v(11.61, -8.3) * mm, "end": v(11.58, -8.27) * mm});
            skLineSegment(sketch, "E1028", {"start": v(11.58, -8.27) * mm, "end": v(11.56, -8.24) * mm});
            skLineSegment(sketch, "E1029", {"start": v(11.56, -8.24) * mm, "end": v(11.54, -8.22) * mm});
            skLineSegment(sketch, "E1030", {"start": v(11.54, -8.22) * mm, "end": v(11.52, -8.2) * mm});
            skLineSegment(sketch, "E1031", {"start": v(11.52, -8.2) * mm, "end": v(11.5, -8.17) * mm});
            skLineSegment(sketch, "E1032", {"start": v(11.5, -8.17) * mm, "end": v(11.49, -8.15) * mm});
            skLineSegment(sketch, "E1033", {"start": v(11.49, -8.15) * mm, "end": v(11.48, -8.13) * mm});
            skLineSegment(sketch, "E1034", {"start": v(11.48, -8.13) * mm, "end": v(11.47, -8.11) * mm});
            skLineSegment(sketch, "E1035", {"start": v(11.47, -8.11) * mm, "end": v(11.46, -8.1) * mm});
            skLineSegment(sketch, "E1036", {"start": v(11.46, -8.1) * mm, "end": v(11.46, -8.08) * mm});
            skLineSegment(sketch, "E1037", {"start": v(11.46, -8.08) * mm, "end": v(11.46, -8.07) * mm});
            skLineSegment(sketch, "E1038", {"start": v(11.46, -8.07) * mm, "end": v(11.47, -8.06) * mm});
            skLineSegment(sketch, "E1039", {"start": v(11.47, -8.06) * mm, "end": v(11.59, -7.9) * mm});
            skLineSegment(sketch, "E1040", {"start": v(11.59, -7.9) * mm, "end": v(11.7, -7.73) * mm});
            skLineSegment(sketch, "E1041", {"start": v(11.7, -7.73) * mm, "end": v(11.82, -7.57) * mm});
            skLineSegment(sketch, "E1042", {"start": v(11.82, -7.57) * mm, "end": v(11.83, -7.57) * mm});
            skLineSegment(sketch, "E1043", {"start": v(11.83, -7.57) * mm, "end": v(11.84, -7.56) * mm});
            skLineSegment(sketch, "E1044", {"start": v(11.84, -7.56) * mm, "end": v(11.86, -7.56) * mm});
            skLineSegment(sketch, "E1045", {"start": v(11.86, -7.56) * mm, "end": v(11.87, -7.56) * mm});
            skLineSegment(sketch, "E1046", {"start": v(11.87, -7.56) * mm, "end": v(11.9, -7.56) * mm});
            skLineSegment(sketch, "E1047", {"start": v(11.9, -7.56) * mm, "end": v(11.92, -7.56) * mm});
            skLineSegment(sketch, "E1048", {"start": v(11.92, -7.56) * mm, "end": v(11.94, -7.57) * mm});
            skLineSegment(sketch, "E1049", {"start": v(11.94, -7.57) * mm, "end": v(11.97, -7.58) * mm});
            skLineSegment(sketch, "E1050", {"start": v(11.97, -7.58) * mm, "end": v(12, -7.6) * mm});
            skLineSegment(sketch, "E1051", {"start": v(12, -7.6) * mm, "end": v(12.02, -7.6) * mm});
            skLineSegment(sketch, "E1052", {"start": v(12.02, -7.6) * mm, "end": v(12.05, -7.62) * mm});
            skLineSegment(sketch, "E1053", {"start": v(12.05, -7.62) * mm, "end": v(12.1, -7.63) * mm});
            skLineSegment(sketch, "E1054", {"start": v(12.1, -7.63) * mm, "end": v(12.14, -7.65) * mm});
            skLineSegment(sketch, "E1055", {"start": v(12.14, -7.65) * mm, "end": v(12.18, -7.67) * mm});
            skLineSegment(sketch, "E1056", {"start": v(12.18, -7.67) * mm, "end": v(12.23, -7.69) * mm});
            skLineSegment(sketch, "E1057", {"start": v(12.23, -7.69) * mm, "end": v(12.29, -7.7) * mm});
            skLineSegment(sketch, "E1058", {"start": v(12.29, -7.7) * mm, "end": v(12.34, -7.72) * mm});
            skLineSegment(sketch, "E1059", {"start": v(12.34, -7.72) * mm, "end": v(12.4, -7.74) * mm});
            skLineSegment(sketch, "E1060", {"start": v(12.4, -7.74) * mm, "end": v(12.47, -7.76) * mm});
            skLineSegment(sketch, "E1061", {"start": v(12.47, -7.76) * mm, "end": v(12.53, -7.78) * mm});
            skLineSegment(sketch, "E1062", {"start": v(12.53, -7.78) * mm, "end": v(12.6, -7.8) * mm});
            skLineSegment(sketch, "E1063", {"start": v(12.6, -7.8) * mm, "end": v(12.68, -7.82) * mm});
            skLineSegment(sketch, "E1064", {"start": v(12.68, -7.82) * mm, "end": v(12.76, -7.83) * mm});
            skLineSegment(sketch, "E1065", {"start": v(12.76, -7.83) * mm, "end": v(12.84, -7.85) * mm});
            skLineSegment(sketch, "E1066", {"start": v(12.84, -7.85) * mm, "end": v(12.92, -7.87) * mm});
            skLineSegment(sketch, "E1067", {"start": v(12.92, -7.87) * mm, "end": v(13, -7.88) * mm});
            skLineSegment(sketch, "E1068", {"start": v(13, -7.88) * mm, "end": v(13.1, -7.9) * mm});
            skLineSegment(sketch, "E1069", {"start": v(13.1, -7.9) * mm, "end": v(13.2, -7.9) * mm});
            skLineSegment(sketch, "E1070", {"start": v(13.2, -7.9) * mm, "end": v(13.26, -7.92) * mm});
            skLineSegment(sketch, "E1071", {"start": v(13.26, -7.92) * mm, "end": v(13.43, -7.69) * mm});
            skLineSegment(sketch, "E1072", {"start": v(13.43, -7.69) * mm, "end": v(13.55, -7.43) * mm});
            skLineSegment(sketch, "E1073", {"start": v(13.55, -7.43) * mm, "end": v(13.52, -7.38) * mm});
            skLineSegment(sketch, "E1074", {"start": v(13.52, -7.38) * mm, "end": v(13.46, -7.3) * mm});
            skLineSegment(sketch, "E1075", {"start": v(13.46, -7.3) * mm, "end": v(13.4, -7.23) * mm});
            skLineSegment(sketch, "E1076", {"start": v(13.4, -7.23) * mm, "end": v(13.36, -7.16) * mm});
            skLineSegment(sketch, "E1077", {"start": v(13.36, -7.16) * mm, "end": v(13.3, -7.09) * mm});
            skLineSegment(sketch, "E1078", {"start": v(13.3, -7.09) * mm, "end": v(13.25, -7.02) * mm});
            skLineSegment(sketch, "E1079", {"start": v(13.25, -7.02) * mm, "end": v(13.2, -6.96) * mm});
            skLineSegment(sketch, "E1080", {"start": v(13.2, -6.96) * mm, "end": v(13.15, -6.9) * mm});
            skLineSegment(sketch, "E1081", {"start": v(13.15, -6.9) * mm, "end": v(13.1, -6.85) * mm});
            skLineSegment(sketch, "E1082", {"start": v(13.1, -6.85) * mm, "end": v(13.06, -6.8) * mm});
            skLineSegment(sketch, "E1083", {"start": v(13.06, -6.8) * mm, "end": v(13.01, -6.75) * mm});
            skLineSegment(sketch, "E1084", {"start": v(13.01, -6.75) * mm, "end": v(12.97, -6.7) * mm});
            skLineSegment(sketch, "E1085", {"start": v(12.97, -6.7) * mm, "end": v(12.93, -6.66) * mm});
            skLineSegment(sketch, "E1086", {"start": v(12.93, -6.66) * mm, "end": v(12.89, -6.63) * mm});
            skLineSegment(sketch, "E1087", {"start": v(12.89, -6.63) * mm, "end": v(12.85, -6.59) * mm});
            skLineSegment(sketch, "E1088", {"start": v(12.85, -6.59) * mm, "end": v(12.8, -6.56) * mm});
            skLineSegment(sketch, "E1089", {"start": v(12.8, -6.56) * mm, "end": v(12.77, -6.52) * mm});
            skLineSegment(sketch, "E1090", {"start": v(12.77, -6.52) * mm, "end": v(12.74, -6.5) * mm});
            skLineSegment(sketch, "E1091", {"start": v(12.74, -6.5) * mm, "end": v(12.71, -6.47) * mm});
            skLineSegment(sketch, "E1092", {"start": v(12.71, -6.47) * mm, "end": v(12.7, -6.46) * mm});
            skLineSegment(sketch, "E1093", {"start": v(12.7, -6.46) * mm, "end": v(12.67, -6.44) * mm});
            skLineSegment(sketch, "E1094", {"start": v(12.67, -6.44) * mm, "end": v(12.65, -6.42) * mm});
            skLineSegment(sketch, "E1095", {"start": v(12.65, -6.42) * mm, "end": v(12.63, -6.4) * mm});
            skLineSegment(sketch, "E1096", {"start": v(12.63, -6.4) * mm, "end": v(12.62, -6.38) * mm});
            skLineSegment(sketch, "E1097", {"start": v(12.62, -6.38) * mm, "end": v(12.6, -6.36) * mm});
            skLineSegment(sketch, "E1098", {"start": v(12.6, -6.36) * mm, "end": v(12.6, -6.35) * mm});
            skLineSegment(sketch, "E1099", {"start": v(12.6, -6.35) * mm, "end": v(12.6, -6.33) * mm});
            skLineSegment(sketch, "E1100", {"start": v(12.6, -6.33) * mm, "end": v(12.6, -6.32) * mm});
            skLineSegment(sketch, "E1101", {"start": v(12.6, -6.32) * mm, "end": v(12.6, -6.3) * mm});
            skLineSegment(sketch, "E1102", {"start": v(12.6, -6.3) * mm, "end": v(12.69, -6.14) * mm});
            skLineSegment(sketch, "E1103", {"start": v(12.69, -6.14) * mm, "end": v(12.78, -5.95) * mm});
            skLineSegment(sketch, "E1104", {"start": v(12.78, -5.95) * mm, "end": v(12.87, -5.77) * mm});
            skLineSegment(sketch, "E1105", {"start": v(12.87, -5.77) * mm, "end": v(12.88, -5.77) * mm});
            skLineSegment(sketch, "E1106", {"start": v(12.88, -5.77) * mm, "end": v(12.89, -5.76) * mm});
            skLineSegment(sketch, "E1107", {"start": v(12.89, -5.76) * mm, "end": v(12.9, -5.75) * mm});
            skLineSegment(sketch, "E1108", {"start": v(12.9, -5.75) * mm, "end": v(12.92, -5.75) * mm});
            skLineSegment(sketch, "E1109", {"start": v(12.92, -5.75) * mm, "end": v(12.94, -5.75) * mm});
            skLineSegment(sketch, "E1110", {"start": v(12.94, -5.75) * mm, "end": v(12.96, -5.75) * mm});
            skLineSegment(sketch, "E1111", {"start": v(12.96, -5.75) * mm, "end": v(12.99, -5.75) * mm});
            skLineSegment(sketch, "E1112", {"start": v(12.99, -5.75) * mm, "end": v(13.02, -5.76) * mm});
            skLineSegment(sketch, "E1113", {"start": v(13.02, -5.76) * mm, "end": v(13.05, -5.77) * mm});
            skLineSegment(sketch, "E1114", {"start": v(13.05, -5.77) * mm, "end": v(13.07, -5.77) * mm});
            skLineSegment(sketch, "E1115", {"start": v(13.07, -5.77) * mm, "end": v(13.1, -5.78) * mm});
            skLineSegment(sketch, "E1116", {"start": v(13.1, -5.78) * mm, "end": v(13.15, -5.8) * mm});
            skLineSegment(sketch, "E1117", {"start": v(13.15, -5.8) * mm, "end": v(13.2, -5.8) * mm});
            skLineSegment(sketch, "E1118", {"start": v(13.2, -5.8) * mm, "end": v(13.24, -5.81) * mm});
            skLineSegment(sketch, "E1119", {"start": v(13.24, -5.81) * mm, "end": v(13.3, -5.82) * mm});
            skLineSegment(sketch, "E1120", {"start": v(13.3, -5.82) * mm, "end": v(13.35, -5.83) * mm});
            skLineSegment(sketch, "E1121", {"start": v(13.35, -5.83) * mm, "end": v(13.4, -5.84) * mm});
            skLineSegment(sketch, "E1122", {"start": v(13.4, -5.84) * mm, "end": v(13.47, -5.85) * mm});
            skLineSegment(sketch, "E1123", {"start": v(13.47, -5.85) * mm, "end": v(13.54, -5.86) * mm});
            skLineSegment(sketch, "E1124", {"start": v(13.54, -5.86) * mm, "end": v(13.6, -5.87) * mm});
            skLineSegment(sketch, "E1125", {"start": v(13.6, -5.87) * mm, "end": v(13.68, -5.87) * mm});
            skLineSegment(sketch, "E1126", {"start": v(13.68, -5.87) * mm, "end": v(13.75, -5.88) * mm});
            skLineSegment(sketch, "E1127", {"start": v(13.75, -5.88) * mm, "end": v(13.83, -5.88) * mm});
            skLineSegment(sketch, "E1128", {"start": v(13.83, -5.88) * mm, "end": v(13.91, -5.89) * mm});
            skLineSegment(sketch, "E1129", {"start": v(13.91, -5.89) * mm, "end": v(14, -5.9) * mm});
            skLineSegment(sketch, "E1130", {"start": v(14, -5.9) * mm, "end": v(14.09, -5.9) * mm});
            skLineSegment(sketch, "E1131", {"start": v(14.09, -5.9) * mm, "end": v(14.18, -5.9) * mm});
            skLineSegment(sketch, "E1132", {"start": v(14.18, -5.9) * mm, "end": v(14.28, -5.9) * mm});
            skLineSegment(sketch, "E1133", {"start": v(14.28, -5.9) * mm, "end": v(14.34, -5.89) * mm});
            skLineSegment(sketch, "E1134", {"start": v(14.34, -5.89) * mm, "end": v(14.47, -5.63) * mm});
            skLineSegment(sketch, "E1135", {"start": v(14.47, -5.63) * mm, "end": v(14.56, -5.36) * mm});
            skLineSegment(sketch, "E1136", {"start": v(14.56, -5.36) * mm, "end": v(14.51, -5.32) * mm});
            skLineSegment(sketch, "E1137", {"start": v(14.51, -5.32) * mm, "end": v(14.45, -5.25) * mm});
            skLineSegment(sketch, "E1138", {"start": v(14.45, -5.25) * mm, "end": v(14.38, -5.18) * mm});
            skLineSegment(sketch, "E1139", {"start": v(14.38, -5.18) * mm, "end": v(14.32, -5.12) * mm});
            skLineSegment(sketch, "E1140", {"start": v(14.32, -5.12) * mm, "end": v(14.26, -5.06) * mm});
            skLineSegment(sketch, "E1141", {"start": v(14.26, -5.06) * mm, "end": v(14.2, -5) * mm});
            skLineSegment(sketch, "E1142", {"start": v(14.2, -5) * mm, "end": v(14.14, -4.96) * mm});
            skLineSegment(sketch, "E1143", {"start": v(14.14, -4.96) * mm, "end": v(14.08, -4.9) * mm});
            skLineSegment(sketch, "E1144", {"start": v(14.08, -4.9) * mm, "end": v(14.02, -4.86) * mm});
            skLineSegment(sketch, "E1145", {"start": v(14.02, -4.86) * mm, "end": v(13.97, -4.82) * mm});
            skLineSegment(sketch, "E1146", {"start": v(13.97, -4.82) * mm, "end": v(13.92, -4.78) * mm});
            skLineSegment(sketch, "E1147", {"start": v(13.92, -4.78) * mm, "end": v(13.87, -4.74) * mm});
            skLineSegment(sketch, "E1148", {"start": v(13.87, -4.74) * mm, "end": v(13.82, -4.7) * mm});
            skLineSegment(sketch, "E1149", {"start": v(13.82, -4.7) * mm, "end": v(13.77, -4.67) * mm});
            skLineSegment(sketch, "E1150", {"start": v(13.77, -4.67) * mm, "end": v(13.73, -4.64) * mm});
            skLineSegment(sketch, "E1151", {"start": v(13.73, -4.64) * mm, "end": v(13.69, -4.61) * mm});
            skLineSegment(sketch, "E1152", {"start": v(13.69, -4.61) * mm, "end": v(13.65, -4.59) * mm});
            skLineSegment(sketch, "E1153", {"start": v(13.65, -4.59) * mm, "end": v(13.6, -4.57) * mm});
            skLineSegment(sketch, "E1154", {"start": v(13.6, -4.57) * mm, "end": v(13.58, -4.55) * mm});
            skLineSegment(sketch, "E1155", {"start": v(13.58, -4.55) * mm, "end": v(13.56, -4.54) * mm});
            skLineSegment(sketch, "E1156", {"start": v(13.56, -4.54) * mm, "end": v(13.53, -4.52) * mm});
            skLineSegment(sketch, "E1157", {"start": v(13.53, -4.52) * mm, "end": v(13.5, -4.5) * mm});
            skLineSegment(sketch, "E1158", {"start": v(13.5, -4.5) * mm, "end": v(13.49, -4.49) * mm});
            skLineSegment(sketch, "E1159", {"start": v(13.49, -4.49) * mm, "end": v(13.47, -4.47) * mm});
            skLineSegment(sketch, "E1160", {"start": v(13.47, -4.47) * mm, "end": v(13.45, -4.46) * mm});
            skLineSegment(sketch, "E1161", {"start": v(13.45, -4.46) * mm, "end": v(13.44, -4.44) * mm});
            skLineSegment(sketch, "E1162", {"start": v(13.44, -4.44) * mm, "end": v(13.44, -4.43) * mm});
            skLineSegment(sketch, "E1163", {"start": v(13.44, -4.43) * mm, "end": v(13.44, -4.42) * mm});
            skLineSegment(sketch, "E1164", {"start": v(13.44, -4.42) * mm, "end": v(13.44, -4.4) * mm});
            skLineSegment(sketch, "E1165", {"start": v(13.44, -4.4) * mm, "end": v(13.5, -4.22) * mm});
            skLineSegment(sketch, "E1166", {"start": v(13.5, -4.22) * mm, "end": v(13.56, -4.02) * mm});
            skLineSegment(sketch, "E1167", {"start": v(13.56, -4.02) * mm, "end": v(13.62, -3.83) * mm});
            skLineSegment(sketch, "E1168", {"start": v(13.62, -3.83) * mm, "end": v(13.63, -3.82) * mm});
            skLineSegment(sketch, "E1169", {"start": v(13.63, -3.82) * mm, "end": v(13.64, -3.81) * mm});
            skLineSegment(sketch, "E1170", {"start": v(13.64, -3.81) * mm, "end": v(13.65, -3.8) * mm});
            skLineSegment(sketch, "E1171", {"start": v(13.65, -3.8) * mm, "end": v(13.67, -3.8) * mm});
            skLineSegment(sketch, "E1172", {"start": v(13.67, -3.8) * mm, "end": v(13.69, -3.8) * mm});
            skLineSegment(sketch, "E1173", {"start": v(13.69, -3.8) * mm, "end": v(13.71, -3.8) * mm});
            skLineSegment(sketch, "E1174", {"start": v(13.71, -3.8) * mm, "end": v(13.74, -3.8) * mm});
            skLineSegment(sketch, "E1175", {"start": v(13.74, -3.8) * mm, "end": v(13.77, -3.8) * mm});
            skLineSegment(sketch, "E1176", {"start": v(13.77, -3.8) * mm, "end": v(13.8, -3.8) * mm});
            skLineSegment(sketch, "E1177", {"start": v(13.8, -3.8) * mm, "end": v(13.82, -3.8) * mm});
            skLineSegment(sketch, "E1178", {"start": v(13.82, -3.8) * mm, "end": v(13.86, -3.8) * mm});
            skLineSegment(sketch, "E1179", {"start": v(13.86, -3.8) * mm, "end": v(13.9, -3.8) * mm});
            skLineSegment(sketch, "E1180", {"start": v(13.9, -3.8) * mm, "end": v(13.95, -3.8) * mm});
            skLineSegment(sketch, "E1181", {"start": v(13.95, -3.8) * mm, "end": v(14, -3.81) * mm});
            skLineSegment(sketch, "E1182", {"start": v(14, -3.81) * mm, "end": v(14.05, -3.81) * mm});
            skLineSegment(sketch, "E1183", {"start": v(14.05, -3.81) * mm, "end": v(14.1, -3.81) * mm});
            skLineSegment(sketch, "E1184", {"start": v(14.1, -3.81) * mm, "end": v(14.17, -3.81) * mm});
            skLineSegment(sketch, "E1185", {"start": v(14.17, -3.81) * mm, "end": v(14.23, -3.81) * mm});
            skLineSegment(sketch, "E1186", {"start": v(14.23, -3.81) * mm, "end": v(14.3, -3.81) * mm});
            skLineSegment(sketch, "E1187", {"start": v(14.3, -3.81) * mm, "end": v(14.36, -3.8) * mm});
            skLineSegment(sketch, "E1188", {"start": v(14.36, -3.8) * mm, "end": v(14.44, -3.8) * mm});
            skLineSegment(sketch, "E1189", {"start": v(14.44, -3.8) * mm, "end": v(14.51, -3.8) * mm});
            skLineSegment(sketch, "E1190", {"start": v(14.51, -3.8) * mm, "end": v(14.6, -3.8) * mm});
            skLineSegment(sketch, "E1191", {"start": v(14.6, -3.8) * mm, "end": v(14.67, -3.78) * mm});
            skLineSegment(sketch, "E1192", {"start": v(14.67, -3.78) * mm, "end": v(14.76, -3.77) * mm});
            skLineSegment(sketch, "E1193", {"start": v(14.76, -3.77) * mm, "end": v(14.85, -3.76) * mm});
            skLineSegment(sketch, "E1194", {"start": v(14.85, -3.76) * mm, "end": v(14.94, -3.74) * mm});
            skLineSegment(sketch, "E1195", {"start": v(14.94, -3.74) * mm, "end": v(15.03, -3.73) * mm});
            skLineSegment(sketch, "E1196", {"start": v(15.03, -3.73) * mm, "end": v(15.1, -3.72) * mm});
            skLineSegment(sketch, "E1197", {"start": v(15.1, -3.72) * mm, "end": v(15.18, -3.45) * mm});
            skLineSegment(sketch, "E1198", {"start": v(15.18, -3.45) * mm, "end": v(15.23, -3.16) * mm});
            skLineSegment(sketch, "E1199", {"start": v(15.23, -3.16) * mm, "end": v(15.18, -3.12) * mm});
            skLineSegment(sketch, "E1200", {"start": v(15.18, -3.12) * mm, "end": v(15.1, -3.07) * mm});
            skLineSegment(sketch, "E1201", {"start": v(15.1, -3.07) * mm, "end": v(15.02, -3.01) * mm});
            skLineSegment(sketch, "E1202", {"start": v(15.02, -3.01) * mm, "end": v(14.95, -2.96) * mm});
            skLineSegment(sketch, "E1203", {"start": v(14.95, -2.96) * mm, "end": v(14.88, -2.91) * mm});
            skLineSegment(sketch, "E1204", {"start": v(14.88, -2.91) * mm, "end": v(14.81, -2.87) * mm});
            skLineSegment(sketch, "E1205", {"start": v(14.81, -2.87) * mm, "end": v(14.75, -2.83) * mm});
            skLineSegment(sketch, "E1206", {"start": v(14.75, -2.83) * mm, "end": v(14.68, -2.79) * mm});
            skLineSegment(sketch, "E1207", {"start": v(14.68, -2.79) * mm, "end": v(14.62, -2.75) * mm});
            skLineSegment(sketch, "E1208", {"start": v(14.62, -2.75) * mm, "end": v(14.56, -2.72) * mm});
            skLineSegment(sketch, "E1209", {"start": v(14.56, -2.72) * mm, "end": v(14.5, -2.68) * mm});
            skLineSegment(sketch, "E1210", {"start": v(14.5, -2.68) * mm, "end": v(14.44, -2.65) * mm});
            skLineSegment(sketch, "E1211", {"start": v(14.44, -2.65) * mm, "end": v(14.4, -2.63) * mm});
            skLineSegment(sketch, "E1212", {"start": v(14.4, -2.63) * mm, "end": v(14.34, -2.6) * mm});
            skLineSegment(sketch, "E1213", {"start": v(14.34, -2.6) * mm, "end": v(14.3, -2.58) * mm});
            skLineSegment(sketch, "E1214", {"start": v(14.3, -2.58) * mm, "end": v(14.25, -2.56) * mm});
            skLineSegment(sketch, "E1215", {"start": v(14.25, -2.56) * mm, "end": v(14.2, -2.54) * mm});
            skLineSegment(sketch, "E1216", {"start": v(14.2, -2.54) * mm, "end": v(14.16, -2.52) * mm});
            skLineSegment(sketch, "E1217", {"start": v(14.16, -2.52) * mm, "end": v(14.13, -2.5) * mm});
            skLineSegment(sketch, "E1218", {"start": v(14.13, -2.5) * mm, "end": v(14.1, -2.5) * mm});
            skLineSegment(sketch, "E1219", {"start": v(14.1, -2.5) * mm, "end": v(14.08, -2.5) * mm});
            skLineSegment(sketch, "E1220", {"start": v(14.08, -2.5) * mm, "end": v(14.05, -2.48) * mm});
            skLineSegment(sketch, "E1221", {"start": v(14.05, -2.48) * mm, "end": v(14.03, -2.47) * mm});
            skLineSegment(sketch, "E1222", {"start": v(14.03, -2.47) * mm, "end": v(14, -2.45) * mm});
            skLineSegment(sketch, "E1223", {"start": v(14, -2.45) * mm, "end": v(14, -2.44) * mm});
            skLineSegment(sketch, "E1224", {"start": v(14, -2.44) * mm, "end": v(13.98, -2.43) * mm});
            skLineSegment(sketch, "E1225", {"start": v(13.98, -2.43) * mm, "end": v(13.97, -2.41) * mm});
            skLineSegment(sketch, "E1226", {"start": v(13.97, -2.41) * mm, "end": v(13.97, -2.4) * mm});
            skLineSegment(sketch, "E1227", {"start": v(13.97, -2.4) * mm, "end": v(13.97, -2.4) * mm});
            skLineSegment(sketch, "E1228", {"start": v(13.97, -2.4) * mm, "end": v(14, -2.2) * mm});
            skLineSegment(sketch, "E1229", {"start": v(14, -2.2) * mm, "end": v(14.03, -2) * mm});
            skLineSegment(sketch, "E1230", {"start": v(14.03, -2) * mm, "end": v(14.06, -1.8) * mm});
            skLineSegment(sketch, "E1231", {"start": v(14.06, -1.8) * mm, "end": v(14.07, -1.79) * mm});
            skLineSegment(sketch, "E1232", {"start": v(14.07, -1.79) * mm, "end": v(14.07, -1.78) * mm});
            skLineSegment(sketch, "E1233", {"start": v(14.07, -1.78) * mm, "end": v(14.09, -1.77) * mm});
            skLineSegment(sketch, "E1234", {"start": v(14.09, -1.77) * mm, "end": v(14.1, -1.76) * mm});
            skLineSegment(sketch, "E1235", {"start": v(14.1, -1.76) * mm, "end": v(14.12, -1.75) * mm});
            skLineSegment(sketch, "E1236", {"start": v(14.12, -1.75) * mm, "end": v(14.14, -1.75) * mm});
            skLineSegment(sketch, "E1237", {"start": v(14.14, -1.75) * mm, "end": v(14.17, -1.74) * mm});
            skLineSegment(sketch, "E1238", {"start": v(14.17, -1.74) * mm, "end": v(14.2, -1.74) * mm});
            skLineSegment(sketch, "E1239", {"start": v(14.2, -1.74) * mm, "end": v(14.23, -1.74) * mm});
            skLineSegment(sketch, "E1240", {"start": v(14.23, -1.74) * mm, "end": v(14.25, -1.73) * mm});
            skLineSegment(sketch, "E1241", {"start": v(14.25, -1.73) * mm, "end": v(14.3, -1.73) * mm});
            skLineSegment(sketch, "E1242", {"start": v(14.3, -1.73) * mm, "end": v(14.33, -1.73) * mm});
            skLineSegment(sketch, "E1243", {"start": v(14.33, -1.73) * mm, "end": v(14.38, -1.72) * mm});
            skLineSegment(sketch, "E1244", {"start": v(14.38, -1.72) * mm, "end": v(14.43, -1.72) * mm});
            skLineSegment(sketch, "E1245", {"start": v(14.43, -1.72) * mm, "end": v(14.48, -1.71) * mm});
            skLineSegment(sketch, "E1246", {"start": v(14.48, -1.71) * mm, "end": v(14.54, -1.7) * mm});
            skLineSegment(sketch, "E1247", {"start": v(14.54, -1.7) * mm, "end": v(14.6, -1.7) * mm});
            skLineSegment(sketch, "E1248", {"start": v(14.6, -1.7) * mm, "end": v(14.66, -1.68) * mm});
            skLineSegment(sketch, "E1249", {"start": v(14.66, -1.68) * mm, "end": v(14.72, -1.67) * mm});
            skLineSegment(sketch, "E1250", {"start": v(14.72, -1.67) * mm, "end": v(14.8, -1.66) * mm});
            skLineSegment(sketch, "E1251", {"start": v(14.8, -1.66) * mm, "end": v(14.86, -1.64) * mm});
            skLineSegment(sketch, "E1252", {"start": v(14.86, -1.64) * mm, "end": v(14.94, -1.62) * mm});
            skLineSegment(sketch, "E1253", {"start": v(14.94, -1.62) * mm, "end": v(15.01, -1.6) * mm});
            skLineSegment(sketch, "E1254", {"start": v(15.01, -1.6) * mm, "end": v(15.1, -1.58) * mm});
            skLineSegment(sketch, "E1255", {"start": v(15.1, -1.58) * mm, "end": v(15.17, -1.56) * mm});
            skLineSegment(sketch, "E1256", {"start": v(15.17, -1.56) * mm, "end": v(15.26, -1.53) * mm});
            skLineSegment(sketch, "E1257", {"start": v(15.26, -1.53) * mm, "end": v(15.35, -1.5) * mm});
            skLineSegment(sketch, "E1258", {"start": v(15.35, -1.5) * mm, "end": v(15.44, -1.47) * mm});
            skLineSegment(sketch, "E1259", {"start": v(15.44, -1.47) * mm, "end": v(15.5, -1.45) * mm});
            skLineSegment(sketch, "E1260", {"start": v(15.5, -1.45) * mm, "end": v(15.54, -1.17) * mm});
            skLineSegment(sketch, "E1261", {"start": v(15.54, -1.17) * mm, "end": v(15.54, -0.89) * mm});
            skLineSegment(sketch, "E1262", {"start": v(15.54, -0.89) * mm, "end": v(15.49, -0.86) * mm});
            skLineSegment(sketch, "E1263", {"start": v(15.49, -0.86) * mm, "end": v(15.4, -0.81) * mm});
            skLineSegment(sketch, "E1264", {"start": v(15.4, -0.81) * mm, "end": v(15.32, -0.77) * mm});
            skLineSegment(sketch, "E1265", {"start": v(15.32, -0.77) * mm, "end": v(15.24, -0.73) * mm});
            skLineSegment(sketch, "E1266", {"start": v(15.24, -0.73) * mm, "end": v(15.16, -0.7) * mm});
            skLineSegment(sketch, "E1267", {"start": v(15.16, -0.7) * mm, "end": v(15.09, -0.66) * mm});
            skLineSegment(sketch, "E1268", {"start": v(15.09, -0.66) * mm, "end": v(15.01, -0.63) * mm});
            skLineSegment(sketch, "E1269", {"start": v(15.01, -0.63) * mm, "end": v(14.94, -0.6) * mm});
            skLineSegment(sketch, "E1270", {"start": v(14.94, -0.6) * mm, "end": v(14.88, -0.57) * mm});
            skLineSegment(sketch, "E1271", {"start": v(14.88, -0.57) * mm, "end": v(14.81, -0.55) * mm});
            skLineSegment(sketch, "E1272", {"start": v(14.81, -0.55) * mm, "end": v(14.75, -0.53) * mm});
            skLineSegment(sketch, "E1273", {"start": v(14.75, -0.53) * mm, "end": v(14.69, -0.5) * mm});
            skLineSegment(sketch, "E1274", {"start": v(14.69, -0.5) * mm, "end": v(14.63, -0.49) * mm});
            skLineSegment(sketch, "E1275", {"start": v(14.63, -0.49) * mm, "end": v(14.58, -0.47) * mm});
            skLineSegment(sketch, "E1276", {"start": v(14.58, -0.47) * mm, "end": v(14.53, -0.46) * mm});
            skLineSegment(sketch, "E1277", {"start": v(14.53, -0.46) * mm, "end": v(14.48, -0.44) * mm});
            skLineSegment(sketch, "E1278", {"start": v(14.48, -0.44) * mm, "end": v(14.44, -0.43) * mm});
            skLineSegment(sketch, "E1279", {"start": v(14.44, -0.43) * mm, "end": v(14.4, -0.42) * mm});
            skLineSegment(sketch, "E1280", {"start": v(14.4, -0.42) * mm, "end": v(14.35, -0.41) * mm});
            skLineSegment(sketch, "E1281", {"start": v(14.35, -0.41) * mm, "end": v(14.34, -0.4) * mm});
            skLineSegment(sketch, "E1282", {"start": v(14.34, -0.4) * mm, "end": v(14.3, -0.4) * mm});
            skLineSegment(sketch, "E1283", {"start": v(14.3, -0.4) * mm, "end": v(14.28, -0.4) * mm});
            skLineSegment(sketch, "E1284", {"start": v(14.28, -0.4) * mm, "end": v(14.25, -0.38) * mm});
            skLineSegment(sketch, "E1285", {"start": v(14.25, -0.38) * mm, "end": v(14.23, -0.37) * mm});
            skLineSegment(sketch, "E1286", {"start": v(14.23, -0.37) * mm, "end": v(14.21, -0.36) * mm});
            skLineSegment(sketch, "E1287", {"start": v(14.21, -0.36) * mm, "end": v(14.2, -0.35) * mm});
            skLineSegment(sketch, "E1288", {"start": v(14.2, -0.35) * mm, "end": v(14.19, -0.34) * mm});
            skLineSegment(sketch, "E1289", {"start": v(14.19, -0.34) * mm, "end": v(14.18, -0.33) * mm});
            skLineSegment(sketch, "E1290", {"start": v(14.18, -0.33) * mm, "end": v(14.18, -0.32) * mm});
            skLineSegment(sketch, "E1291", {"start": v(14.18, -0.32) * mm, "end": v(14.18, -0.12) * mm});
            skLineSegment(sketch, "E1292", {"start": v(14.18, -0.12) * mm, "end": v(14.18, 0.08) * mm});
            skLineSegment(sketch, "E1293", {"start": v(14.18, 0.08) * mm, "end": v(14.18, 0.28) * mm});
            skLineSegment(sketch, "E1294", {"start": v(14.18, 0.28) * mm, "end": v(14.18, 0.3) * mm});
            skLineSegment(sketch, "E1295", {"start": v(14.18, 0.3) * mm, "end": v(14.19, 0.3) * mm});
            skLineSegment(sketch, "E1296", {"start": v(14.19, 0.3) * mm, "end": v(14.2, 0.31) * mm});
            skLineSegment(sketch, "E1297", {"start": v(14.2, 0.31) * mm, "end": v(14.21, 0.32) * mm});
            skLineSegment(sketch, "E1298", {"start": v(14.21, 0.32) * mm, "end": v(14.23, 0.33) * mm});
            skLineSegment(sketch, "E1299", {"start": v(14.23, 0.33) * mm, "end": v(14.25, 0.34) * mm});
            skLineSegment(sketch, "E1300", {"start": v(14.25, 0.34) * mm, "end": v(14.28, 0.35) * mm});
            skLineSegment(sketch, "E1301", {"start": v(14.28, 0.35) * mm, "end": v(14.3, 0.36) * mm});
            skLineSegment(sketch, "E1302", {"start": v(14.3, 0.36) * mm, "end": v(14.34, 0.37) * mm});
            skLineSegment(sketch, "E1303", {"start": v(14.34, 0.37) * mm, "end": v(14.35, 0.37) * mm});
            skLineSegment(sketch, "E1304", {"start": v(14.35, 0.37) * mm, "end": v(14.4, 0.38) * mm});
            skLineSegment(sketch, "E1305", {"start": v(14.4, 0.38) * mm, "end": v(14.44, 0.4) * mm});
            skLineSegment(sketch, "E1306", {"start": v(14.44, 0.4) * mm, "end": v(14.48, 0.4) * mm});
            skLineSegment(sketch, "E1307", {"start": v(14.48, 0.4) * mm, "end": v(14.53, 0.42) * mm});
            skLineSegment(sketch, "E1308", {"start": v(14.53, 0.42) * mm, "end": v(14.58, 0.43) * mm});
            skLineSegment(sketch, "E1309", {"start": v(14.58, 0.43) * mm, "end": v(14.63, 0.45) * mm});
            skLineSegment(sketch, "E1310", {"start": v(14.63, 0.45) * mm, "end": v(14.69, 0.47) * mm});
            skLineSegment(sketch, "E1311", {"start": v(14.69, 0.47) * mm, "end": v(14.75, 0.49) * mm});
            skLineSegment(sketch, "E1312", {"start": v(14.75, 0.49) * mm, "end": v(14.81, 0.5) * mm});
            skLineSegment(sketch, "E1313", {"start": v(14.81, 0.5) * mm, "end": v(14.88, 0.53) * mm});
            skLineSegment(sketch, "E1314", {"start": v(14.88, 0.53) * mm, "end": v(14.94, 0.56) * mm});
            skLineSegment(sketch, "E1315", {"start": v(14.94, 0.56) * mm, "end": v(15.01, 0.59) * mm});
            skLineSegment(sketch, "E1316", {"start": v(15.01, 0.59) * mm, "end": v(15.09, 0.62) * mm});
            skLineSegment(sketch, "E1317", {"start": v(15.09, 0.62) * mm, "end": v(15.16, 0.65) * mm});
            skLineSegment(sketch, "E1318", {"start": v(15.16, 0.65) * mm, "end": v(15.24, 0.7) * mm});
            skLineSegment(sketch, "E1319", {"start": v(15.24, 0.7) * mm, "end": v(15.32, 0.73) * mm});
            skLineSegment(sketch, "E1320", {"start": v(15.32, 0.73) * mm, "end": v(15.4, 0.77) * mm});
            skLineSegment(sketch, "E1321", {"start": v(15.4, 0.77) * mm, "end": v(15.49, 0.82) * mm});
            skLineSegment(sketch, "E1322", {"start": v(15.49, 0.82) * mm, "end": v(15.54, 0.85) * mm});
            skLineSegment(sketch, "E1323", {"start": v(15.54, 0.85) * mm, "end": v(15.54, 1.13) * mm});
            skLineSegment(sketch, "E1324", {"start": v(15.54, 1.13) * mm, "end": v(15.5, 1.41) * mm});
            skLineSegment(sketch, "E1325", {"start": v(15.5, 1.41) * mm, "end": v(15.44, 1.43) * mm});
            skLineSegment(sketch, "E1326", {"start": v(15.44, 1.43) * mm, "end": v(15.35, 1.47) * mm});
            skLineSegment(sketch, "E1327", {"start": v(15.35, 1.47) * mm, "end": v(15.26, 1.5) * mm});
            skLineSegment(sketch, "E1328", {"start": v(15.26, 1.5) * mm, "end": v(15.17, 1.52) * mm});
            skLineSegment(sketch, "E1329", {"start": v(15.17, 1.52) * mm, "end": v(15.1, 1.54) * mm});
            skLineSegment(sketch, "E1330", {"start": v(15.1, 1.54) * mm, "end": v(15.01, 1.57) * mm});
            skLineSegment(sketch, "E1331", {"start": v(15.01, 1.57) * mm, "end": v(14.94, 1.58) * mm});
            skLineSegment(sketch, "E1332", {"start": v(14.94, 1.58) * mm, "end": v(14.86, 1.6) * mm});
            skLineSegment(sketch, "E1333", {"start": v(14.86, 1.6) * mm, "end": v(14.8, 1.62) * mm});
            skLineSegment(sketch, "E1334", {"start": v(14.8, 1.62) * mm, "end": v(14.72, 1.63) * mm});
            skLineSegment(sketch, "E1335", {"start": v(14.72, 1.63) * mm, "end": v(14.66, 1.64) * mm});
            skLineSegment(sketch, "E1336", {"start": v(14.66, 1.64) * mm, "end": v(14.6, 1.66) * mm});
            skLineSegment(sketch, "E1337", {"start": v(14.6, 1.66) * mm, "end": v(14.54, 1.66) * mm});
            skLineSegment(sketch, "E1338", {"start": v(14.54, 1.66) * mm, "end": v(14.48, 1.67) * mm});
            skLineSegment(sketch, "E1339", {"start": v(14.48, 1.67) * mm, "end": v(14.43, 1.68) * mm});
            skLineSegment(sketch, "E1340", {"start": v(14.43, 1.68) * mm, "end": v(14.38, 1.68) * mm});
            skLineSegment(sketch, "E1341", {"start": v(14.38, 1.68) * mm, "end": v(14.33, 1.69) * mm});
            skLineSegment(sketch, "E1342", {"start": v(14.33, 1.69) * mm, "end": v(14.3, 1.7) * mm});
            skLineSegment(sketch, "E1343", {"start": v(14.3, 1.7) * mm, "end": v(14.25, 1.7) * mm});
            skLineSegment(sketch, "E1344", {"start": v(14.25, 1.7) * mm, "end": v(14.23, 1.7) * mm});
            skLineSegment(sketch, "E1345", {"start": v(14.23, 1.7) * mm, "end": v(14.2, 1.7) * mm});
            skLineSegment(sketch, "E1346", {"start": v(14.2, 1.7) * mm, "end": v(14.17, 1.7) * mm});
            skLineSegment(sketch, "E1347", {"start": v(14.17, 1.7) * mm, "end": v(14.14, 1.7) * mm});
            skLineSegment(sketch, "E1348", {"start": v(14.14, 1.7) * mm, "end": v(14.12, 1.71) * mm});
            skLineSegment(sketch, "E1349", {"start": v(14.12, 1.71) * mm, "end": v(14.1, 1.72) * mm});
            skLineSegment(sketch, "E1350", {"start": v(14.1, 1.72) * mm, "end": v(14.09, 1.73) * mm});
            skLineSegment(sketch, "E1351", {"start": v(14.09, 1.73) * mm, "end": v(14.07, 1.74) * mm});
            skLineSegment(sketch, "E1352", {"start": v(14.07, 1.74) * mm, "end": v(14.07, 1.75) * mm});
            skLineSegment(sketch, "E1353", {"start": v(14.07, 1.75) * mm, "end": v(14.06, 1.76) * mm});
            skLineSegment(sketch, "E1354", {"start": v(14.06, 1.76) * mm, "end": v(14.03, 1.95) * mm});
            skLineSegment(sketch, "E1355", {"start": v(14.03, 1.95) * mm, "end": v(14, 2.16) * mm});
            skLineSegment(sketch, "E1356", {"start": v(14, 2.16) * mm, "end": v(13.97, 2.35) * mm});
            skLineSegment(sketch, "E1357", {"start": v(13.97, 2.35) * mm, "end": v(13.97, 2.36) * mm});
            skLineSegment(sketch, "E1358", {"start": v(13.97, 2.36) * mm, "end": v(13.97, 2.38) * mm});
            skLineSegment(sketch, "E1359", {"start": v(13.97, 2.38) * mm, "end": v(13.98, 2.39) * mm});
            skLineSegment(sketch, "E1360", {"start": v(13.98, 2.39) * mm, "end": v(14, 2.4) * mm});
            skLineSegment(sketch, "E1361", {"start": v(14, 2.4) * mm, "end": v(14, 2.41) * mm});
            skLineSegment(sketch, "E1362", {"start": v(14, 2.41) * mm, "end": v(14.03, 2.43) * mm});
            skLineSegment(sketch, "E1363", {"start": v(14.03, 2.43) * mm, "end": v(14.05, 2.44) * mm});
            skLineSegment(sketch, "E1364", {"start": v(14.05, 2.44) * mm, "end": v(14.08, 2.45) * mm});
            skLineSegment(sketch, "E1365", {"start": v(14.08, 2.45) * mm, "end": v(14.1, 2.46) * mm});
            skLineSegment(sketch, "E1366", {"start": v(14.1, 2.46) * mm, "end": v(14.13, 2.47) * mm});
            skLineSegment(sketch, "E1367", {"start": v(14.13, 2.47) * mm, "end": v(14.16, 2.49) * mm});
            skLineSegment(sketch, "E1368", {"start": v(14.16, 2.49) * mm, "end": v(14.2, 2.5) * mm});
            skLineSegment(sketch, "E1369", {"start": v(14.2, 2.5) * mm, "end": v(14.25, 2.52) * mm});
            skLineSegment(sketch, "E1370", {"start": v(14.25, 2.52) * mm, "end": v(14.3, 2.54) * mm});
            skLineSegment(sketch, "E1371", {"start": v(14.3, 2.54) * mm, "end": v(14.34, 2.56) * mm});
            skLineSegment(sketch, "E1372", {"start": v(14.34, 2.56) * mm, "end": v(14.4, 2.59) * mm});
            skLineSegment(sketch, "E1373", {"start": v(14.4, 2.59) * mm, "end": v(14.44, 2.61) * mm});
            skLineSegment(sketch, "E1374", {"start": v(14.44, 2.61) * mm, "end": v(14.5, 2.64) * mm});
            skLineSegment(sketch, "E1375", {"start": v(14.5, 2.64) * mm, "end": v(14.56, 2.68) * mm});
            skLineSegment(sketch, "E1376", {"start": v(14.56, 2.68) * mm, "end": v(14.62, 2.71) * mm});
            skLineSegment(sketch, "E1377", {"start": v(14.62, 2.71) * mm, "end": v(14.68, 2.75) * mm});
            skLineSegment(sketch, "E1378", {"start": v(14.68, 2.75) * mm, "end": v(14.75, 2.79) * mm});
            skLineSegment(sketch, "E1379", {"start": v(14.75, 2.79) * mm, "end": v(14.81, 2.83) * mm});
            skLineSegment(sketch, "E1380", {"start": v(14.81, 2.83) * mm, "end": v(14.88, 2.87) * mm});
            skLineSegment(sketch, "E1381", {"start": v(14.88, 2.87) * mm, "end": v(14.95, 2.92) * mm});
            skLineSegment(sketch, "E1382", {"start": v(14.95, 2.92) * mm, "end": v(15.02, 2.97) * mm});
            skLineSegment(sketch, "E1383", {"start": v(15.02, 2.97) * mm, "end": v(15.1, 3.03) * mm});
            skLineSegment(sketch, "E1384", {"start": v(15.1, 3.03) * mm, "end": v(15.18, 3.09) * mm});
            skLineSegment(sketch, "E1385", {"start": v(15.18, 3.09) * mm, "end": v(15.23, 3.12) * mm});
            skLineSegment(sketch, "E1386", {"start": v(15.23, 3.12) * mm, "end": v(15.18, 3.4) * mm});
            skLineSegment(sketch, "E1387", {"start": v(15.18, 3.4) * mm, "end": v(15.1, 3.68) * mm});
            skLineSegment(sketch, "E1388", {"start": v(15.1, 3.68) * mm, "end": v(15.03, 3.69) * mm});
            skLineSegment(sketch, "E1389", {"start": v(15.03, 3.69) * mm, "end": v(14.94, 3.7) * mm});
            skLineSegment(sketch, "E1390", {"start": v(14.94, 3.7) * mm, "end": v(14.85, 3.72) * mm});
            skLineSegment(sketch, "E1391", {"start": v(14.85, 3.72) * mm, "end": v(14.76, 3.73) * mm});
            skLineSegment(sketch, "E1392", {"start": v(14.76, 3.73) * mm, "end": v(14.67, 3.74) * mm});
            skLineSegment(sketch, "E1393", {"start": v(14.67, 3.74) * mm, "end": v(14.6, 3.75) * mm});
            skLineSegment(sketch, "E1394", {"start": v(14.6, 3.75) * mm, "end": v(14.51, 3.76) * mm});
            skLineSegment(sketch, "E1395", {"start": v(14.51, 3.76) * mm, "end": v(14.44, 3.76) * mm});
            skLineSegment(sketch, "E1396", {"start": v(14.44, 3.76) * mm, "end": v(14.36, 3.77) * mm});
            skLineSegment(sketch, "E1397", {"start": v(14.36, 3.77) * mm, "end": v(14.3, 3.77) * mm});
            skLineSegment(sketch, "E1398", {"start": v(14.3, 3.77) * mm, "end": v(14.23, 3.77) * mm});
            skLineSegment(sketch, "E1399", {"start": v(14.23, 3.77) * mm, "end": v(14.17, 3.78) * mm});
            skLineSegment(sketch, "E1400", {"start": v(14.17, 3.78) * mm, "end": v(14.1, 3.78) * mm});
            skLineSegment(sketch, "E1401", {"start": v(14.1, 3.78) * mm, "end": v(14.05, 3.77) * mm});
            skLineSegment(sketch, "E1402", {"start": v(14.05, 3.77) * mm, "end": v(14, 3.77) * mm});
            skLineSegment(sketch, "E1403", {"start": v(14, 3.77) * mm, "end": v(13.95, 3.77) * mm});
            skLineSegment(sketch, "E1404", {"start": v(13.95, 3.77) * mm, "end": v(13.9, 3.77) * mm});
            skLineSegment(sketch, "E1405", {"start": v(13.9, 3.77) * mm, "end": v(13.86, 3.76) * mm});
            skLineSegment(sketch, "E1406", {"start": v(13.86, 3.76) * mm, "end": v(13.82, 3.76) * mm});
            skLineSegment(sketch, "E1407", {"start": v(13.82, 3.76) * mm, "end": v(13.8, 3.76) * mm});
            skLineSegment(sketch, "E1408", {"start": v(13.8, 3.76) * mm, "end": v(13.77, 3.76) * mm});
            skLineSegment(sketch, "E1409", {"start": v(13.77, 3.76) * mm, "end": v(13.74, 3.75) * mm});
            skLineSegment(sketch, "E1410", {"start": v(13.74, 3.75) * mm, "end": v(13.71, 3.76) * mm});
            skLineSegment(sketch, "E1411", {"start": v(13.71, 3.76) * mm, "end": v(13.69, 3.76) * mm});
            skLineSegment(sketch, "E1412", {"start": v(13.69, 3.76) * mm, "end": v(13.67, 3.76) * mm});
            skLineSegment(sketch, "E1413", {"start": v(13.67, 3.76) * mm, "end": v(13.65, 3.77) * mm});
            skLineSegment(sketch, "E1414", {"start": v(13.65, 3.77) * mm, "end": v(13.64, 3.78) * mm});
            skLineSegment(sketch, "E1415", {"start": v(13.64, 3.78) * mm, "end": v(13.63, 3.78) * mm});
            skLineSegment(sketch, "E1416", {"start": v(13.63, 3.78) * mm, "end": v(13.62, 3.8) * mm});
            skLineSegment(sketch, "E1417", {"start": v(13.62, 3.8) * mm, "end": v(13.56, 3.98) * mm});
            skLineSegment(sketch, "E1418", {"start": v(13.56, 3.98) * mm, "end": v(13.5, 4.18) * mm});
            skLineSegment(sketch, "E1419", {"start": v(13.5, 4.18) * mm, "end": v(13.44, 4.36) * mm});
            skLineSegment(sketch, "E1420", {"start": v(13.44, 4.36) * mm, "end": v(13.44, 4.38) * mm});
            skLineSegment(sketch, "E1421", {"start": v(13.44, 4.38) * mm, "end": v(13.44, 4.39) * mm});
            skLineSegment(sketch, "E1422", {"start": v(13.44, 4.39) * mm, "end": v(13.44, 4.4) * mm});
            skLineSegment(sketch, "E1423", {"start": v(13.44, 4.4) * mm, "end": v(13.45, 4.42) * mm});
            skLineSegment(sketch, "E1424", {"start": v(13.45, 4.42) * mm, "end": v(13.47, 4.43) * mm});
            skLineSegment(sketch, "E1425", {"start": v(13.47, 4.43) * mm, "end": v(13.49, 4.45) * mm});
            skLineSegment(sketch, "E1426", {"start": v(13.49, 4.45) * mm, "end": v(13.5, 4.46) * mm});
            skLineSegment(sketch, "E1427", {"start": v(13.5, 4.46) * mm, "end": v(13.53, 4.48) * mm});
            skLineSegment(sketch, "E1428", {"start": v(13.53, 4.48) * mm, "end": v(13.56, 4.5) * mm});
            skLineSegment(sketch, "E1429", {"start": v(13.56, 4.5) * mm, "end": v(13.58, 4.5) * mm});
            skLineSegment(sketch, "E1430", {"start": v(13.58, 4.5) * mm, "end": v(13.6, 4.53) * mm});
            skLineSegment(sketch, "E1431", {"start": v(13.6, 4.53) * mm, "end": v(13.65, 4.55) * mm});
            skLineSegment(sketch, "E1432", {"start": v(13.65, 4.55) * mm, "end": v(13.69, 4.57) * mm});
            skLineSegment(sketch, "E1433", {"start": v(13.69, 4.57) * mm, "end": v(13.73, 4.6) * mm});
            skLineSegment(sketch, "E1434", {"start": v(13.73, 4.6) * mm, "end": v(13.77, 4.63) * mm});
            skLineSegment(sketch, "E1435", {"start": v(13.77, 4.63) * mm, "end": v(13.82, 4.66) * mm});
            skLineSegment(sketch, "E1436", {"start": v(13.82, 4.66) * mm, "end": v(13.87, 4.7) * mm});
            skLineSegment(sketch, "E1437", {"start": v(13.87, 4.7) * mm, "end": v(13.92, 4.74) * mm});
            skLineSegment(sketch, "E1438", {"start": v(13.92, 4.74) * mm, "end": v(13.97, 4.78) * mm});
            skLineSegment(sketch, "E1439", {"start": v(13.97, 4.78) * mm, "end": v(14.02, 4.82) * mm});
            skLineSegment(sketch, "E1440", {"start": v(14.02, 4.82) * mm, "end": v(14.08, 4.87) * mm});
            skLineSegment(sketch, "E1441", {"start": v(14.08, 4.87) * mm, "end": v(14.14, 4.92) * mm});
            skLineSegment(sketch, "E1442", {"start": v(14.14, 4.92) * mm, "end": v(14.2, 4.97) * mm});
            skLineSegment(sketch, "E1443", {"start": v(14.2, 4.97) * mm, "end": v(14.26, 5.02) * mm});
            skLineSegment(sketch, "E1444", {"start": v(14.26, 5.02) * mm, "end": v(14.32, 5.08) * mm});
            skLineSegment(sketch, "E1445", {"start": v(14.32, 5.08) * mm, "end": v(14.38, 5.14) * mm});
            skLineSegment(sketch, "E1446", {"start": v(14.38, 5.14) * mm, "end": v(14.45, 5.2) * mm});
            skLineSegment(sketch, "E1447", {"start": v(14.45, 5.2) * mm, "end": v(14.51, 5.28) * mm});
            skLineSegment(sketch, "E1448", {"start": v(14.51, 5.28) * mm, "end": v(14.56, 5.33) * mm});
            skLineSegment(sketch, "E1449", {"start": v(14.56, 5.33) * mm, "end": v(14.47, 5.6) * mm});
            skLineSegment(sketch, "E1450", {"start": v(14.47, 5.6) * mm, "end": v(14.34, 5.85) * mm});
            skLineSegment(sketch, "E1451", {"start": v(14.34, 5.85) * mm, "end": v(14.28, 5.85) * mm});
            skLineSegment(sketch, "E1452", {"start": v(14.28, 5.85) * mm, "end": v(14.18, 5.85) * mm});
            skLineSegment(sketch, "E1453", {"start": v(14.18, 5.85) * mm, "end": v(14.09, 5.85) * mm});
            skLineSegment(sketch, "E1454", {"start": v(14.09, 5.85) * mm, "end": v(14, 5.85) * mm});
            skLineSegment(sketch, "E1455", {"start": v(14, 5.85) * mm, "end": v(13.91, 5.85) * mm});
            skLineSegment(sketch, "E1456", {"start": v(13.91, 5.85) * mm, "end": v(13.83, 5.84) * mm});
            skLineSegment(sketch, "E1457", {"start": v(13.83, 5.84) * mm, "end": v(13.75, 5.84) * mm});
            skLineSegment(sketch, "E1458", {"start": v(13.75, 5.84) * mm, "end": v(13.68, 5.83) * mm});
            skLineSegment(sketch, "E1459", {"start": v(13.68, 5.83) * mm, "end": v(13.6, 5.83) * mm});
            skLineSegment(sketch, "E1460", {"start": v(13.6, 5.83) * mm, "end": v(13.54, 5.82) * mm});
            skLineSegment(sketch, "E1461", {"start": v(13.54, 5.82) * mm, "end": v(13.47, 5.81) * mm});
            skLineSegment(sketch, "E1462", {"start": v(13.47, 5.81) * mm, "end": v(13.4, 5.8) * mm});
            skLineSegment(sketch, "E1463", {"start": v(13.4, 5.8) * mm, "end": v(13.35, 5.8) * mm});
            skLineSegment(sketch, "E1464", {"start": v(13.35, 5.8) * mm, "end": v(13.3, 5.78) * mm});
            skLineSegment(sketch, "E1465", {"start": v(13.3, 5.78) * mm, "end": v(13.24, 5.77) * mm});
            skLineSegment(sketch, "E1466", {"start": v(13.24, 5.77) * mm, "end": v(13.2, 5.76) * mm});
            skLineSegment(sketch, "E1467", {"start": v(13.2, 5.76) * mm, "end": v(13.15, 5.75) * mm});
            skLineSegment(sketch, "E1468", {"start": v(13.15, 5.75) * mm, "end": v(13.1, 5.74) * mm});
            skLineSegment(sketch, "E1469", {"start": v(13.1, 5.74) * mm, "end": v(13.07, 5.73) * mm});
            skLineSegment(sketch, "E1470", {"start": v(13.07, 5.73) * mm, "end": v(13.05, 5.73) * mm});
            skLineSegment(sketch, "E1471", {"start": v(13.05, 5.73) * mm, "end": v(13.02, 5.72) * mm});
            skLineSegment(sketch, "E1472", {"start": v(13.02, 5.72) * mm, "end": v(12.99, 5.71) * mm});
            skLineSegment(sketch, "E1473", {"start": v(12.99, 5.71) * mm, "end": v(12.96, 5.71) * mm});
            skLineSegment(sketch, "E1474", {"start": v(12.96, 5.71) * mm, "end": v(12.94, 5.7) * mm});
            skLineSegment(sketch, "E1475", {"start": v(12.94, 5.7) * mm, "end": v(12.92, 5.71) * mm});
            skLineSegment(sketch, "E1476", {"start": v(12.92, 5.71) * mm, "end": v(12.9, 5.71) * mm});
            skLineSegment(sketch, "E1477", {"start": v(12.9, 5.71) * mm, "end": v(12.89, 5.72) * mm});
            skLineSegment(sketch, "E1478", {"start": v(12.89, 5.72) * mm, "end": v(12.88, 5.73) * mm});
            skLineSegment(sketch, "E1479", {"start": v(12.88, 5.73) * mm, "end": v(12.87, 5.73) * mm});
            skLineSegment(sketch, "E1480", {"start": v(12.87, 5.73) * mm, "end": v(12.78, 5.91) * mm});
            skLineSegment(sketch, "E1481", {"start": v(12.78, 5.91) * mm, "end": v(12.69, 6.1) * mm});
            skLineSegment(sketch, "E1482", {"start": v(12.69, 6.1) * mm, "end": v(12.6, 6.27) * mm});
            skLineSegment(sketch, "E1483", {"start": v(12.6, 6.27) * mm, "end": v(12.6, 6.28) * mm});
            skLineSegment(sketch, "E1484", {"start": v(12.6, 6.28) * mm, "end": v(12.6, 6.3) * mm});
            skLineSegment(sketch, "E1485", {"start": v(12.6, 6.3) * mm, "end": v(12.6, 6.3) * mm});
            skLineSegment(sketch, "E1486", {"start": v(12.6, 6.3) * mm, "end": v(12.6, 6.32) * mm});
            skLineSegment(sketch, "E1487", {"start": v(12.6, 6.32) * mm, "end": v(12.62, 6.34) * mm});
            skLineSegment(sketch, "E1488", {"start": v(12.62, 6.34) * mm, "end": v(12.63, 6.36) * mm});
            skLineSegment(sketch, "E1489", {"start": v(12.63, 6.36) * mm, "end": v(12.65, 6.38) * mm});
            skLineSegment(sketch, "E1490", {"start": v(12.65, 6.38) * mm, "end": v(12.67, 6.4) * mm});
            skLineSegment(sketch, "E1491", {"start": v(12.67, 6.4) * mm, "end": v(12.7, 6.42) * mm});
            skLineSegment(sketch, "E1492", {"start": v(12.7, 6.42) * mm, "end": v(12.71, 6.43) * mm});
            skLineSegment(sketch, "E1493", {"start": v(12.71, 6.43) * mm, "end": v(12.74, 6.46) * mm});
            skLineSegment(sketch, "E1494", {"start": v(12.74, 6.46) * mm, "end": v(12.77, 6.49) * mm});
            skLineSegment(sketch, "E1495", {"start": v(12.77, 6.49) * mm, "end": v(12.8, 6.52) * mm});
            skLineSegment(sketch, "E1496", {"start": v(12.8, 6.52) * mm, "end": v(12.85, 6.55) * mm});
            skLineSegment(sketch, "E1497", {"start": v(12.85, 6.55) * mm, "end": v(12.89, 6.59) * mm});
            skLineSegment(sketch, "E1498", {"start": v(12.89, 6.59) * mm, "end": v(12.93, 6.63) * mm});
            skLineSegment(sketch, "E1499", {"start": v(12.93, 6.63) * mm, "end": v(12.97, 6.67) * mm});
            skLineSegment(sketch, "E1500", {"start": v(12.97, 6.67) * mm, "end": v(13.01, 6.71) * mm});
            skLineSegment(sketch, "E1501", {"start": v(13.01, 6.71) * mm, "end": v(13.06, 6.76) * mm});
            skLineSegment(sketch, "E1502", {"start": v(13.06, 6.76) * mm, "end": v(13.1, 6.81) * mm});
            skLineSegment(sketch, "E1503", {"start": v(13.1, 6.81) * mm, "end": v(13.15, 6.87) * mm});
            skLineSegment(sketch, "E1504", {"start": v(13.15, 6.87) * mm, "end": v(13.2, 6.92) * mm});
            skLineSegment(sketch, "E1505", {"start": v(13.2, 6.92) * mm, "end": v(13.25, 6.98) * mm});
            skLineSegment(sketch, "E1506", {"start": v(13.25, 6.98) * mm, "end": v(13.3, 7.05) * mm});
            skLineSegment(sketch, "E1507", {"start": v(13.3, 7.05) * mm, "end": v(13.36, 7.12) * mm});
            skLineSegment(sketch, "E1508", {"start": v(13.36, 7.12) * mm, "end": v(13.4, 7.19) * mm});
            skLineSegment(sketch, "E1509", {"start": v(13.4, 7.19) * mm, "end": v(13.46, 7.26) * mm});
            skLineSegment(sketch, "E1510", {"start": v(13.46, 7.26) * mm, "end": v(13.52, 7.34) * mm});
            skLineSegment(sketch, "E1511", {"start": v(13.52, 7.34) * mm, "end": v(13.55, 7.4) * mm});
            skLineSegment(sketch, "E1512", {"start": v(13.55, 7.4) * mm, "end": v(13.43, 7.65) * mm});
            skLineSegment(sketch, "E1513", {"start": v(13.43, 7.65) * mm, "end": v(13.26, 7.88) * mm});
            skLineSegment(sketch, "E1514", {"start": v(13.26, 7.88) * mm, "end": v(13.2, 7.87) * mm});
            skLineSegment(sketch, "E1515", {"start": v(13.2, 7.87) * mm, "end": v(13.1, 7.86) * mm});
            skLineSegment(sketch, "E1516", {"start": v(13.1, 7.86) * mm, "end": v(13, 7.84) * mm});
            skLineSegment(sketch, "E1517", {"start": v(13, 7.84) * mm, "end": v(12.92, 7.83) * mm});
            skLineSegment(sketch, "E1518", {"start": v(12.92, 7.83) * mm, "end": v(12.84, 7.8) * mm});
            skLineSegment(sketch, "E1519", {"start": v(12.84, 7.8) * mm, "end": v(12.76, 7.8) * mm});
            skLineSegment(sketch, "E1520", {"start": v(12.76, 7.8) * mm, "end": v(12.68, 7.78) * mm});
            skLineSegment(sketch, "E1521", {"start": v(12.68, 7.78) * mm, "end": v(12.6, 7.76) * mm});
            skLineSegment(sketch, "E1522", {"start": v(12.6, 7.76) * mm, "end": v(12.53, 7.74) * mm});
            skLineSegment(sketch, "E1523", {"start": v(12.53, 7.74) * mm, "end": v(12.47, 7.72) * mm});
            skLineSegment(sketch, "E1524", {"start": v(12.47, 7.72) * mm, "end": v(12.4, 7.7) * mm});
            skLineSegment(sketch, "E1525", {"start": v(12.4, 7.7) * mm, "end": v(12.34, 7.68) * mm});
            skLineSegment(sketch, "E1526", {"start": v(12.34, 7.68) * mm, "end": v(12.29, 7.67) * mm});
            skLineSegment(sketch, "E1527", {"start": v(12.29, 7.67) * mm, "end": v(12.23, 7.65) * mm});
            skLineSegment(sketch, "E1528", {"start": v(12.23, 7.65) * mm, "end": v(12.18, 7.63) * mm});
            skLineSegment(sketch, "E1529", {"start": v(12.18, 7.63) * mm, "end": v(12.14, 7.61) * mm});
            skLineSegment(sketch, "E1530", {"start": v(12.14, 7.61) * mm, "end": v(12.1, 7.6) * mm});
            skLineSegment(sketch, "E1531", {"start": v(12.1, 7.6) * mm, "end": v(12.05, 7.58) * mm});
            skLineSegment(sketch, "E1532", {"start": v(12.05, 7.58) * mm, "end": v(12.02, 7.56) * mm});
            skLineSegment(sketch, "E1533", {"start": v(12.02, 7.56) * mm, "end": v(12, 7.55) * mm});
            skLineSegment(sketch, "E1534", {"start": v(12, 7.55) * mm, "end": v(11.97, 7.54) * mm});
            skLineSegment(sketch, "E1535", {"start": v(11.97, 7.54) * mm, "end": v(11.94, 7.53) * mm});
            skLineSegment(sketch, "E1536", {"start": v(11.94, 7.53) * mm, "end": v(11.92, 7.52) * mm});
            skLineSegment(sketch, "E1537", {"start": v(11.92, 7.52) * mm, "end": v(11.9, 7.52) * mm});
            skLineSegment(sketch, "E1538", {"start": v(11.9, 7.52) * mm, "end": v(11.87, 7.52) * mm});
            skLineSegment(sketch, "E1539", {"start": v(11.87, 7.52) * mm, "end": v(11.86, 7.52) * mm});
            skLineSegment(sketch, "E1540", {"start": v(11.86, 7.52) * mm, "end": v(11.84, 7.52) * mm});
            skLineSegment(sketch, "E1541", {"start": v(11.84, 7.52) * mm, "end": v(11.83, 7.53) * mm});
            skLineSegment(sketch, "E1542", {"start": v(11.83, 7.53) * mm, "end": v(11.82, 7.53) * mm});
            skLineSegment(sketch, "E1543", {"start": v(11.82, 7.53) * mm, "end": v(11.7, 7.7) * mm});
            skLineSegment(sketch, "E1544", {"start": v(11.7, 7.7) * mm, "end": v(11.59, 7.86) * mm});
            skLineSegment(sketch, "E1545", {"start": v(11.59, 7.86) * mm, "end": v(11.47, 8.02) * mm});
            skLineSegment(sketch, "E1546", {"start": v(11.47, 8.02) * mm, "end": v(11.46, 8.03) * mm});
            skLineSegment(sketch, "E1547", {"start": v(11.46, 8.03) * mm, "end": v(11.46, 8.04) * mm});
            skLineSegment(sketch, "E1548", {"start": v(11.46, 8.04) * mm, "end": v(11.46, 8.06) * mm});
            skLineSegment(sketch, "E1549", {"start": v(11.46, 8.06) * mm, "end": v(11.47, 8.07) * mm});
            skLineSegment(sketch, "E1550", {"start": v(11.47, 8.07) * mm, "end": v(11.48, 8.1) * mm});
            skLineSegment(sketch, "E1551", {"start": v(11.48, 8.1) * mm, "end": v(11.49, 8.11) * mm});
            skLineSegment(sketch, "E1552", {"start": v(11.49, 8.11) * mm, "end": v(11.5, 8.14) * mm});
            skLineSegment(sketch, "E1553", {"start": v(11.5, 8.14) * mm, "end": v(11.52, 8.16) * mm});
            skLineSegment(sketch, "E1554", {"start": v(11.52, 8.16) * mm, "end": v(11.54, 8.18) * mm});
            skLineSegment(sketch, "E1555", {"start": v(11.54, 8.18) * mm, "end": v(11.56, 8.2) * mm});
            skLineSegment(sketch, "E1556", {"start": v(11.56, 8.2) * mm, "end": v(11.58, 8.23) * mm});
            skLineSegment(sketch, "E1557", {"start": v(11.58, 8.23) * mm, "end": v(11.61, 8.26) * mm});
            skLineSegment(sketch, "E1558", {"start": v(11.61, 8.26) * mm, "end": v(11.64, 8.3) * mm});
            skLineSegment(sketch, "E1559", {"start": v(11.64, 8.3) * mm, "end": v(11.67, 8.34) * mm});
            skLineSegment(sketch, "E1560", {"start": v(11.67, 8.34) * mm, "end": v(11.7, 8.38) * mm});
            skLineSegment(sketch, "E1561", {"start": v(11.7, 8.38) * mm, "end": v(11.74, 8.42) * mm});
            skLineSegment(sketch, "E1562", {"start": v(11.74, 8.42) * mm, "end": v(11.77, 8.47) * mm});
            skLineSegment(sketch, "E1563", {"start": v(11.77, 8.47) * mm, "end": v(11.8, 8.52) * mm});
            skLineSegment(sketch, "E1564", {"start": v(11.8, 8.52) * mm, "end": v(11.85, 8.58) * mm});
            skLineSegment(sketch, "E1565", {"start": v(11.85, 8.58) * mm, "end": v(11.88, 8.63) * mm});
            skLineSegment(sketch, "E1566", {"start": v(11.88, 8.63) * mm, "end": v(11.92, 8.7) * mm});
            skLineSegment(sketch, "E1567", {"start": v(11.92, 8.7) * mm, "end": v(11.96, 8.76) * mm});
            skLineSegment(sketch, "E1568", {"start": v(11.96, 8.76) * mm, "end": v(12, 8.83) * mm});
            skLineSegment(sketch, "E1569", {"start": v(12, 8.83) * mm, "end": v(12.04, 8.9) * mm});
            skLineSegment(sketch, "E1570", {"start": v(12.04, 8.9) * mm, "end": v(12.09, 8.98) * mm});
            skLineSegment(sketch, "E1571", {"start": v(12.09, 8.98) * mm, "end": v(12.13, 9.05) * mm});
            skLineSegment(sketch, "E1572", {"start": v(12.13, 9.05) * mm, "end": v(12.17, 9.14) * mm});
            skLineSegment(sketch, "E1573", {"start": v(12.17, 9.14) * mm, "end": v(12.21, 9.22) * mm});
            skLineSegment(sketch, "E1574", {"start": v(12.21, 9.22) * mm, "end": v(12.24, 9.28) * mm});
            skLineSegment(sketch, "E1575", {"start": v(12.24, 9.28) * mm, "end": v(12.07, 9.5) * mm});
            skLineSegment(sketch, "E1576", {"start": v(12.07, 9.5) * mm, "end": v(11.87, 9.71) * mm});
            skLineSegment(sketch, "E1577", {"start": v(11.87, 9.71) * mm, "end": v(11.8, 9.7) * mm});
            skLineSegment(sketch, "E1578", {"start": v(11.8, 9.7) * mm, "end": v(11.72, 9.66) * mm});
            skLineSegment(sketch, "E1579", {"start": v(11.72, 9.66) * mm, "end": v(11.63, 9.64) * mm});
            skLineSegment(sketch, "E1580", {"start": v(11.63, 9.64) * mm, "end": v(11.55, 9.6) * mm});
            skLineSegment(sketch, "E1581", {"start": v(11.55, 9.6) * mm, "end": v(11.47, 9.58) * mm});
            skLineSegment(sketch, "E1582", {"start": v(11.47, 9.58) * mm, "end": v(11.39, 9.55) * mm});
            skLineSegment(sketch, "E1583", {"start": v(11.39, 9.55) * mm, "end": v(11.31, 9.52) * mm});
            skLineSegment(sketch, "E1584", {"start": v(11.31, 9.52) * mm, "end": v(11.24, 9.5) * mm});
            skLineSegment(sketch, "E1585", {"start": v(11.24, 9.5) * mm, "end": v(11.18, 9.46) * mm});
            skLineSegment(sketch, "E1586", {"start": v(11.18, 9.46) * mm, "end": v(11.11, 9.43) * mm});
            skLineSegment(sketch, "E1587", {"start": v(11.11, 9.43) * mm, "end": v(11.05, 9.4) * mm});
            skLineSegment(sketch, "E1588", {"start": v(11.05, 9.4) * mm, "end": v(11, 9.38) * mm});
            skLineSegment(sketch, "E1589", {"start": v(11, 9.38) * mm, "end": v(10.95, 9.35) * mm});
            skLineSegment(sketch, "E1590", {"start": v(10.95, 9.35) * mm, "end": v(10.9, 9.32) * mm});
            skLineSegment(sketch, "E1591", {"start": v(10.9, 9.32) * mm, "end": v(10.85, 9.3) * mm});
            skLineSegment(sketch, "E1592", {"start": v(10.85, 9.3) * mm, "end": v(10.8, 9.27) * mm});
            skLineSegment(sketch, "E1593", {"start": v(10.8, 9.27) * mm, "end": v(10.77, 9.25) * mm});
            skLineSegment(sketch, "E1594", {"start": v(10.77, 9.25) * mm, "end": v(10.73, 9.23) * mm});
            skLineSegment(sketch, "E1595", {"start": v(10.73, 9.23) * mm, "end": v(10.7, 9.2) * mm});
            skLineSegment(sketch, "E1596", {"start": v(10.7, 9.2) * mm, "end": v(10.68, 9.2) * mm});
            skLineSegment(sketch, "E1597", {"start": v(10.68, 9.2) * mm, "end": v(10.65, 9.18) * mm});
            skLineSegment(sketch, "E1598", {"start": v(10.65, 9.18) * mm, "end": v(10.63, 9.16) * mm});
            skLineSegment(sketch, "E1599", {"start": v(10.63, 9.16) * mm, "end": v(10.6, 9.15) * mm});
            skLineSegment(sketch, "E1600", {"start": v(10.6, 9.15) * mm, "end": v(10.58, 9.15) * mm});
            skLineSegment(sketch, "E1601", {"start": v(10.58, 9.15) * mm, "end": v(10.56, 9.14) * mm});
            skLineSegment(sketch, "E1602", {"start": v(10.56, 9.14) * mm, "end": v(10.54, 9.14) * mm});
            skLineSegment(sketch, "E1603", {"start": v(10.54, 9.14) * mm, "end": v(10.53, 9.14) * mm});
            skLineSegment(sketch, "E1604", {"start": v(10.53, 9.14) * mm, "end": v(10.52, 9.14) * mm});
            skLineSegment(sketch, "E1605", {"start": v(10.52, 9.14) * mm, "end": v(10.5, 9.15) * mm});
            skLineSegment(sketch, "E1606", {"start": v(10.5, 9.15) * mm, "end": v(10.37, 9.29) * mm});
            skLineSegment(sketch, "E1607", {"start": v(10.37, 9.29) * mm, "end": v(10.22, 9.43) * mm});
            skLineSegment(sketch, "E1608", {"start": v(10.22, 9.43) * mm, "end": v(10.08, 9.57) * mm});
            skLineSegment(sketch, "E1609", {"start": v(10.08, 9.57) * mm, "end": v(10.07, 9.58) * mm});
            skLineSegment(sketch, "E1610", {"start": v(10.07, 9.58) * mm, "end": v(10.07, 9.6) * mm});
            skLineSegment(sketch, "E1611", {"start": v(10.07, 9.6) * mm, "end": v(10.07, 9.6) * mm});
            skLineSegment(sketch, "E1612", {"start": v(10.07, 9.6) * mm, "end": v(10.07, 9.63) * mm});
            skLineSegment(sketch, "E1613", {"start": v(10.07, 9.63) * mm, "end": v(10.08, 9.65) * mm});
            skLineSegment(sketch, "E1614", {"start": v(10.08, 9.65) * mm, "end": v(10.09, 9.67) * mm});
            skLineSegment(sketch, "E1615", {"start": v(10.09, 9.67) * mm, "end": v(10.1, 9.7) * mm});
            skLineSegment(sketch, "E1616", {"start": v(10.1, 9.7) * mm, "end": v(10.11, 9.72) * mm});
            skLineSegment(sketch, "E1617", {"start": v(10.11, 9.72) * mm, "end": v(10.13, 9.75) * mm});
            skLineSegment(sketch, "E1618", {"start": v(10.13, 9.75) * mm, "end": v(10.14, 9.76) * mm});
            skLineSegment(sketch, "E1619", {"start": v(10.14, 9.76) * mm, "end": v(10.16, 9.8) * mm});
            skLineSegment(sketch, "E1620", {"start": v(10.16, 9.8) * mm, "end": v(10.18, 9.83) * mm});
            skLineSegment(sketch, "E1621", {"start": v(10.18, 9.83) * mm, "end": v(10.2, 9.87) * mm});
            skLineSegment(sketch, "E1622", {"start": v(10.2, 9.87) * mm, "end": v(10.23, 9.92) * mm});
            skLineSegment(sketch, "E1623", {"start": v(10.23, 9.92) * mm, "end": v(10.26, 9.96) * mm});
            skLineSegment(sketch, "E1624", {"start": v(10.26, 9.96) * mm, "end": v(10.28, 10.01) * mm});
            skLineSegment(sketch, "E1625", {"start": v(10.28, 10.01) * mm, "end": v(10.31, 10.06) * mm});
            skLineSegment(sketch, "E1626", {"start": v(10.31, 10.06) * mm, "end": v(10.34, 10.12) * mm});
            skLineSegment(sketch, "E1627", {"start": v(10.34, 10.12) * mm, "end": v(10.37, 10.18) * mm});
            skLineSegment(sketch, "E1628", {"start": v(10.37, 10.18) * mm, "end": v(10.4, 10.24) * mm});
            skLineSegment(sketch, "E1629", {"start": v(10.4, 10.24) * mm, "end": v(10.42, 10.31) * mm});
            skLineSegment(sketch, "E1630", {"start": v(10.42, 10.31) * mm, "end": v(10.45, 10.38) * mm});
            skLineSegment(sketch, "E1631", {"start": v(10.45, 10.38) * mm, "end": v(10.48, 10.45) * mm});
            skLineSegment(sketch, "E1632", {"start": v(10.48, 10.45) * mm, "end": v(10.51, 10.53) * mm});
            skLineSegment(sketch, "E1633", {"start": v(10.51, 10.53) * mm, "end": v(10.54, 10.61) * mm});
            skLineSegment(sketch, "E1634", {"start": v(10.54, 10.61) * mm, "end": v(10.57, 10.7) * mm});
            skLineSegment(sketch, "E1635", {"start": v(10.57, 10.7) * mm, "end": v(10.6, 10.78) * mm});
            skLineSegment(sketch, "E1636", {"start": v(10.6, 10.78) * mm, "end": v(10.63, 10.87) * mm});
            skLineSegment(sketch, "E1637", {"start": v(10.63, 10.87) * mm, "end": v(10.64, 10.94) * mm});
            skLineSegment(sketch, "E1638", {"start": v(10.64, 10.94) * mm, "end": v(10.44, 11.14) * mm});
            skLineSegment(sketch, "E1639", {"start": v(10.44, 11.14) * mm, "end": v(10.21, 11.3) * mm});
            skLineSegment(sketch, "E1640", {"start": v(10.21, 11.3) * mm, "end": v(10.16, 11.28) * mm});
            skLineSegment(sketch, "E1641", {"start": v(10.16, 11.28) * mm, "end": v(10.07, 11.24) * mm});
            skLineSegment(sketch, "E1642", {"start": v(10.07, 11.24) * mm, "end": v(9.99, 11.2) * mm});
            skLineSegment(sketch, "E1643", {"start": v(9.99, 11.2) * mm, "end": v(9.9, 11.15) * mm});
            skLineSegment(sketch, "E1644", {"start": v(9.9, 11.15) * mm, "end": v(9.83, 11.11) * mm});
            skLineSegment(sketch, "E1645", {"start": v(9.83, 11.11) * mm, "end": v(9.76, 11.07) * mm});
            skLineSegment(sketch, "E1646", {"start": v(9.76, 11.07) * mm, "end": v(9.7, 11.03) * mm});
            skLineSegment(sketch, "E1647", {"start": v(9.7, 11.03) * mm, "end": v(9.63, 10.99) * mm});
            skLineSegment(sketch, "E1648", {"start": v(9.63, 10.99) * mm, "end": v(9.57, 10.95) * mm});
            skLineSegment(sketch, "E1649", {"start": v(9.57, 10.95) * mm, "end": v(9.51, 10.91) * mm});
            skLineSegment(sketch, "E1650", {"start": v(9.51, 10.91) * mm, "end": v(9.46, 10.88) * mm});
            skLineSegment(sketch, "E1651", {"start": v(9.46, 10.88) * mm, "end": v(9.4, 10.84) * mm});
            skLineSegment(sketch, "E1652", {"start": v(9.4, 10.84) * mm, "end": v(9.36, 10.8) * mm});
            skLineSegment(sketch, "E1653", {"start": v(9.36, 10.8) * mm, "end": v(9.31, 10.77) * mm});
            skLineSegment(sketch, "E1654", {"start": v(9.31, 10.77) * mm, "end": v(9.27, 10.74) * mm});
            skLineSegment(sketch, "E1655", {"start": v(9.27, 10.74) * mm, "end": v(9.23, 10.7) * mm});
            skLineSegment(sketch, "E1656", {"start": v(9.23, 10.7) * mm, "end": v(9.2, 10.68) * mm});
            skLineSegment(sketch, "E1657", {"start": v(9.2, 10.68) * mm, "end": v(9.16, 10.65) * mm});
            skLineSegment(sketch, "E1658", {"start": v(9.16, 10.65) * mm, "end": v(9.13, 10.62) * mm});
            skLineSegment(sketch, "E1659", {"start": v(9.13, 10.62) * mm, "end": v(9.12, 10.6) * mm});
            skLineSegment(sketch, "E1660", {"start": v(9.12, 10.6) * mm, "end": v(9.1, 10.59) * mm});
            skLineSegment(sketch, "E1661", {"start": v(9.1, 10.59) * mm, "end": v(9.07, 10.57) * mm});
            skLineSegment(sketch, "E1662", {"start": v(9.07, 10.57) * mm, "end": v(9.05, 10.56) * mm});
            skLineSegment(sketch, "E1663", {"start": v(9.05, 10.56) * mm, "end": v(9.03, 10.54) * mm});
            skLineSegment(sketch, "E1664", {"start": v(9.03, 10.54) * mm, "end": v(9, 10.54) * mm});
            skLineSegment(sketch, "E1665", {"start": v(9, 10.54) * mm, "end": v(9, 10.53) * mm});
            skLineSegment(sketch, "E1666", {"start": v(9, 10.53) * mm, "end": v(8.98, 10.53) * mm});
            skLineSegment(sketch, "E1667", {"start": v(8.98, 10.53) * mm, "end": v(8.96, 10.53) * mm});
            skLineSegment(sketch, "E1668", {"start": v(8.96, 10.53) * mm, "end": v(8.95, 10.53) * mm});
            skLineSegment(sketch, "E1669", {"start": v(8.95, 10.53) * mm, "end": v(8.8, 10.65) * mm});
            skLineSegment(sketch, "E1670", {"start": v(8.8, 10.65) * mm, "end": v(8.63, 10.77) * mm});
            skLineSegment(sketch, "E1671", {"start": v(8.63, 10.77) * mm, "end": v(8.47, 10.89) * mm});
            skLineSegment(sketch, "E1672", {"start": v(8.47, 10.89) * mm, "end": v(8.46, 10.9) * mm});
            skLineSegment(sketch, "E1673", {"start": v(8.46, 10.9) * mm, "end": v(8.45, 10.9) * mm});
            skLineSegment(sketch, "E1674", {"start": v(8.45, 10.9) * mm, "end": v(8.45, 10.92) * mm});
            skLineSegment(sketch, "E1675", {"start": v(8.45, 10.92) * mm, "end": v(8.45, 10.94) * mm});
            skLineSegment(sketch, "E1676", {"start": v(8.45, 10.94) * mm, "end": v(8.45, 10.96) * mm});
            skLineSegment(sketch, "E1677", {"start": v(8.45, 10.96) * mm, "end": v(8.46, 10.98) * mm});
            skLineSegment(sketch, "E1678", {"start": v(8.46, 10.98) * mm, "end": v(8.47, 11) * mm});
            skLineSegment(sketch, "E1679", {"start": v(8.47, 11) * mm, "end": v(8.48, 11.04) * mm});
            skLineSegment(sketch, "E1680", {"start": v(8.48, 11.04) * mm, "end": v(8.49, 11.07) * mm});
            skLineSegment(sketch, "E1681", {"start": v(8.49, 11.07) * mm, "end": v(8.5, 11.08) * mm});
            skLineSegment(sketch, "E1682", {"start": v(8.5, 11.08) * mm, "end": v(8.51, 11.12) * mm});
            skLineSegment(sketch, "E1683", {"start": v(8.51, 11.12) * mm, "end": v(8.53, 11.16) * mm});
            skLineSegment(sketch, "E1684", {"start": v(8.53, 11.16) * mm, "end": v(8.55, 11.2) * mm});
            skLineSegment(sketch, "E1685", {"start": v(8.55, 11.2) * mm, "end": v(8.56, 11.25) * mm});
            skLineSegment(sketch, "E1686", {"start": v(8.56, 11.25) * mm, "end": v(8.58, 11.3) * mm});
            skLineSegment(sketch, "E1687", {"start": v(8.58, 11.3) * mm, "end": v(8.6, 11.35) * mm});
            skLineSegment(sketch, "E1688", {"start": v(8.6, 11.35) * mm, "end": v(8.62, 11.41) * mm});
            skLineSegment(sketch, "E1689", {"start": v(8.62, 11.41) * mm, "end": v(8.64, 11.47) * mm});
            skLineSegment(sketch, "E1690", {"start": v(8.64, 11.47) * mm, "end": v(8.66, 11.53) * mm});
            skLineSegment(sketch, "E1691", {"start": v(8.66, 11.53) * mm, "end": v(8.67, 11.6) * mm});
            skLineSegment(sketch, "E1692", {"start": v(8.67, 11.6) * mm, "end": v(8.7, 11.67) * mm});
            skLineSegment(sketch, "E1693", {"start": v(8.7, 11.67) * mm, "end": v(8.7, 11.75) * mm});
            skLineSegment(sketch, "E1694", {"start": v(8.7, 11.75) * mm, "end": v(8.73, 11.82) * mm});
            skLineSegment(sketch, "E1695", {"start": v(8.73, 11.82) * mm, "end": v(8.74, 11.9) * mm});
            skLineSegment(sketch, "E1696", {"start": v(8.74, 11.9) * mm, "end": v(8.76, 11.99) * mm});
            skLineSegment(sketch, "E1697", {"start": v(8.76, 11.99) * mm, "end": v(8.77, 12.07) * mm});
            skLineSegment(sketch, "E1698", {"start": v(8.77, 12.07) * mm, "end": v(8.79, 12.17) * mm});
            skLineSegment(sketch, "E1699", {"start": v(8.79, 12.17) * mm, "end": v(8.8, 12.26) * mm});
            skLineSegment(sketch, "E1700", {"start": v(8.8, 12.26) * mm, "end": v(8.81, 12.32) * mm});
            skLineSegment(sketch, "E1701", {"start": v(8.81, 12.32) * mm, "end": v(8.58, 12.5) * mm});
            skLineSegment(sketch, "E1702", {"start": v(8.58, 12.5) * mm, "end": v(8.33, 12.62) * mm});
            skLineSegment(sketch, "E1703", {"start": v(8.33, 12.62) * mm, "end": v(8.27, 12.58) * mm});
            skLineSegment(sketch, "E1704", {"start": v(8.27, 12.58) * mm, "end": v(8.2, 12.53) * mm});
            skLineSegment(sketch, "E1705", {"start": v(8.2, 12.53) * mm, "end": v(8.12, 12.48) * mm});
            skLineSegment(sketch, "E1706", {"start": v(8.12, 12.48) * mm, "end": v(8.05, 12.42) * mm});
            skLineSegment(sketch, "E1707", {"start": v(8.05, 12.42) * mm, "end": v(7.98, 12.37) * mm});
            skLineSegment(sketch, "E1708", {"start": v(7.98, 12.37) * mm, "end": v(7.92, 12.32) * mm});
            skLineSegment(sketch, "E1709", {"start": v(7.92, 12.32) * mm, "end": v(7.86, 12.27) * mm});
            skLineSegment(sketch, "E1710", {"start": v(7.86, 12.27) * mm, "end": v(7.8, 12.22) * mm});
            skLineSegment(sketch, "E1711", {"start": v(7.8, 12.22) * mm, "end": v(7.75, 12.17) * mm});
            skLineSegment(sketch, "E1712", {"start": v(7.75, 12.17) * mm, "end": v(7.7, 12.12) * mm});
            skLineSegment(sketch, "E1713", {"start": v(7.7, 12.12) * mm, "end": v(7.65, 12.08) * mm});
            skLineSegment(sketch, "E1714", {"start": v(7.65, 12.08) * mm, "end": v(7.6, 12.03) * mm});
            skLineSegment(sketch, "E1715", {"start": v(7.6, 12.03) * mm, "end": v(7.56, 12) * mm});
            skLineSegment(sketch, "E1716", {"start": v(7.56, 12) * mm, "end": v(7.52, 11.95) * mm});
            skLineSegment(sketch, "E1717", {"start": v(7.52, 11.95) * mm, "end": v(7.48, 11.91) * mm});
            skLineSegment(sketch, "E1718", {"start": v(7.48, 11.91) * mm, "end": v(7.45, 11.88) * mm});
            skLineSegment(sketch, "E1719", {"start": v(7.45, 11.88) * mm, "end": v(7.42, 11.84) * mm});
            skLineSegment(sketch, "E1720", {"start": v(7.42, 11.84) * mm, "end": v(7.4, 11.8) * mm});
            skLineSegment(sketch, "E1721", {"start": v(7.4, 11.8) * mm, "end": v(7.37, 11.78) * mm});
            skLineSegment(sketch, "E1722", {"start": v(7.37, 11.78) * mm, "end": v(7.35, 11.76) * mm});
            skLineSegment(sketch, "E1723", {"start": v(7.35, 11.76) * mm, "end": v(7.33, 11.74) * mm});
            skLineSegment(sketch, "E1724", {"start": v(7.33, 11.74) * mm, "end": v(7.31, 11.72) * mm});
            skLineSegment(sketch, "E1725", {"start": v(7.31, 11.72) * mm, "end": v(7.3, 11.7) * mm});
            skLineSegment(sketch, "E1726", {"start": v(7.3, 11.7) * mm, "end": v(7.27, 11.68) * mm});
            skLineSegment(sketch, "E1727", {"start": v(7.27, 11.68) * mm, "end": v(7.26, 11.67) * mm});
            skLineSegment(sketch, "E1728", {"start": v(7.26, 11.67) * mm, "end": v(7.24, 11.66) * mm});
            skLineSegment(sketch, "E1729", {"start": v(7.24, 11.66) * mm, "end": v(7.23, 11.66) * mm});
            skLineSegment(sketch, "E1730", {"start": v(7.23, 11.66) * mm, "end": v(7.21, 11.66) * mm});
            skLineSegment(sketch, "E1731", {"start": v(7.21, 11.66) * mm, "end": v(7.2, 11.66) * mm});
            skLineSegment(sketch, "E1732", {"start": v(7.2, 11.66) * mm, "end": v(7.03, 11.75) * mm});
            skLineSegment(sketch, "E1733", {"start": v(7.03, 11.75) * mm, "end": v(6.84, 11.85) * mm});
            skLineSegment(sketch, "E1734", {"start": v(6.84, 11.85) * mm, "end": v(6.67, 11.93) * mm});
            skLineSegment(sketch, "E1735", {"start": v(6.67, 11.93) * mm, "end": v(6.66, 11.94) * mm});
            skLineSegment(sketch, "E1736", {"start": v(6.66, 11.94) * mm, "end": v(6.65, 11.95) * mm});
            skLineSegment(sketch, "E1737", {"start": v(6.65, 11.95) * mm, "end": v(6.65, 11.97) * mm});
            skLineSegment(sketch, "E1738", {"start": v(6.65, 11.97) * mm, "end": v(6.64, 11.98) * mm});
            skLineSegment(sketch, "E1739", {"start": v(6.64, 11.98) * mm, "end": v(6.64, 12) * mm});
            skLineSegment(sketch, "E1740", {"start": v(6.64, 12) * mm, "end": v(6.64, 12.03) * mm});
            skLineSegment(sketch, "E1741", {"start": v(6.64, 12.03) * mm, "end": v(6.65, 12.05) * mm});
            skLineSegment(sketch, "E1742", {"start": v(6.65, 12.05) * mm, "end": v(6.65, 12.08) * mm});
            skLineSegment(sketch, "E1743", {"start": v(6.65, 12.08) * mm, "end": v(6.66, 12.12) * mm});
            skLineSegment(sketch, "E1744", {"start": v(6.66, 12.12) * mm, "end": v(6.67, 12.13) * mm});
            skLineSegment(sketch, "E1745", {"start": v(6.67, 12.13) * mm, "end": v(6.68, 12.17) * mm});
            skLineSegment(sketch, "E1746", {"start": v(6.68, 12.17) * mm, "end": v(6.69, 12.21) * mm});
            skLineSegment(sketch, "E1747", {"start": v(6.69, 12.21) * mm, "end": v(6.7, 12.26) * mm});
            skLineSegment(sketch, "E1748", {"start": v(6.7, 12.26) * mm, "end": v(6.7, 12.3) * mm});
            skLineSegment(sketch, "E1749", {"start": v(6.7, 12.3) * mm, "end": v(6.72, 12.36) * mm});
            skLineSegment(sketch, "E1750", {"start": v(6.72, 12.36) * mm, "end": v(6.73, 12.42) * mm});
            skLineSegment(sketch, "E1751", {"start": v(6.73, 12.42) * mm, "end": v(6.74, 12.48) * mm});
            skLineSegment(sketch, "E1752", {"start": v(6.74, 12.48) * mm, "end": v(6.74, 12.54) * mm});
            skLineSegment(sketch, "E1753", {"start": v(6.74, 12.54) * mm, "end": v(6.75, 12.6) * mm});
            skLineSegment(sketch, "E1754", {"start": v(6.75, 12.6) * mm, "end": v(6.76, 12.67) * mm});
            skLineSegment(sketch, "E1755", {"start": v(6.76, 12.67) * mm, "end": v(6.77, 12.74) * mm});
            skLineSegment(sketch, "E1756", {"start": v(6.77, 12.74) * mm, "end": v(6.77, 12.82) * mm});
            skLineSegment(sketch, "E1757", {"start": v(6.77, 12.82) * mm, "end": v(6.78, 12.9) * mm});
            skLineSegment(sketch, "E1758", {"start": v(6.78, 12.9) * mm, "end": v(6.78, 12.98) * mm});
            skLineSegment(sketch, "E1759", {"start": v(6.78, 12.98) * mm, "end": v(6.78, 13.07) * mm});
            skLineSegment(sketch, "E1760", {"start": v(6.78, 13.07) * mm, "end": v(6.79, 13.16) * mm});
            skLineSegment(sketch, "E1761", {"start": v(6.79, 13.16) * mm, "end": v(6.79, 13.25) * mm});
            skLineSegment(sketch, "E1762", {"start": v(6.79, 13.25) * mm, "end": v(6.78, 13.34) * mm});
            skLineSegment(sketch, "E1763", {"start": v(6.78, 13.34) * mm, "end": v(6.78, 13.4) * mm});
            skLineSegment(sketch, "E1764", {"start": v(6.78, 13.4) * mm, "end": v(6.53, 13.54) * mm});
            skLineSegment(sketch, "E1765", {"start": v(6.53, 13.54) * mm, "end": v(6.26, 13.62) * mm});
            skLineSegment(sketch, "E1766", {"start": v(6.26, 13.62) * mm, "end": v(6.21, 13.58) * mm});
            skLineSegment(sketch, "E1767", {"start": v(6.21, 13.58) * mm, "end": v(6.14, 13.51) * mm});
            skLineSegment(sketch, "E1768", {"start": v(6.14, 13.51) * mm, "end": v(6.08, 13.45) * mm});
            skLineSegment(sketch, "E1769", {"start": v(6.08, 13.45) * mm, "end": v(6.02, 13.38) * mm});
            skLineSegment(sketch, "E1770", {"start": v(6.02, 13.38) * mm, "end": v(5.96, 13.32) * mm});
            skLineSegment(sketch, "E1771", {"start": v(5.96, 13.32) * mm, "end": v(5.9, 13.26) * mm});
            skLineSegment(sketch, "E1772", {"start": v(5.9, 13.26) * mm, "end": v(5.85, 13.2) * mm});
            skLineSegment(sketch, "E1773", {"start": v(5.85, 13.2) * mm, "end": v(5.8, 13.14) * mm});
            skLineSegment(sketch, "E1774", {"start": v(5.8, 13.14) * mm, "end": v(5.75, 13.09) * mm});
            skLineSegment(sketch, "E1775", {"start": v(5.75, 13.09) * mm, "end": v(5.71, 13.03) * mm});
            skLineSegment(sketch, "E1776", {"start": v(5.71, 13.03) * mm, "end": v(5.67, 12.98) * mm});
            skLineSegment(sketch, "E1777", {"start": v(5.67, 12.98) * mm, "end": v(5.63, 12.93) * mm});
            skLineSegment(sketch, "E1778", {"start": v(5.63, 12.93) * mm, "end": v(5.6, 12.88) * mm});
            skLineSegment(sketch, "E1779", {"start": v(5.6, 12.88) * mm, "end": v(5.57, 12.84) * mm});
            skLineSegment(sketch, "E1780", {"start": v(5.57, 12.84) * mm, "end": v(5.54, 12.8) * mm});
            skLineSegment(sketch, "E1781", {"start": v(5.54, 12.8) * mm, "end": v(5.5, 12.75) * mm});
            skLineSegment(sketch, "E1782", {"start": v(5.5, 12.75) * mm, "end": v(5.48, 12.71) * mm});
            skLineSegment(sketch, "E1783", {"start": v(5.48, 12.71) * mm, "end": v(5.46, 12.68) * mm});
            skLineSegment(sketch, "E1784", {"start": v(5.46, 12.68) * mm, "end": v(5.44, 12.64) * mm});
            skLineSegment(sketch, "E1785", {"start": v(5.44, 12.64) * mm, "end": v(5.43, 12.62) * mm});
            skLineSegment(sketch, "E1786", {"start": v(5.43, 12.62) * mm, "end": v(5.41, 12.6) * mm});
            skLineSegment(sketch, "E1787", {"start": v(5.41, 12.6) * mm, "end": v(5.4, 12.57) * mm});
            skLineSegment(sketch, "E1788", {"start": v(5.4, 12.57) * mm, "end": v(5.38, 12.55) * mm});
            skLineSegment(sketch, "E1789", {"start": v(5.38, 12.55) * mm, "end": v(5.37, 12.53) * mm});
            skLineSegment(sketch, "E1790", {"start": v(5.37, 12.53) * mm, "end": v(5.35, 12.52) * mm});
            skLineSegment(sketch, "E1791", {"start": v(5.35, 12.52) * mm, "end": v(5.34, 12.51) * mm});
            skLineSegment(sketch, "E1792", {"start": v(5.34, 12.51) * mm, "end": v(5.32, 12.5) * mm});
            skLineSegment(sketch, "E1793", {"start": v(5.32, 12.5) * mm, "end": v(5.3, 12.5) * mm});
            skLineSegment(sketch, "E1794", {"start": v(5.3, 12.5) * mm, "end": v(5.3, 12.5) * mm});
            skLineSegment(sketch, "E1795", {"start": v(5.3, 12.5) * mm, "end": v(5.11, 12.57) * mm});
            skLineSegment(sketch, "E1796", {"start": v(5.11, 12.57) * mm, "end": v(4.91, 12.63) * mm});
            skLineSegment(sketch, "E1797", {"start": v(4.91, 12.63) * mm, "end": v(4.73, 12.69) * mm});
            skLineSegment(sketch, "E1798", {"start": v(4.73, 12.69) * mm, "end": v(4.72, 12.7) * mm});
            skLineSegment(sketch, "E1799", {"start": v(4.72, 12.7) * mm, "end": v(4.7, 12.7) * mm});
            skLineSegment(sketch, "E1800", {"start": v(4.7, 12.7) * mm, "end": v(4.7, 12.72) * mm});
            skLineSegment(sketch, "E1801", {"start": v(4.7, 12.72) * mm, "end": v(4.7, 12.73) * mm});
            skLineSegment(sketch, "E1802", {"start": v(4.7, 12.73) * mm, "end": v(4.7, 12.75) * mm});
            skLineSegment(sketch, "E1803", {"start": v(4.7, 12.75) * mm, "end": v(4.69, 12.78) * mm});
            skLineSegment(sketch, "E1804", {"start": v(4.69, 12.78) * mm, "end": v(4.69, 12.8) * mm});
            skLineSegment(sketch, "E1805", {"start": v(4.69, 12.8) * mm, "end": v(4.69, 12.83) * mm});
            skLineSegment(sketch, "E1806", {"start": v(4.69, 12.83) * mm, "end": v(4.7, 12.86) * mm});
            skLineSegment(sketch, "E1807", {"start": v(4.7, 12.86) * mm, "end": v(4.7, 12.88) * mm});
            skLineSegment(sketch, "E1808", {"start": v(4.7, 12.88) * mm, "end": v(4.7, 12.92) * mm});
            skLineSegment(sketch, "E1809", {"start": v(4.7, 12.92) * mm, "end": v(4.7, 12.97) * mm});
            skLineSegment(sketch, "E1810", {"start": v(4.7, 12.97) * mm, "end": v(4.7, 13.01) * mm});
            skLineSegment(sketch, "E1811", {"start": v(4.7, 13.01) * mm, "end": v(4.7, 13.06) * mm});
            skLineSegment(sketch, "E1812", {"start": v(4.7, 13.06) * mm, "end": v(4.7, 13.12) * mm});
            skLineSegment(sketch, "E1813", {"start": v(4.7, 13.12) * mm, "end": v(4.7, 13.17) * mm});
            skLineSegment(sketch, "E1814", {"start": v(4.7, 13.17) * mm, "end": v(4.7, 13.23) * mm});
            skLineSegment(sketch, "E1815", {"start": v(4.7, 13.23) * mm, "end": v(4.7, 13.3) * mm});
            skLineSegment(sketch, "E1816", {"start": v(4.7, 13.3) * mm, "end": v(4.7, 13.36) * mm});
            skLineSegment(sketch, "E1817", {"start": v(4.7, 13.36) * mm, "end": v(4.7, 13.43) * mm});
            skLineSegment(sketch, "E1818", {"start": v(4.7, 13.43) * mm, "end": v(4.7, 13.5) * mm});
            skLineSegment(sketch, "E1819", {"start": v(4.7, 13.5) * mm, "end": v(4.7, 13.58) * mm});
            skLineSegment(sketch, "E1820", {"start": v(4.7, 13.58) * mm, "end": v(4.68, 13.66) * mm});
            skLineSegment(sketch, "E1821", {"start": v(4.68, 13.66) * mm, "end": v(4.68, 13.74) * mm});
            skLineSegment(sketch, "E1822", {"start": v(4.68, 13.74) * mm, "end": v(4.67, 13.82) * mm});
            skLineSegment(sketch, "E1823", {"start": v(4.67, 13.82) * mm, "end": v(4.65, 13.91) * mm});
            skLineSegment(sketch, "E1824", {"start": v(4.65, 13.91) * mm, "end": v(4.64, 14) * mm});
            skLineSegment(sketch, "E1825", {"start": v(4.64, 14) * mm, "end": v(4.62, 14.1) * mm});
            skLineSegment(sketch, "E1826", {"start": v(4.62, 14.1) * mm, "end": v(4.6, 14.16) * mm});
            skLineSegment(sketch, "E1827", {"start": v(4.6, 14.16) * mm, "end": v(4.34, 14.25) * mm});
            skLineSegment(sketch, "E1828", {"start": v(4.34, 14.25) * mm, "end": v(4.06, 14.3) * mm});
            skLineSegment(sketch, "E1829", {"start": v(4.06, 14.3) * mm, "end": v(4.02, 14.24) * mm});
            skLineSegment(sketch, "E1830", {"start": v(4.02, 14.24) * mm, "end": v(3.96, 14.17) * mm});
            skLineSegment(sketch, "E1831", {"start": v(3.96, 14.17) * mm, "end": v(3.9, 14.1) * mm});
            skLineSegment(sketch, "E1832", {"start": v(3.9, 14.1) * mm, "end": v(3.86, 14.02) * mm});
            skLineSegment(sketch, "E1833", {"start": v(3.86, 14.02) * mm, "end": v(3.8, 13.95) * mm});
            skLineSegment(sketch, "E1834", {"start": v(3.8, 13.95) * mm, "end": v(3.76, 13.88) * mm});
            skLineSegment(sketch, "E1835", {"start": v(3.76, 13.88) * mm, "end": v(3.72, 13.81) * mm});
            skLineSegment(sketch, "E1836", {"start": v(3.72, 13.81) * mm, "end": v(3.68, 13.75) * mm});
            skLineSegment(sketch, "E1837", {"start": v(3.68, 13.75) * mm, "end": v(3.64, 13.68) * mm});
            skLineSegment(sketch, "E1838", {"start": v(3.64, 13.68) * mm, "end": v(3.6, 13.62) * mm});
            skLineSegment(sketch, "E1839", {"start": v(3.6, 13.62) * mm, "end": v(3.58, 13.57) * mm});
            skLineSegment(sketch, "E1840", {"start": v(3.58, 13.57) * mm, "end": v(3.55, 13.51) * mm});
            skLineSegment(sketch, "E1841", {"start": v(3.55, 13.51) * mm, "end": v(3.52, 13.46) * mm});
            skLineSegment(sketch, "E1842", {"start": v(3.52, 13.46) * mm, "end": v(3.5, 13.4) * mm});
            skLineSegment(sketch, "E1843", {"start": v(3.5, 13.4) * mm, "end": v(3.47, 13.36) * mm});
            skLineSegment(sketch, "E1844", {"start": v(3.47, 13.36) * mm, "end": v(3.45, 13.31) * mm});
            skLineSegment(sketch, "E1845", {"start": v(3.45, 13.31) * mm, "end": v(3.44, 13.27) * mm});
            skLineSegment(sketch, "E1846", {"start": v(3.44, 13.27) * mm, "end": v(3.42, 13.23) * mm});
            skLineSegment(sketch, "E1847", {"start": v(3.42, 13.23) * mm, "end": v(3.4, 13.2) * mm});
            skLineSegment(sketch, "E1848", {"start": v(3.4, 13.2) * mm, "end": v(3.4, 13.18) * mm});
            skLineSegment(sketch, "E1849", {"start": v(3.4, 13.18) * mm, "end": v(3.38, 13.15) * mm});
            skLineSegment(sketch, "E1850", {"start": v(3.38, 13.15) * mm, "end": v(3.37, 13.12) * mm});
            skLineSegment(sketch, "E1851", {"start": v(3.37, 13.12) * mm, "end": v(3.36, 13.1) * mm});
            skLineSegment(sketch, "E1852", {"start": v(3.36, 13.1) * mm, "end": v(3.35, 13.08) * mm});
            skLineSegment(sketch, "E1853", {"start": v(3.35, 13.08) * mm, "end": v(3.33, 13.06) * mm});
            skLineSegment(sketch, "E1854", {"start": v(3.33, 13.06) * mm, "end": v(3.32, 13.05) * mm});
            skLineSegment(sketch, "E1855", {"start": v(3.32, 13.05) * mm, "end": v(3.3, 13.04) * mm});
            skLineSegment(sketch, "E1856", {"start": v(3.3, 13.04) * mm, "end": v(3.3, 13.03) * mm});
            skLineSegment(sketch, "E1857", {"start": v(3.3, 13.03) * mm, "end": v(3.29, 13.03) * mm});
            skLineSegment(sketch, "E1858", {"start": v(3.29, 13.03) * mm, "end": v(3.1, 13.07) * mm});
            skLineSegment(sketch, "E1859", {"start": v(3.1, 13.07) * mm, "end": v(2.89, 13.1) * mm});
            skLineSegment(sketch, "E1860", {"start": v(2.89, 13.1) * mm, "end": v(2.7, 13.13) * mm});
            skLineSegment(sketch, "E1861", {"start": v(2.7, 13.13) * mm, "end": v(2.68, 13.13) * mm});
            skLineSegment(sketch, "E1862", {"start": v(2.68, 13.13) * mm, "end": v(2.67, 13.14) * mm});
            skLineSegment(sketch, "E1863", {"start": v(2.67, 13.14) * mm, "end": v(2.66, 13.15) * mm});
            skLineSegment(sketch, "E1864", {"start": v(2.66, 13.15) * mm, "end": v(2.65, 13.17) * mm});
            skLineSegment(sketch, "E1865", {"start": v(2.65, 13.17) * mm, "end": v(2.65, 13.19) * mm});
            skLineSegment(sketch, "E1866", {"start": v(2.65, 13.19) * mm, "end": v(2.64, 13.2) * mm});
            skLineSegment(sketch, "E1867", {"start": v(2.64, 13.2) * mm, "end": v(2.64, 13.24) * mm});
            skLineSegment(sketch, "E1868", {"start": v(2.64, 13.24) * mm, "end": v(2.63, 13.26) * mm});
            skLineSegment(sketch, "E1869", {"start": v(2.63, 13.26) * mm, "end": v(2.63, 13.3) * mm});
            skLineSegment(sketch, "E1870", {"start": v(2.63, 13.3) * mm, "end": v(2.63, 13.32) * mm});
            skLineSegment(sketch, "E1871", {"start": v(2.63, 13.32) * mm, "end": v(2.63, 13.36) * mm});
            skLineSegment(sketch, "E1872", {"start": v(2.63, 13.36) * mm, "end": v(2.62, 13.4) * mm});
            skLineSegment(sketch, "E1873", {"start": v(2.62, 13.4) * mm, "end": v(2.62, 13.45) * mm});
            skLineSegment(sketch, "E1874", {"start": v(2.62, 13.45) * mm, "end": v(2.61, 13.5) * mm});
            skLineSegment(sketch, "E1875", {"start": v(2.61, 13.5) * mm, "end": v(2.6, 13.55) * mm});
            skLineSegment(sketch, "E1876", {"start": v(2.6, 13.55) * mm, "end": v(2.6, 13.6) * mm});
            skLineSegment(sketch, "E1877", {"start": v(2.6, 13.6) * mm, "end": v(2.59, 13.66) * mm});
            skLineSegment(sketch, "E1878", {"start": v(2.59, 13.66) * mm, "end": v(2.58, 13.72) * mm});
            skLineSegment(sketch, "E1879", {"start": v(2.58, 13.72) * mm, "end": v(2.57, 13.79) * mm});
            skLineSegment(sketch, "E1880", {"start": v(2.57, 13.79) * mm, "end": v(2.55, 13.86) * mm});
            skLineSegment(sketch, "E1881", {"start": v(2.55, 13.86) * mm, "end": v(2.54, 13.93) * mm});
            skLineSegment(sketch, "E1882", {"start": v(2.54, 13.93) * mm, "end": v(2.52, 14) * mm});
            skLineSegment(sketch, "E1883", {"start": v(2.52, 14) * mm, "end": v(2.5, 14.08) * mm});
            skLineSegment(sketch, "E1884", {"start": v(2.5, 14.08) * mm, "end": v(2.48, 14.16) * mm});
            skLineSegment(sketch, "E1885", {"start": v(2.48, 14.16) * mm, "end": v(2.45, 14.24) * mm});
            skLineSegment(sketch, "E1886", {"start": v(2.45, 14.24) * mm, "end": v(2.43, 14.33) * mm});
            skLineSegment(sketch, "E1887", {"start": v(2.43, 14.33) * mm, "end": v(2.4, 14.41) * mm});
            skLineSegment(sketch, "E1888", {"start": v(2.4, 14.41) * mm, "end": v(2.37, 14.5) * mm});
            skLineSegment(sketch, "E1889", {"start": v(2.37, 14.5) * mm, "end": v(2.35, 14.56) * mm});
            skLineSegment(sketch, "E1890", {"start": v(2.35, 14.56) * mm, "end": v(2.07, 14.6) * mm});
            skLineSegment(sketch, "E1891", {"start": v(2.07, 14.6) * mm, "end": v(1.78, 14.6) * mm});
            skLineSegment(sketch, "E1892", {"start": v(1.78, 14.6) * mm, "end": v(1.75, 14.55) * mm});
            skLineSegment(sketch, "E1893", {"start": v(1.75, 14.55) * mm, "end": v(1.7, 14.47) * mm});
            skLineSegment(sketch, "E1894", {"start": v(1.7, 14.47) * mm, "end": v(1.66, 14.39) * mm});
            skLineSegment(sketch, "E1895", {"start": v(1.66, 14.39) * mm, "end": v(1.62, 14.3) * mm});
            skLineSegment(sketch, "E1896", {"start": v(1.62, 14.3) * mm, "end": v(1.59, 14.23) * mm});
            skLineSegment(sketch, "E1897", {"start": v(1.59, 14.23) * mm, "end": v(1.55, 14.15) * mm});
            skLineSegment(sketch, "E1898", {"start": v(1.55, 14.15) * mm, "end": v(1.52, 14.08) * mm});
            skLineSegment(sketch, "E1899", {"start": v(1.52, 14.08) * mm, "end": v(1.5, 14.01) * mm});
            skLineSegment(sketch, "E1900", {"start": v(1.5, 14.01) * mm, "end": v(1.47, 13.94) * mm});
            skLineSegment(sketch, "E1901", {"start": v(1.47, 13.94) * mm, "end": v(1.44, 13.88) * mm});
            skLineSegment(sketch, "E1902", {"start": v(1.44, 13.88) * mm, "end": v(1.42, 13.82) * mm});
            skLineSegment(sketch, "E1903", {"start": v(1.42, 13.82) * mm, "end": v(1.4, 13.76) * mm});
            skLineSegment(sketch, "E1904", {"start": v(1.4, 13.76) * mm, "end": v(1.38, 13.7) * mm});
            skLineSegment(sketch, "E1905", {"start": v(1.38, 13.7) * mm, "end": v(1.36, 13.65) * mm});
            skLineSegment(sketch, "E1906", {"start": v(1.36, 13.65) * mm, "end": v(1.35, 13.6) * mm});
            skLineSegment(sketch, "E1907", {"start": v(1.35, 13.6) * mm, "end": v(1.34, 13.55) * mm});
            skLineSegment(sketch, "E1908", {"start": v(1.34, 13.55) * mm, "end": v(1.33, 13.5) * mm});
            skLineSegment(sketch, "E1909", {"start": v(1.33, 13.5) * mm, "end": v(1.32, 13.46) * mm});
            skLineSegment(sketch, "E1910", {"start": v(1.32, 13.46) * mm, "end": v(1.3, 13.42) * mm});
            skLineSegment(sketch, "E1911", {"start": v(1.3, 13.42) * mm, "end": v(1.3, 13.4) * mm});
            skLineSegment(sketch, "E1912", {"start": v(1.3, 13.4) * mm, "end": v(1.3, 13.37) * mm});
            skLineSegment(sketch, "E1913", {"start": v(1.3, 13.37) * mm, "end": v(1.29, 13.34) * mm});
            skLineSegment(sketch, "E1914", {"start": v(1.29, 13.34) * mm, "end": v(1.28, 13.32) * mm});
            skLineSegment(sketch, "E1915", {"start": v(1.28, 13.32) * mm, "end": v(1.27, 13.3) * mm});
            skLineSegment(sketch, "E1916", {"start": v(1.27, 13.3) * mm, "end": v(1.26, 13.28) * mm});
            skLineSegment(sketch, "E1917", {"start": v(1.26, 13.28) * mm, "end": v(1.25, 13.26) * mm});
            skLineSegment(sketch, "E1918", {"start": v(1.25, 13.26) * mm, "end": v(1.24, 13.25) * mm});
            skLineSegment(sketch, "E1919", {"start": v(1.24, 13.25) * mm, "end": v(1.23, 13.25) * mm});
            skLineSegment(sketch, "E1920", {"start": v(1.23, 13.25) * mm, "end": v(1.21, 13.24) * mm});
            skLineSegment(sketch, "E1921", {"start": v(1.21, 13.24) * mm, "end": v(1.02, 13.25) * mm});
            skLineSegment(sketch, "E1922", {"start": v(1.02, 13.25) * mm, "end": v(0.8, 13.25) * mm});
            skLineSegment(sketch, "E1923", {"start": v(0.8, 13.25) * mm, "end": v(0.61, 13.24) * mm});
            skLineSegment(sketch, "E1924", {"start": v(0.61, 13.24) * mm, "end": v(0.6, 13.25) * mm});
            skLineSegment(sketch, "E1925", {"start": v(0.6, 13.25) * mm, "end": v(0.6, 13.25) * mm});
            skLineSegment(sketch, "E1926", {"start": v(0.6, 13.25) * mm, "end": v(0.58, 13.26) * mm});
            skLineSegment(sketch, "E1927", {"start": v(0.58, 13.26) * mm, "end": v(0.57, 13.28) * mm});
            skLineSegment(sketch, "E1928", {"start": v(0.57, 13.28) * mm, "end": v(0.56, 13.3) * mm});
            skLineSegment(sketch, "E1929", {"start": v(0.56, 13.3) * mm, "end": v(0.55, 13.32) * mm});
            skLineSegment(sketch, "E1930", {"start": v(0.55, 13.32) * mm, "end": v(0.54, 13.34) * mm});
            skLineSegment(sketch, "E1931", {"start": v(0.54, 13.34) * mm, "end": v(0.53, 13.37) * mm});
            skLineSegment(sketch, "E1932", {"start": v(0.53, 13.37) * mm, "end": v(0.53, 13.4) * mm});
            skLineSegment(sketch, "E1933", {"start": v(0.53, 13.4) * mm, "end": v(0.52, 13.42) * mm});
            skLineSegment(sketch, "E1934", {"start": v(0.52, 13.42) * mm, "end": v(0.51, 13.46) * mm});
            skLineSegment(sketch, "E1935", {"start": v(0.51, 13.46) * mm, "end": v(0.5, 13.5) * mm});
            skLineSegment(sketch, "E1936", {"start": v(0.5, 13.5) * mm, "end": v(0.5, 13.55) * mm});
            skLineSegment(sketch, "E1937", {"start": v(0.5, 13.55) * mm, "end": v(0.48, 13.6) * mm});
            skLineSegment(sketch, "E1938", {"start": v(0.48, 13.6) * mm, "end": v(0.46, 13.65) * mm});
            skLineSegment(sketch, "E1939", {"start": v(0.46, 13.65) * mm, "end": v(0.45, 13.7) * mm});
            skLineSegment(sketch, "E1940", {"start": v(0.45, 13.7) * mm, "end": v(0.43, 13.76) * mm});
            skLineSegment(sketch, "E1941", {"start": v(0.43, 13.76) * mm, "end": v(0.4, 13.82) * mm});
            skLineSegment(sketch, "E1942", {"start": v(0.4, 13.82) * mm, "end": v(0.39, 13.88) * mm});
            skLineSegment(sketch, "E1943", {"start": v(0.39, 13.88) * mm, "end": v(0.36, 13.94) * mm});
            skLineSegment(sketch, "E1944", {"start": v(0.36, 13.94) * mm, "end": v(0.33, 14.01) * mm});
            skLineSegment(sketch, "E1945", {"start": v(0.33, 14.01) * mm, "end": v(0.3, 14.08) * mm});
            skLineSegment(sketch, "E1946", {"start": v(0.3, 14.08) * mm, "end": v(0.27, 14.15) * mm});
            skLineSegment(sketch, "E1947", {"start": v(0.27, 14.15) * mm, "end": v(0.24, 14.23) * mm});
            skLineSegment(sketch, "E1948", {"start": v(0.24, 14.23) * mm, "end": v(0.2, 14.3) * mm});
            skLineSegment(sketch, "E1949", {"start": v(0.2, 14.3) * mm, "end": v(0.16, 14.39) * mm});
            skLineSegment(sketch, "E1950", {"start": v(0.16, 14.39) * mm, "end": v(0.12, 14.47) * mm});
            skLineSegment(sketch, "E1951", {"start": v(0.12, 14.47) * mm, "end": v(0.08, 14.55) * mm});
            skLineSegment(sketch, "E1952", {"start": v(0.08, 14.55) * mm, "end": v(0.05, 14.6) * mm});
            skLineSegment(sketch, "E1953", {"start": v(0.05, 14.6) * mm, "end": v(-0.24, 14.6) * mm});
            skLineSegment(sketch, "E1954", {"start": v(-0.24, 14.6) * mm, "end": v(-0.52, 14.56) * mm});
            skLineSegment(sketch, "E1955", {"start": v(-0.52, 14.56) * mm, "end": v(-0.54, 14.5) * mm});
            skLineSegment(sketch, "E1956", {"start": v(-0.54, 14.5) * mm, "end": v(-0.57, 14.41) * mm});
            skLineSegment(sketch, "E1957", {"start": v(-0.57, 14.41) * mm, "end": v(-0.6, 14.33) * mm});
            skLineSegment(sketch, "E1958", {"start": v(-0.6, 14.33) * mm, "end": v(-0.63, 14.24) * mm});
            skLineSegment(sketch, "E1959", {"start": v(-0.63, 14.24) * mm, "end": v(-0.65, 14.16) * mm});
            skLineSegment(sketch, "E1960", {"start": v(-0.65, 14.16) * mm, "end": v(-0.67, 14.08) * mm});
            skLineSegment(sketch, "E1961", {"start": v(-0.67, 14.08) * mm, "end": v(-0.7, 14) * mm});
            skLineSegment(sketch, "E1962", {"start": v(-0.7, 14) * mm, "end": v(-0.7, 13.93) * mm});
            skLineSegment(sketch, "E1963", {"start": v(-0.7, 13.93) * mm, "end": v(-0.72, 13.86) * mm});
            skLineSegment(sketch, "E1964", {"start": v(-0.72, 13.86) * mm, "end": v(-0.74, 13.79) * mm});
            skLineSegment(sketch, "E1965", {"start": v(-0.74, 13.79) * mm, "end": v(-0.75, 13.72) * mm});
            skLineSegment(sketch, "E1966", {"start": v(-0.75, 13.72) * mm, "end": v(-0.76, 13.66) * mm});
            skLineSegment(sketch, "E1967", {"start": v(-0.76, 13.66) * mm, "end": v(-0.77, 13.6) * mm});
            skLineSegment(sketch, "E1968", {"start": v(-0.77, 13.6) * mm, "end": v(-0.78, 13.55) * mm});
            skLineSegment(sketch, "E1969", {"start": v(-0.78, 13.55) * mm, "end": v(-0.79, 13.5) * mm});
            skLineSegment(sketch, "E1970", {"start": v(-0.79, 13.5) * mm, "end": v(-0.8, 13.45) * mm});
            skLineSegment(sketch, "E1971", {"start": v(-0.8, 13.45) * mm, "end": v(-0.8, 13.4) * mm});
            skLineSegment(sketch, "E1972", {"start": v(-0.8, 13.4) * mm, "end": v(-0.8, 13.36) * mm});
            skLineSegment(sketch, "E1973", {"start": v(-0.8, 13.36) * mm, "end": v(-0.8, 13.32) * mm});
            skLineSegment(sketch, "E1974", {"start": v(-0.8, 13.32) * mm, "end": v(-0.8, 13.3) * mm});
            skLineSegment(sketch, "E1975", {"start": v(-0.8, 13.3) * mm, "end": v(-0.8, 13.26) * mm});
            skLineSegment(sketch, "E1976", {"start": v(-0.8, 13.26) * mm, "end": v(-0.8, 13.24) * mm});
            skLineSegment(sketch, "E1977", {"start": v(-0.8, 13.24) * mm, "end": v(-0.81, 13.2) * mm});
            skLineSegment(sketch, "E1978", {"start": v(-0.81, 13.2) * mm, "end": v(-0.82, 13.19) * mm});
            skLineSegment(sketch, "E1979", {"start": v(-0.82, 13.19) * mm, "end": v(-0.83, 13.17) * mm});
            skLineSegment(sketch, "E1980", {"start": v(-0.83, 13.17) * mm, "end": v(-0.83, 13.15) * mm});
            skLineSegment(sketch, "E1981", {"start": v(-0.83, 13.15) * mm, "end": v(-0.84, 13.14) * mm});
            skLineSegment(sketch, "E1982", {"start": v(-0.84, 13.14) * mm, "end": v(-0.85, 13.13) * mm});
            skLineSegment(sketch, "E1983", {"start": v(-0.85, 13.13) * mm, "end": v(-0.86, 13.13) * mm});
            skLineSegment(sketch, "E1984", {"start": v(-0.86, 13.13) * mm, "end": v(-1.06, 13.1) * mm});
            skLineSegment(sketch, "E1985", {"start": v(-1.06, 13.1) * mm, "end": v(-1.26, 13.07) * mm});
            skLineSegment(sketch, "E1986", {"start": v(-1.26, 13.07) * mm, "end": v(-1.46, 13.03) * mm});
            skLineSegment(sketch, "E1987", {"start": v(-1.46, 13.03) * mm, "end": v(-1.47, 13.03) * mm});
            skLineSegment(sketch, "E1988", {"start": v(-1.47, 13.03) * mm, "end": v(-1.48, 13.04) * mm});
            skLineSegment(sketch, "E1989", {"start": v(-1.48, 13.04) * mm, "end": v(-1.5, 13.05) * mm});
            skLineSegment(sketch, "E1990", {"start": v(-1.5, 13.05) * mm, "end": v(-1.5, 13.06) * mm});
            skLineSegment(sketch, "E1991", {"start": v(-1.5, 13.06) * mm, "end": v(-1.52, 13.08) * mm});
            skLineSegment(sketch, "E1992", {"start": v(-1.52, 13.08) * mm, "end": v(-1.53, 13.1) * mm});
            skLineSegment(sketch, "E1993", {"start": v(-1.53, 13.1) * mm, "end": v(-1.54, 13.12) * mm});
            skLineSegment(sketch, "E1994", {"start": v(-1.54, 13.12) * mm, "end": v(-1.56, 13.15) * mm});
            skLineSegment(sketch, "E1995", {"start": v(-1.56, 13.15) * mm, "end": v(-1.57, 13.18) * mm});
            skLineSegment(sketch, "E1996", {"start": v(-1.57, 13.18) * mm, "end": v(-1.58, 13.2) * mm});
            skLineSegment(sketch, "E1997", {"start": v(-1.58, 13.2) * mm, "end": v(-1.6, 13.23) * mm});
            skLineSegment(sketch, "E1998", {"start": v(-1.6, 13.23) * mm, "end": v(-1.6, 13.27) * mm});
            skLineSegment(sketch, "E1999", {"start": v(-1.6, 13.27) * mm, "end": v(-1.63, 13.31) * mm});
            skLineSegment(sketch, "E2000", {"start": v(-1.63, 13.31) * mm, "end": v(-1.65, 13.36) * mm});
            skLineSegment(sketch, "E2001", {"start": v(-1.65, 13.36) * mm, "end": v(-1.67, 13.4) * mm});
            skLineSegment(sketch, "E2002", {"start": v(-1.67, 13.4) * mm, "end": v(-1.7, 13.46) * mm});
            skLineSegment(sketch, "E2003", {"start": v(-1.7, 13.46) * mm, "end": v(-1.72, 13.51) * mm});
            skLineSegment(sketch, "E2004", {"start": v(-1.72, 13.51) * mm, "end": v(-1.75, 13.57) * mm});
            skLineSegment(sketch, "E2005", {"start": v(-1.75, 13.57) * mm, "end": v(-1.78, 13.62) * mm});
            skLineSegment(sketch, "E2006", {"start": v(-1.78, 13.62) * mm, "end": v(-1.82, 13.68) * mm});
            skLineSegment(sketch, "E2007", {"start": v(-1.82, 13.68) * mm, "end": v(-1.85, 13.75) * mm});
            skLineSegment(sketch, "E2008", {"start": v(-1.85, 13.75) * mm, "end": v(-1.9, 13.81) * mm});
            skLineSegment(sketch, "E2009", {"start": v(-1.9, 13.81) * mm, "end": v(-1.94, 13.88) * mm});
            skLineSegment(sketch, "E2010", {"start": v(-1.94, 13.88) * mm, "end": v(-1.98, 13.95) * mm});
            skLineSegment(sketch, "E2011", {"start": v(-1.98, 13.95) * mm, "end": v(-2.03, 14.02) * mm});
            skLineSegment(sketch, "E2012", {"start": v(-2.03, 14.02) * mm, "end": v(-2.08, 14.1) * mm});
            skLineSegment(sketch, "E2013", {"start": v(-2.08, 14.1) * mm, "end": v(-2.13, 14.17) * mm});
            skLineSegment(sketch, "E2014", {"start": v(-2.13, 14.17) * mm, "end": v(-2.2, 14.24) * mm});
            skLineSegment(sketch, "E2015", {"start": v(-2.2, 14.24) * mm, "end": v(-2.23, 14.3) * mm});
            skLineSegment(sketch, "E2016", {"start": v(-2.23, 14.3) * mm, "end": v(-2.51, 14.25) * mm});
            skLineSegment(sketch, "E2017", {"start": v(-2.51, 14.25) * mm, "end": v(-2.78, 14.16) * mm});
            skLineSegment(sketch, "E2018", {"start": v(-2.78, 14.16) * mm, "end": v(-2.8, 14.1) * mm});
            skLineSegment(sketch, "E2019", {"start": v(-2.8, 14.1) * mm, "end": v(-2.81, 14) * mm});
            skLineSegment(sketch, "E2020", {"start": v(-2.81, 14) * mm, "end": v(-2.82, 13.91) * mm});
            skLineSegment(sketch, "E2021", {"start": v(-2.82, 13.91) * mm, "end": v(-2.84, 13.82) * mm});
            skLineSegment(sketch, "E2022", {"start": v(-2.84, 13.82) * mm, "end": v(-2.85, 13.74) * mm});
            skLineSegment(sketch, "E2023", {"start": v(-2.85, 13.74) * mm, "end": v(-2.86, 13.66) * mm});
            skLineSegment(sketch, "E2024", {"start": v(-2.86, 13.66) * mm, "end": v(-2.86, 13.58) * mm});
            skLineSegment(sketch, "E2025", {"start": v(-2.86, 13.58) * mm, "end": v(-2.87, 13.5) * mm});
            skLineSegment(sketch, "E2026", {"start": v(-2.87, 13.5) * mm, "end": v(-2.87, 13.43) * mm});
            skLineSegment(sketch, "E2027", {"start": v(-2.87, 13.43) * mm, "end": v(-2.88, 13.36) * mm});
            skLineSegment(sketch, "E2028", {"start": v(-2.88, 13.36) * mm, "end": v(-2.88, 13.3) * mm});
            skLineSegment(sketch, "E2029", {"start": v(-2.88, 13.3) * mm, "end": v(-2.88, 13.23) * mm});
            skLineSegment(sketch, "E2030", {"start": v(-2.88, 13.23) * mm, "end": v(-2.88, 13.17) * mm});
            skLineSegment(sketch, "E2031", {"start": v(-2.88, 13.17) * mm, "end": v(-2.88, 13.12) * mm});
            skLineSegment(sketch, "E2032", {"start": v(-2.88, 13.12) * mm, "end": v(-2.88, 13.06) * mm});
            skLineSegment(sketch, "E2033", {"start": v(-2.88, 13.06) * mm, "end": v(-2.88, 13.01) * mm});
            skLineSegment(sketch, "E2034", {"start": v(-2.88, 13.01) * mm, "end": v(-2.87, 12.97) * mm});
            skLineSegment(sketch, "E2035", {"start": v(-2.87, 12.97) * mm, "end": v(-2.87, 12.92) * mm});
            skLineSegment(sketch, "E2036", {"start": v(-2.87, 12.92) * mm, "end": v(-2.87, 12.88) * mm});
            skLineSegment(sketch, "E2037", {"start": v(-2.87, 12.88) * mm, "end": v(-2.86, 12.86) * mm});
            skLineSegment(sketch, "E2038", {"start": v(-2.86, 12.86) * mm, "end": v(-2.86, 12.83) * mm});
            skLineSegment(sketch, "E2039", {"start": v(-2.86, 12.83) * mm, "end": v(-2.86, 12.8) * mm});
            skLineSegment(sketch, "E2040", {"start": v(-2.86, 12.8) * mm, "end": v(-2.86, 12.78) * mm});
            skLineSegment(sketch, "E2041", {"start": v(-2.86, 12.78) * mm, "end": v(-2.86, 12.75) * mm});
            skLineSegment(sketch, "E2042", {"start": v(-2.86, 12.75) * mm, "end": v(-2.87, 12.73) * mm});
            skLineSegment(sketch, "E2043", {"start": v(-2.87, 12.73) * mm, "end": v(-2.87, 12.72) * mm});
            skLineSegment(sketch, "E2044", {"start": v(-2.87, 12.72) * mm, "end": v(-2.88, 12.7) * mm});
            skLineSegment(sketch, "E2045", {"start": v(-2.88, 12.7) * mm, "end": v(-2.89, 12.7) * mm});
            skLineSegment(sketch, "E2046", {"start": v(-2.89, 12.7) * mm, "end": v(-2.9, 12.69) * mm});
            skLineSegment(sketch, "E2047", {"start": v(-2.9, 12.69) * mm, "end": v(-3.09, 12.63) * mm});
            skLineSegment(sketch, "E2048", {"start": v(-3.09, 12.63) * mm, "end": v(-3.28, 12.57) * mm});
            skLineSegment(sketch, "E2049", {"start": v(-3.28, 12.57) * mm, "end": v(-3.47, 12.5) * mm});
            skLineSegment(sketch, "E2050", {"start": v(-3.47, 12.5) * mm, "end": v(-3.48, 12.5) * mm});
            skLineSegment(sketch, "E2051", {"start": v(-3.48, 12.5) * mm, "end": v(-3.5, 12.5) * mm});
            skLineSegment(sketch, "E2052", {"start": v(-3.5, 12.5) * mm, "end": v(-3.5, 12.51) * mm});
            skLineSegment(sketch, "E2053", {"start": v(-3.5, 12.51) * mm, "end": v(-3.52, 12.52) * mm});
            skLineSegment(sketch, "E2054", {"start": v(-3.52, 12.52) * mm, "end": v(-3.54, 12.53) * mm});
            skLineSegment(sketch, "E2055", {"start": v(-3.54, 12.53) * mm, "end": v(-3.55, 12.55) * mm});
            skLineSegment(sketch, "E2056", {"start": v(-3.55, 12.55) * mm, "end": v(-3.57, 12.57) * mm});
            skLineSegment(sketch, "E2057", {"start": v(-3.57, 12.57) * mm, "end": v(-3.59, 12.6) * mm});
            skLineSegment(sketch, "E2058", {"start": v(-3.59, 12.6) * mm, "end": v(-3.6, 12.62) * mm});
            skLineSegment(sketch, "E2059", {"start": v(-3.6, 12.62) * mm, "end": v(-3.61, 12.64) * mm});
            skLineSegment(sketch, "E2060", {"start": v(-3.61, 12.64) * mm, "end": v(-3.63, 12.68) * mm});
            skLineSegment(sketch, "E2061", {"start": v(-3.63, 12.68) * mm, "end": v(-3.66, 12.71) * mm});
            skLineSegment(sketch, "E2062", {"start": v(-3.66, 12.71) * mm, "end": v(-3.68, 12.75) * mm});
            skLineSegment(sketch, "E2063", {"start": v(-3.68, 12.75) * mm, "end": v(-3.7, 12.8) * mm});
            skLineSegment(sketch, "E2064", {"start": v(-3.7, 12.8) * mm, "end": v(-3.74, 12.84) * mm});
            skLineSegment(sketch, "E2065", {"start": v(-3.74, 12.84) * mm, "end": v(-3.77, 12.88) * mm});
            skLineSegment(sketch, "E2066", {"start": v(-3.77, 12.88) * mm, "end": v(-3.8, 12.93) * mm});
            skLineSegment(sketch, "E2067", {"start": v(-3.8, 12.93) * mm, "end": v(-3.84, 12.98) * mm});
            skLineSegment(sketch, "E2068", {"start": v(-3.84, 12.98) * mm, "end": v(-3.88, 13.03) * mm});
            skLineSegment(sketch, "E2069", {"start": v(-3.88, 13.03) * mm, "end": v(-3.93, 13.09) * mm});
            skLineSegment(sketch, "E2070", {"start": v(-3.93, 13.09) * mm, "end": v(-3.97, 13.14) * mm});
            skLineSegment(sketch, "E2071", {"start": v(-3.97, 13.14) * mm, "end": v(-4.02, 13.2) * mm});
            skLineSegment(sketch, "E2072", {"start": v(-4.02, 13.2) * mm, "end": v(-4.07, 13.26) * mm});
            skLineSegment(sketch, "E2073", {"start": v(-4.07, 13.26) * mm, "end": v(-4.13, 13.32) * mm});
            skLineSegment(sketch, "E2074", {"start": v(-4.13, 13.32) * mm, "end": v(-4.19, 13.38) * mm});
            skLineSegment(sketch, "E2075", {"start": v(-4.19, 13.38) * mm, "end": v(-4.25, 13.45) * mm});
            skLineSegment(sketch, "E2076", {"start": v(-4.25, 13.45) * mm, "end": v(-4.32, 13.51) * mm});
            skLineSegment(sketch, "E2077", {"start": v(-4.32, 13.51) * mm, "end": v(-4.38, 13.58) * mm});
            skLineSegment(sketch, "E2078", {"start": v(-4.38, 13.58) * mm, "end": v(-4.43, 13.62) * mm});
            skLineSegment(sketch, "E2079", {"start": v(-4.43, 13.62) * mm, "end": v(-4.7, 13.54) * mm});
            skLineSegment(sketch, "E2080", {"start": v(-4.7, 13.54) * mm, "end": v(-4.95, 13.4) * mm});
            skLineSegment(sketch, "E2081", {"start": v(-4.95, 13.4) * mm, "end": v(-4.96, 13.34) * mm});
            skLineSegment(sketch, "E2082", {"start": v(-4.96, 13.34) * mm, "end": v(-4.96, 13.25) * mm});
            skLineSegment(sketch, "E2083", {"start": v(-4.96, 13.25) * mm, "end": v(-4.96, 13.16) * mm});
            skLineSegment(sketch, "E2084", {"start": v(-4.96, 13.16) * mm, "end": v(-4.96, 13.07) * mm});
            skLineSegment(sketch, "E2085", {"start": v(-4.96, 13.07) * mm, "end": v(-4.95, 12.98) * mm});
            skLineSegment(sketch, "E2086", {"start": v(-4.95, 12.98) * mm, "end": v(-4.95, 12.9) * mm});
            skLineSegment(sketch, "E2087", {"start": v(-4.95, 12.9) * mm, "end": v(-4.95, 12.82) * mm});
            skLineSegment(sketch, "E2088", {"start": v(-4.95, 12.82) * mm, "end": v(-4.94, 12.74) * mm});
            skLineSegment(sketch, "E2089", {"start": v(-4.94, 12.74) * mm, "end": v(-4.93, 12.67) * mm});
            skLineSegment(sketch, "E2090", {"start": v(-4.93, 12.67) * mm, "end": v(-4.92, 12.6) * mm});
            skLineSegment(sketch, "E2091", {"start": v(-4.92, 12.6) * mm, "end": v(-4.92, 12.54) * mm});
            skLineSegment(sketch, "E2092", {"start": v(-4.92, 12.54) * mm, "end": v(-4.9, 12.48) * mm});
            skLineSegment(sketch, "E2093", {"start": v(-4.9, 12.48) * mm, "end": v(-4.9, 12.42) * mm});
            skLineSegment(sketch, "E2094", {"start": v(-4.9, 12.42) * mm, "end": v(-4.89, 12.36) * mm});
            skLineSegment(sketch, "E2095", {"start": v(-4.89, 12.36) * mm, "end": v(-4.88, 12.3) * mm});
            skLineSegment(sketch, "E2096", {"start": v(-4.88, 12.3) * mm, "end": v(-4.87, 12.26) * mm});
            skLineSegment(sketch, "E2097", {"start": v(-4.87, 12.26) * mm, "end": v(-4.86, 12.21) * mm});
            skLineSegment(sketch, "E2098", {"start": v(-4.86, 12.21) * mm, "end": v(-4.85, 12.17) * mm});
            skLineSegment(sketch, "E2099", {"start": v(-4.85, 12.17) * mm, "end": v(-4.84, 12.13) * mm});
            skLineSegment(sketch, "E2100", {"start": v(-4.84, 12.13) * mm, "end": v(-4.83, 12.12) * mm});
            skLineSegment(sketch, "E2101", {"start": v(-4.83, 12.12) * mm, "end": v(-4.83, 12.08) * mm});
            skLineSegment(sketch, "E2102", {"start": v(-4.83, 12.08) * mm, "end": v(-4.82, 12.05) * mm});
            skLineSegment(sketch, "E2103", {"start": v(-4.82, 12.05) * mm, "end": v(-4.82, 12.03) * mm});
            skLineSegment(sketch, "E2104", {"start": v(-4.82, 12.03) * mm, "end": v(-4.82, 12) * mm});
            skLineSegment(sketch, "E2105", {"start": v(-4.82, 12) * mm, "end": v(-4.82, 11.98) * mm});
            skLineSegment(sketch, "E2106", {"start": v(-4.82, 11.98) * mm, "end": v(-4.82, 11.97) * mm});
            skLineSegment(sketch, "E2107", {"start": v(-4.82, 11.97) * mm, "end": v(-4.82, 11.95) * mm});
            skLineSegment(sketch, "E2108", {"start": v(-4.82, 11.95) * mm, "end": v(-4.83, 11.94) * mm});
            skLineSegment(sketch, "E2109", {"start": v(-4.83, 11.94) * mm, "end": v(-4.84, 11.93) * mm});
            skLineSegment(sketch, "E2110", {"start": v(-4.84, 11.93) * mm, "end": v(-5.02, 11.85) * mm});
            skLineSegment(sketch, "E2111", {"start": v(-5.02, 11.85) * mm, "end": v(-5.2, 11.75) * mm});
            skLineSegment(sketch, "E2112", {"start": v(-5.2, 11.75) * mm, "end": v(-5.38, 11.66) * mm});
            skLineSegment(sketch, "E2113", {"start": v(-5.38, 11.66) * mm, "end": v(-5.39, 11.66) * mm});
            skLineSegment(sketch, "E2114", {"start": v(-5.39, 11.66) * mm, "end": v(-5.4, 11.66) * mm});
            skLineSegment(sketch, "E2115", {"start": v(-5.4, 11.66) * mm, "end": v(-5.41, 11.66) * mm});
            skLineSegment(sketch, "E2116", {"start": v(-5.41, 11.66) * mm, "end": v(-5.43, 11.67) * mm});
            skLineSegment(sketch, "E2117", {"start": v(-5.43, 11.67) * mm, "end": v(-5.45, 11.68) * mm});
            skLineSegment(sketch, "E2118", {"start": v(-5.45, 11.68) * mm, "end": v(-5.46, 11.7) * mm});
            skLineSegment(sketch, "E2119", {"start": v(-5.46, 11.7) * mm, "end": v(-5.48, 11.72) * mm});
            skLineSegment(sketch, "E2120", {"start": v(-5.48, 11.72) * mm, "end": v(-5.5, 11.74) * mm});
            skLineSegment(sketch, "E2121", {"start": v(-5.5, 11.74) * mm, "end": v(-5.53, 11.76) * mm});
            skLineSegment(sketch, "E2122", {"start": v(-5.53, 11.76) * mm, "end": v(-5.54, 11.78) * mm});
            skLineSegment(sketch, "E2123", {"start": v(-5.54, 11.78) * mm, "end": v(-5.56, 11.8) * mm});
            skLineSegment(sketch, "E2124", {"start": v(-5.56, 11.8) * mm, "end": v(-5.6, 11.84) * mm});
            skLineSegment(sketch, "E2125", {"start": v(-5.6, 11.84) * mm, "end": v(-5.62, 11.88) * mm});
            skLineSegment(sketch, "E2126", {"start": v(-5.62, 11.88) * mm, "end": v(-5.66, 11.91) * mm});
            skLineSegment(sketch, "E2127", {"start": v(-5.66, 11.91) * mm, "end": v(-5.7, 11.95) * mm});
            skLineSegment(sketch, "E2128", {"start": v(-5.7, 11.95) * mm, "end": v(-5.73, 12) * mm});
            skLineSegment(sketch, "E2129", {"start": v(-5.73, 12) * mm, "end": v(-5.77, 12.03) * mm});
            skLineSegment(sketch, "E2130", {"start": v(-5.77, 12.03) * mm, "end": v(-5.82, 12.08) * mm});
            skLineSegment(sketch, "E2131", {"start": v(-5.82, 12.08) * mm, "end": v(-5.87, 12.12) * mm});
            skLineSegment(sketch, "E2132", {"start": v(-5.87, 12.12) * mm, "end": v(-5.92, 12.17) * mm});
            skLineSegment(sketch, "E2133", {"start": v(-5.92, 12.17) * mm, "end": v(-5.97, 12.22) * mm});
            skLineSegment(sketch, "E2134", {"start": v(-5.97, 12.22) * mm, "end": v(-6.03, 12.27) * mm});
            skLineSegment(sketch, "E2135", {"start": v(-6.03, 12.27) * mm, "end": v(-6.1, 12.32) * mm});
            skLineSegment(sketch, "E2136", {"start": v(-6.1, 12.32) * mm, "end": v(-6.15, 12.37) * mm});
            skLineSegment(sketch, "E2137", {"start": v(-6.15, 12.37) * mm, "end": v(-6.22, 12.42) * mm});
            skLineSegment(sketch, "E2138", {"start": v(-6.22, 12.42) * mm, "end": v(-6.3, 12.48) * mm});
            skLineSegment(sketch, "E2139", {"start": v(-6.3, 12.48) * mm, "end": v(-6.37, 12.53) * mm});
            skLineSegment(sketch, "E2140", {"start": v(-6.37, 12.53) * mm, "end": v(-6.45, 12.58) * mm});
            skLineSegment(sketch, "E2141", {"start": v(-6.45, 12.58) * mm, "end": v(-6.5, 12.62) * mm});
            skLineSegment(sketch, "E2142", {"start": v(-6.5, 12.62) * mm, "end": v(-6.75, 12.5) * mm});
            skLineSegment(sketch, "E2143", {"start": v(-6.75, 12.5) * mm, "end": v(-6.98, 12.32) * mm});
            skLineSegment(sketch, "E2144", {"start": v(-6.98, 12.32) * mm, "end": v(-6.97, 12.26) * mm});
            skLineSegment(sketch, "E2145", {"start": v(-6.97, 12.26) * mm, "end": v(-6.96, 12.17) * mm});
            skLineSegment(sketch, "E2146", {"start": v(-6.96, 12.17) * mm, "end": v(-6.95, 12.07) * mm});
            skLineSegment(sketch, "E2147", {"start": v(-6.95, 12.07) * mm, "end": v(-6.93, 11.99) * mm});
            skLineSegment(sketch, "E2148", {"start": v(-6.93, 11.99) * mm, "end": v(-6.92, 11.9) * mm});
            skLineSegment(sketch, "E2149", {"start": v(-6.92, 11.9) * mm, "end": v(-6.9, 11.82) * mm});
            skLineSegment(sketch, "E2150", {"start": v(-6.9, 11.82) * mm, "end": v(-6.88, 11.75) * mm});
            skLineSegment(sketch, "E2151", {"start": v(-6.88, 11.75) * mm, "end": v(-6.86, 11.67) * mm});
            skLineSegment(sketch, "E2152", {"start": v(-6.86, 11.67) * mm, "end": v(-6.85, 11.6) * mm});
            skLineSegment(sketch, "E2153", {"start": v(-6.85, 11.6) * mm, "end": v(-6.83, 11.53) * mm});
            skLineSegment(sketch, "E2154", {"start": v(-6.83, 11.53) * mm, "end": v(-6.8, 11.47) * mm});
            skLineSegment(sketch, "E2155", {"start": v(-6.8, 11.47) * mm, "end": v(-6.8, 11.41) * mm});
            skLineSegment(sketch, "E2156", {"start": v(-6.8, 11.41) * mm, "end": v(-6.77, 11.35) * mm});
            skLineSegment(sketch, "E2157", {"start": v(-6.77, 11.35) * mm, "end": v(-6.75, 11.3) * mm});
            skLineSegment(sketch, "E2158", {"start": v(-6.75, 11.3) * mm, "end": v(-6.74, 11.25) * mm});
            skLineSegment(sketch, "E2159", {"start": v(-6.74, 11.25) * mm, "end": v(-6.72, 11.2) * mm});
            skLineSegment(sketch, "E2160", {"start": v(-6.72, 11.2) * mm, "end": v(-6.7, 11.16) * mm});
            skLineSegment(sketch, "E2161", {"start": v(-6.7, 11.16) * mm, "end": v(-6.68, 11.12) * mm});
            skLineSegment(sketch, "E2162", {"start": v(-6.68, 11.12) * mm, "end": v(-6.67, 11.08) * mm});
            skLineSegment(sketch, "E2163", {"start": v(-6.67, 11.08) * mm, "end": v(-6.66, 11.07) * mm});
            skLineSegment(sketch, "E2164", {"start": v(-6.66, 11.07) * mm, "end": v(-6.65, 11.04) * mm});
            skLineSegment(sketch, "E2165", {"start": v(-6.65, 11.04) * mm, "end": v(-6.64, 11) * mm});
            skLineSegment(sketch, "E2166", {"start": v(-6.64, 11) * mm, "end": v(-6.63, 10.98) * mm});
            skLineSegment(sketch, "E2167", {"start": v(-6.63, 10.98) * mm, "end": v(-6.63, 10.96) * mm});
            skLineSegment(sketch, "E2168", {"start": v(-6.63, 10.96) * mm, "end": v(-6.62, 10.94) * mm});
            skLineSegment(sketch, "E2169", {"start": v(-6.62, 10.94) * mm, "end": v(-6.62, 10.92) * mm});
            skLineSegment(sketch, "E2170", {"start": v(-6.62, 10.92) * mm, "end": v(-6.63, 10.9) * mm});
            skLineSegment(sketch, "E2171", {"start": v(-6.63, 10.9) * mm, "end": v(-6.63, 10.9) * mm});
            skLineSegment(sketch, "E2172", {"start": v(-6.63, 10.9) * mm, "end": v(-6.64, 10.89) * mm});
            skLineSegment(sketch, "E2173", {"start": v(-6.64, 10.89) * mm, "end": v(-6.8, 10.77) * mm});
            skLineSegment(sketch, "E2174", {"start": v(-6.8, 10.77) * mm, "end": v(-6.97, 10.65) * mm});
            skLineSegment(sketch, "E2175", {"start": v(-6.97, 10.65) * mm, "end": v(-7.13, 10.53) * mm});
            skLineSegment(sketch, "E2176", {"start": v(-7.13, 10.53) * mm, "end": v(-7.14, 10.53) * mm});
            skLineSegment(sketch, "E2177", {"start": v(-7.14, 10.53) * mm, "end": v(-7.15, 10.53) * mm});
            skLineSegment(sketch, "E2178", {"start": v(-7.15, 10.53) * mm, "end": v(-7.16, 10.53) * mm});
            skLineSegment(sketch, "E2179", {"start": v(-7.16, 10.53) * mm, "end": v(-7.18, 10.54) * mm});
            skLineSegment(sketch, "E2180", {"start": v(-7.18, 10.54) * mm, "end": v(-7.2, 10.54) * mm});
            skLineSegment(sketch, "E2181", {"start": v(-7.2, 10.54) * mm, "end": v(-7.22, 10.56) * mm});
            skLineSegment(sketch, "E2182", {"start": v(-7.22, 10.56) * mm, "end": v(-7.24, 10.57) * mm});
            skLineSegment(sketch, "E2183", {"start": v(-7.24, 10.57) * mm, "end": v(-7.26, 10.59) * mm});
            skLineSegment(sketch, "E2184", {"start": v(-7.26, 10.59) * mm, "end": v(-7.29, 10.6) * mm});
            skLineSegment(sketch, "E2185", {"start": v(-7.29, 10.6) * mm, "end": v(-7.3, 10.62) * mm});
            skLineSegment(sketch, "E2186", {"start": v(-7.3, 10.62) * mm, "end": v(-7.33, 10.65) * mm});
            skLineSegment(sketch, "E2187", {"start": v(-7.33, 10.65) * mm, "end": v(-7.37, 10.68) * mm});
            skLineSegment(sketch, "E2188", {"start": v(-7.37, 10.68) * mm, "end": v(-7.4, 10.7) * mm});
            skLineSegment(sketch, "E2189", {"start": v(-7.4, 10.7) * mm, "end": v(-7.44, 10.74) * mm});
            skLineSegment(sketch, "E2190", {"start": v(-7.44, 10.74) * mm, "end": v(-7.48, 10.77) * mm});
            skLineSegment(sketch, "E2191", {"start": v(-7.48, 10.77) * mm, "end": v(-7.53, 10.8) * mm});
            skLineSegment(sketch, "E2192", {"start": v(-7.53, 10.8) * mm, "end": v(-7.58, 10.84) * mm});
            skLineSegment(sketch, "E2193", {"start": v(-7.58, 10.84) * mm, "end": v(-7.63, 10.88) * mm});
            skLineSegment(sketch, "E2194", {"start": v(-7.63, 10.88) * mm, "end": v(-7.68, 10.91) * mm});
            skLineSegment(sketch, "E2195", {"start": v(-7.68, 10.91) * mm, "end": v(-7.74, 10.95) * mm});
            skLineSegment(sketch, "E2196", {"start": v(-7.74, 10.95) * mm, "end": v(-7.8, 10.99) * mm});
            skLineSegment(sketch, "E2197", {"start": v(-7.8, 10.99) * mm, "end": v(-7.87, 11.03) * mm});
            skLineSegment(sketch, "E2198", {"start": v(-7.87, 11.03) * mm, "end": v(-7.93, 11.07) * mm});
            skLineSegment(sketch, "E2199", {"start": v(-7.93, 11.07) * mm, "end": v(-8, 11.11) * mm});
            skLineSegment(sketch, "E2200", {"start": v(-8, 11.11) * mm, "end": v(-8.08, 11.15) * mm});
            skLineSegment(sketch, "E2201", {"start": v(-8.08, 11.15) * mm, "end": v(-8.16, 11.2) * mm});
            skLineSegment(sketch, "E2202", {"start": v(-8.16, 11.2) * mm, "end": v(-8.24, 11.24) * mm});
            skLineSegment(sketch, "E2203", {"start": v(-8.24, 11.24) * mm, "end": v(-8.33, 11.28) * mm});
            skLineSegment(sketch, "E2204", {"start": v(-8.33, 11.28) * mm, "end": v(-8.39, 11.3) * mm});
            skLineSegment(sketch, "E2205", {"start": v(-8.39, 11.3) * mm, "end": v(-8.62, 11.14) * mm});
            skLineSegment(sketch, "E2206", {"start": v(-8.62, 11.14) * mm, "end": v(-8.82, 10.94) * mm});
            skLineSegment(sketch, "E2207", {"start": v(-8.82, 10.94) * mm, "end": v(-8.8, 10.87) * mm});
            skLineSegment(sketch, "E2208", {"start": v(-8.8, 10.87) * mm, "end": v(-8.77, 10.78) * mm});
            skLineSegment(sketch, "E2209", {"start": v(-8.77, 10.78) * mm, "end": v(-8.74, 10.7) * mm});
            skLineSegment(sketch, "E2210", {"start": v(-8.74, 10.7) * mm, "end": v(-8.71, 10.61) * mm});
            skLineSegment(sketch, "E2211", {"start": v(-8.71, 10.61) * mm, "end": v(-8.68, 10.53) * mm});
            skLineSegment(sketch, "E2212", {"start": v(-8.68, 10.53) * mm, "end": v(-8.66, 10.45) * mm});
            skLineSegment(sketch, "E2213", {"start": v(-8.66, 10.45) * mm, "end": v(-8.63, 10.38) * mm});
            skLineSegment(sketch, "E2214", {"start": v(-8.63, 10.38) * mm, "end": v(-8.6, 10.31) * mm});
            skLineSegment(sketch, "E2215", {"start": v(-8.6, 10.31) * mm, "end": v(-8.57, 10.24) * mm});
            skLineSegment(sketch, "E2216", {"start": v(-8.57, 10.24) * mm, "end": v(-8.54, 10.18) * mm});
            skLineSegment(sketch, "E2217", {"start": v(-8.54, 10.18) * mm, "end": v(-8.51, 10.12) * mm});
            skLineSegment(sketch, "E2218", {"start": v(-8.51, 10.12) * mm, "end": v(-8.48, 10.06) * mm});
            skLineSegment(sketch, "E2219", {"start": v(-8.48, 10.06) * mm, "end": v(-8.46, 10.01) * mm});
            skLineSegment(sketch, "E2220", {"start": v(-8.46, 10.01) * mm, "end": v(-8.43, 9.96) * mm});
            skLineSegment(sketch, "E2221", {"start": v(-8.43, 9.96) * mm, "end": v(-8.4, 9.92) * mm});
            skLineSegment(sketch, "E2222", {"start": v(-8.4, 9.92) * mm, "end": v(-8.38, 9.87) * mm});
            skLineSegment(sketch, "E2223", {"start": v(-8.38, 9.87) * mm, "end": v(-8.36, 9.83) * mm});
            skLineSegment(sketch, "E2224", {"start": v(-8.36, 9.83) * mm, "end": v(-8.33, 9.8) * mm});
            skLineSegment(sketch, "E2225", {"start": v(-8.33, 9.8) * mm, "end": v(-8.31, 9.76) * mm});
            skLineSegment(sketch, "E2226", {"start": v(-8.31, 9.76) * mm, "end": v(-8.3, 9.75) * mm});
            skLineSegment(sketch, "E2227", {"start": v(-8.3, 9.75) * mm, "end": v(-8.28, 9.72) * mm});
            skLineSegment(sketch, "E2228", {"start": v(-8.28, 9.72) * mm, "end": v(-8.27, 9.7) * mm});
            skLineSegment(sketch, "E2229", {"start": v(-8.27, 9.7) * mm, "end": v(-8.26, 9.67) * mm});
            skLineSegment(sketch, "E2230", {"start": v(-8.26, 9.67) * mm, "end": v(-8.25, 9.65) * mm});
            skLineSegment(sketch, "E2231", {"start": v(-8.25, 9.65) * mm, "end": v(-8.25, 9.63) * mm});
            skLineSegment(sketch, "E2232", {"start": v(-8.25, 9.63) * mm, "end": v(-8.24, 9.6) * mm});
            skLineSegment(sketch, "E2233", {"start": v(-8.24, 9.6) * mm, "end": v(-8.24, 9.6) * mm});
            skLineSegment(sketch, "E2234", {"start": v(-8.24, 9.6) * mm, "end": v(-8.25, 9.58) * mm});
            skLineSegment(sketch, "E2235", {"start": v(-8.25, 9.58) * mm, "end": v(-8.25, 9.57) * mm});
            skLineSegment(sketch, "E2236", {"start": v(-8.25, 9.57) * mm, "end": v(-8.4, 9.43) * mm});
            skLineSegment(sketch, "E2237", {"start": v(-8.4, 9.43) * mm, "end": v(-8.54, 9.29) * mm});
            skLineSegment(sketch, "E2238", {"start": v(-8.54, 9.29) * mm, "end": v(-8.68, 9.15) * mm});
            skLineSegment(sketch, "E2239", {"start": v(-8.68, 9.15) * mm, "end": v(-8.69, 9.14) * mm});
            skLineSegment(sketch, "E2240", {"start": v(-8.69, 9.14) * mm, "end": v(-8.7, 9.14) * mm});
            skLineSegment(sketch, "E2241", {"start": v(-8.7, 9.14) * mm, "end": v(-8.71, 9.14) * mm});
            skLineSegment(sketch, "E2242", {"start": v(-8.71, 9.14) * mm, "end": v(-8.73, 9.14) * mm});
            skLineSegment(sketch, "E2243", {"start": v(-8.73, 9.14) * mm, "end": v(-8.75, 9.15) * mm});
            skLineSegment(sketch, "E2244", {"start": v(-8.75, 9.15) * mm, "end": v(-8.77, 9.15) * mm});
            skLineSegment(sketch, "E2245", {"start": v(-8.77, 9.15) * mm, "end": v(-8.8, 9.16) * mm});
            skLineSegment(sketch, "E2246", {"start": v(-8.8, 9.16) * mm, "end": v(-8.82, 9.18) * mm});
            skLineSegment(sketch, "E2247", {"start": v(-8.82, 9.18) * mm, "end": v(-8.85, 9.2) * mm});
            skLineSegment(sketch, "E2248", {"start": v(-8.85, 9.2) * mm, "end": v(-8.87, 9.2) * mm});
            skLineSegment(sketch, "E2249", {"start": v(-8.87, 9.2) * mm, "end": v(-8.9, 9.23) * mm});
            skLineSegment(sketch, "E2250", {"start": v(-8.9, 9.23) * mm, "end": v(-8.94, 9.25) * mm});
            skLineSegment(sketch, "E2251", {"start": v(-8.94, 9.25) * mm, "end": v(-8.98, 9.27) * mm});
            skLineSegment(sketch, "E2252", {"start": v(-8.98, 9.27) * mm, "end": v(-9.02, 9.3) * mm});
            skLineSegment(sketch, "E2253", {"start": v(-9.02, 9.3) * mm, "end": v(-9.07, 9.32) * mm});
            skLineSegment(sketch, "E2254", {"start": v(-9.07, 9.32) * mm, "end": v(-9.12, 9.35) * mm});
            skLineSegment(sketch, "E2255", {"start": v(-9.12, 9.35) * mm, "end": v(-9.17, 9.38) * mm});
            skLineSegment(sketch, "E2256", {"start": v(-9.17, 9.38) * mm, "end": v(-9.23, 9.4) * mm});
            skLineSegment(sketch, "E2257", {"start": v(-9.23, 9.4) * mm, "end": v(-9.29, 9.43) * mm});
            skLineSegment(sketch, "E2258", {"start": v(-9.29, 9.43) * mm, "end": v(-9.35, 9.46) * mm});
            skLineSegment(sketch, "E2259", {"start": v(-9.35, 9.46) * mm, "end": v(-9.42, 9.5) * mm});
            skLineSegment(sketch, "E2260", {"start": v(-9.42, 9.5) * mm, "end": v(-9.49, 9.52) * mm});
            skLineSegment(sketch, "E2261", {"start": v(-9.49, 9.52) * mm, "end": v(-9.56, 9.55) * mm});
            skLineSegment(sketch, "E2262", {"start": v(-9.56, 9.55) * mm, "end": v(-9.64, 9.58) * mm});
            skLineSegment(sketch, "E2263", {"start": v(-9.64, 9.58) * mm, "end": v(-9.72, 9.6) * mm});
            skLineSegment(sketch, "E2264", {"start": v(-9.72, 9.6) * mm, "end": v(-9.8, 9.64) * mm});
            skLineSegment(sketch, "E2265", {"start": v(-9.8, 9.64) * mm, "end": v(-9.89, 9.66) * mm});
            skLineSegment(sketch, "E2266", {"start": v(-9.89, 9.66) * mm, "end": v(-9.98, 9.7) * mm});
            skLineSegment(sketch, "E2267", {"start": v(-9.98, 9.7) * mm, "end": v(-10.04, 9.71) * mm});
            skLineSegment(sketch, "E2268", {"start": v(-10.04, 9.71) * mm, "end": v(-10.24, 9.5) * mm});
            skLineSegment(sketch, "E2269", {"start": v(-10.24, 9.5) * mm, "end": v(-10.41, 9.28) * mm});
            skLineSegment(sketch, "E2270", {"start": v(-10.41, 9.28) * mm, "end": v(-10.38, 9.22) * mm});
            skLineSegment(sketch, "E2271", {"start": v(-10.38, 9.22) * mm, "end": v(-10.34, 9.14) * mm});
            skLineSegment(sketch, "E2272", {"start": v(-10.34, 9.14) * mm, "end": v(-10.3, 9.05) * mm});
            skLineSegment(sketch, "E2273", {"start": v(-10.3, 9.05) * mm, "end": v(-10.26, 8.98) * mm});
            skLineSegment(sketch, "E2274", {"start": v(-10.26, 8.98) * mm, "end": v(-10.22, 8.9) * mm});
            skLineSegment(sketch, "E2275", {"start": v(-10.22, 8.9) * mm, "end": v(-10.18, 8.83) * mm});
            skLineSegment(sketch, "E2276", {"start": v(-10.18, 8.83) * mm, "end": v(-10.14, 8.76) * mm});
            skLineSegment(sketch, "E2277", {"start": v(-10.14, 8.76) * mm, "end": v(-10.1, 8.7) * mm});
            skLineSegment(sketch, "E2278", {"start": v(-10.1, 8.7) * mm, "end": v(-10.06, 8.63) * mm});
            skLineSegment(sketch, "E2279", {"start": v(-10.06, 8.63) * mm, "end": v(-10.02, 8.58) * mm});
            skLineSegment(sketch, "E2280", {"start": v(-10.02, 8.58) * mm, "end": v(-9.98, 8.52) * mm});
            skLineSegment(sketch, "E2281", {"start": v(-9.98, 8.52) * mm, "end": v(-9.95, 8.47) * mm});
            skLineSegment(sketch, "E2282", {"start": v(-9.95, 8.47) * mm, "end": v(-9.91, 8.42) * mm});
            skLineSegment(sketch, "E2283", {"start": v(-9.91, 8.42) * mm, "end": v(-9.88, 8.38) * mm});
            skLineSegment(sketch, "E2284", {"start": v(-9.88, 8.38) * mm, "end": v(-9.84, 8.34) * mm});
            skLineSegment(sketch, "E2285", {"start": v(-9.84, 8.34) * mm, "end": v(-9.81, 8.3) * mm});
            skLineSegment(sketch, "E2286", {"start": v(-9.81, 8.3) * mm, "end": v(-9.78, 8.26) * mm});
            skLineSegment(sketch, "E2287", {"start": v(-9.78, 8.26) * mm, "end": v(-9.76, 8.23) * mm});
            skLineSegment(sketch, "E2288", {"start": v(-9.76, 8.23) * mm, "end": v(-9.73, 8.2) * mm});
            skLineSegment(sketch, "E2289", {"start": v(-9.73, 8.2) * mm, "end": v(-9.72, 8.18) * mm});
            skLineSegment(sketch, "E2290", {"start": v(-9.72, 8.18) * mm, "end": v(-9.7, 8.16) * mm});
            skLineSegment(sketch, "E2291", {"start": v(-9.7, 8.16) * mm, "end": v(-9.68, 8.14) * mm});
            skLineSegment(sketch, "E2292", {"start": v(-9.68, 8.14) * mm, "end": v(-9.66, 8.11) * mm});
            skLineSegment(sketch, "E2293", {"start": v(-9.66, 8.11) * mm, "end": v(-9.65, 8.1) * mm});
            skLineSegment(sketch, "E2294", {"start": v(-9.65, 8.1) * mm, "end": v(-9.64, 8.07) * mm});
            skLineSegment(sketch, "E2295", {"start": v(-9.64, 8.07) * mm, "end": v(-9.64, 8.06) * mm});
            skLineSegment(sketch, "E2296", {"start": v(-9.64, 8.06) * mm, "end": v(-9.63, 8.04) * mm});
            skLineSegment(sketch, "E2297", {"start": v(-9.63, 8.04) * mm, "end": v(-9.64, 8.03) * mm});
            skLineSegment(sketch, "E2298", {"start": v(-9.64, 8.03) * mm, "end": v(-9.64, 8.02) * mm});
            skLineSegment(sketch, "E2299", {"start": v(-9.64, 8.02) * mm, "end": v(-9.76, 7.86) * mm});
            skLineSegment(sketch, "E2300", {"start": v(-9.76, 7.86) * mm, "end": v(-9.88, 7.7) * mm});
            skLineSegment(sketch, "E2301", {"start": v(-9.88, 7.7) * mm, "end": v(-10, 7.53) * mm});
            skLineSegment(sketch, "E2302", {"start": v(-10, 7.53) * mm, "end": v(-10, 7.53) * mm});
            skLineSegment(sketch, "E2303", {"start": v(-10, 7.53) * mm, "end": v(-10.01, 7.52) * mm});
            skLineSegment(sketch, "E2304", {"start": v(-10.01, 7.52) * mm, "end": v(-10.03, 7.52) * mm});
            skLineSegment(sketch, "E2305", {"start": v(-10.03, 7.52) * mm, "end": v(-10.05, 7.52) * mm});
            skLineSegment(sketch, "E2306", {"start": v(-10.05, 7.52) * mm, "end": v(-10.07, 7.52) * mm});
            skLineSegment(sketch, "E2307", {"start": v(-10.07, 7.52) * mm, "end": v(-10.09, 7.52) * mm});
            skLineSegment(sketch, "E2308", {"start": v(-10.09, 7.52) * mm, "end": v(-10.11, 7.53) * mm});
            skLineSegment(sketch, "E2309", {"start": v(-10.11, 7.53) * mm, "end": v(-10.14, 7.54) * mm});
            skLineSegment(sketch, "E2310", {"start": v(-10.14, 7.54) * mm, "end": v(-10.17, 7.55) * mm});
            skLineSegment(sketch, "E2311", {"start": v(-10.17, 7.55) * mm, "end": v(-10.2, 7.56) * mm});
            skLineSegment(sketch, "E2312", {"start": v(-10.2, 7.56) * mm, "end": v(-10.23, 7.58) * mm});
            skLineSegment(sketch, "E2313", {"start": v(-10.23, 7.58) * mm, "end": v(-10.27, 7.6) * mm});
            skLineSegment(sketch, "E2314", {"start": v(-10.27, 7.6) * mm, "end": v(-10.31, 7.61) * mm});
            skLineSegment(sketch, "E2315", {"start": v(-10.31, 7.61) * mm, "end": v(-10.36, 7.63) * mm});
            skLineSegment(sketch, "E2316", {"start": v(-10.36, 7.63) * mm, "end": v(-10.4, 7.65) * mm});
            skLineSegment(sketch, "E2317", {"start": v(-10.4, 7.65) * mm, "end": v(-10.46, 7.67) * mm});
            skLineSegment(sketch, "E2318", {"start": v(-10.46, 7.67) * mm, "end": v(-10.52, 7.68) * mm});
            skLineSegment(sketch, "E2319", {"start": v(-10.52, 7.68) * mm, "end": v(-10.58, 7.7) * mm});
            skLineSegment(sketch, "E2320", {"start": v(-10.58, 7.7) * mm, "end": v(-10.64, 7.72) * mm});
            skLineSegment(sketch, "E2321", {"start": v(-10.64, 7.72) * mm, "end": v(-10.7, 7.74) * mm});
            skLineSegment(sketch, "E2322", {"start": v(-10.7, 7.74) * mm, "end": v(-10.78, 7.76) * mm});
            skLineSegment(sketch, "E2323", {"start": v(-10.78, 7.76) * mm, "end": v(-10.85, 7.78) * mm});
            skLineSegment(sketch, "E2324", {"start": v(-10.85, 7.78) * mm, "end": v(-10.93, 7.8) * mm});
            skLineSegment(sketch, "E2325", {"start": v(-10.93, 7.8) * mm, "end": v(-11, 7.8) * mm});
            skLineSegment(sketch, "E2326", {"start": v(-11, 7.8) * mm, "end": v(-11.1, 7.83) * mm});
            skLineSegment(sketch, "E2327", {"start": v(-11.1, 7.83) * mm, "end": v(-11.18, 7.84) * mm});
            skLineSegment(sketch, "E2328", {"start": v(-11.18, 7.84) * mm, "end": v(-11.27, 7.86) * mm});
            skLineSegment(sketch, "E2329", {"start": v(-11.27, 7.86) * mm, "end": v(-11.37, 7.87) * mm});
            skLineSegment(sketch, "E2330", {"start": v(-11.37, 7.87) * mm, "end": v(-11.43, 7.88) * mm});
            skLineSegment(sketch, "E2331", {"start": v(-11.43, 7.88) * mm, "end": v(-11.6, 7.65) * mm});
            skLineSegment(sketch, "E2332", {"start": v(-11.6, 7.65) * mm, "end": v(-11.73, 7.4) * mm});
            skLineSegment(sketch, "E2333", {"start": v(-11.73, 7.4) * mm, "end": v(-11.69, 7.34) * mm});
            skLineSegment(sketch, "E2334", {"start": v(-11.69, 7.34) * mm, "end": v(-11.63, 7.26) * mm});
            skLineSegment(sketch, "E2335", {"start": v(-11.63, 7.26) * mm, "end": v(-11.58, 7.19) * mm});
            skLineSegment(sketch, "E2336", {"start": v(-11.58, 7.19) * mm, "end": v(-11.53, 7.12) * mm});
            skLineSegment(sketch, "E2337", {"start": v(-11.53, 7.12) * mm, "end": v(-11.47, 7.05) * mm});
            skLineSegment(sketch, "E2338", {"start": v(-11.47, 7.05) * mm, "end": v(-11.42, 6.98) * mm});
            skLineSegment(sketch, "E2339", {"start": v(-11.42, 6.98) * mm, "end": v(-11.37, 6.92) * mm});
            skLineSegment(sketch, "E2340", {"start": v(-11.37, 6.92) * mm, "end": v(-11.32, 6.87) * mm});
            skLineSegment(sketch, "E2341", {"start": v(-11.32, 6.87) * mm, "end": v(-11.28, 6.81) * mm});
            skLineSegment(sketch, "E2342", {"start": v(-11.28, 6.81) * mm, "end": v(-11.23, 6.76) * mm});
            skLineSegment(sketch, "E2343", {"start": v(-11.23, 6.76) * mm, "end": v(-11.18, 6.71) * mm});
            skLineSegment(sketch, "E2344", {"start": v(-11.18, 6.71) * mm, "end": v(-11.14, 6.67) * mm});
            skLineSegment(sketch, "E2345", {"start": v(-11.14, 6.67) * mm, "end": v(-11.1, 6.63) * mm});
            skLineSegment(sketch, "E2346", {"start": v(-11.1, 6.63) * mm, "end": v(-11.06, 6.59) * mm});
            skLineSegment(sketch, "E2347", {"start": v(-11.06, 6.59) * mm, "end": v(-11.02, 6.55) * mm});
            skLineSegment(sketch, "E2348", {"start": v(-11.02, 6.55) * mm, "end": v(-10.98, 6.52) * mm});
            skLineSegment(sketch, "E2349", {"start": v(-10.98, 6.52) * mm, "end": v(-10.95, 6.49) * mm});
            skLineSegment(sketch, "E2350", {"start": v(-10.95, 6.49) * mm, "end": v(-10.91, 6.46) * mm});
            skLineSegment(sketch, "E2351", {"start": v(-10.91, 6.46) * mm, "end": v(-10.88, 6.43) * mm});
            skLineSegment(sketch, "E2352", {"start": v(-10.88, 6.43) * mm, "end": v(-10.87, 6.42) * mm});
            skLineSegment(sketch, "E2353", {"start": v(-10.87, 6.42) * mm, "end": v(-10.84, 6.4) * mm});
            skLineSegment(sketch, "E2354", {"start": v(-10.84, 6.4) * mm, "end": v(-10.82, 6.38) * mm});
            skLineSegment(sketch, "E2355", {"start": v(-10.82, 6.38) * mm, "end": v(-10.8, 6.36) * mm});
            skLineSegment(sketch, "E2356", {"start": v(-10.8, 6.36) * mm, "end": v(-10.79, 6.34) * mm});
            skLineSegment(sketch, "E2357", {"start": v(-10.79, 6.34) * mm, "end": v(-10.78, 6.32) * mm});
            skLineSegment(sketch, "E2358", {"start": v(-10.78, 6.32) * mm, "end": v(-10.77, 6.3) * mm});
            skLineSegment(sketch, "E2359", {"start": v(-10.77, 6.3) * mm, "end": v(-10.77, 6.3) * mm});
            skLineSegment(sketch, "E2360", {"start": v(-10.77, 6.3) * mm, "end": v(-10.77, 6.28) * mm});
            skLineSegment(sketch, "E2361", {"start": v(-10.77, 6.28) * mm, "end": v(-10.77, 6.27) * mm});
            skLineSegment(sketch, "E2362", {"start": v(-10.77, 6.27) * mm, "end": v(-10.86, 6.1) * mm});
            skLineSegment(sketch, "E2363", {"start": v(-10.86, 6.1) * mm, "end": v(-10.95, 5.91) * mm});
            skLineSegment(sketch, "E2364", {"start": v(-10.95, 5.91) * mm, "end": v(-11.04, 5.73) * mm});
            skLineSegment(sketch, "E2365", {"start": v(-11.04, 5.73) * mm, "end": v(-11.05, 5.73) * mm});
            skLineSegment(sketch, "E2366", {"start": v(-11.05, 5.73) * mm, "end": v(-11.06, 5.72) * mm});
            skLineSegment(sketch, "E2367", {"start": v(-11.06, 5.72) * mm, "end": v(-11.07, 5.71) * mm});
            skLineSegment(sketch, "E2368", {"start": v(-11.07, 5.71) * mm, "end": v(-11.1, 5.71) * mm});
            skLineSegment(sketch, "E2369", {"start": v(-11.1, 5.71) * mm, "end": v(-11.11, 5.7) * mm});
            skLineSegment(sketch, "E2370", {"start": v(-11.11, 5.7) * mm, "end": v(-11.13, 5.71) * mm});
            skLineSegment(sketch, "E2371", {"start": v(-11.13, 5.71) * mm, "end": v(-11.16, 5.71) * mm});
            skLineSegment(sketch, "E2372", {"start": v(-11.16, 5.71) * mm, "end": v(-11.19, 5.72) * mm});
            skLineSegment(sketch, "E2373", {"start": v(-11.19, 5.72) * mm, "end": v(-11.22, 5.73) * mm});
            skLineSegment(sketch, "E2374", {"start": v(-11.22, 5.73) * mm, "end": v(-11.24, 5.73) * mm});
            skLineSegment(sketch, "E2375", {"start": v(-11.24, 5.73) * mm, "end": v(-11.28, 5.74) * mm});
            skLineSegment(sketch, "E2376", {"start": v(-11.28, 5.74) * mm, "end": v(-11.32, 5.75) * mm});
            skLineSegment(sketch, "E2377", {"start": v(-11.32, 5.75) * mm, "end": v(-11.37, 5.76) * mm});
            skLineSegment(sketch, "E2378", {"start": v(-11.37, 5.76) * mm, "end": v(-11.41, 5.77) * mm});
            skLineSegment(sketch, "E2379", {"start": v(-11.41, 5.77) * mm, "end": v(-11.47, 5.78) * mm});
            skLineSegment(sketch, "E2380", {"start": v(-11.47, 5.78) * mm, "end": v(-11.52, 5.8) * mm});
            skLineSegment(sketch, "E2381", {"start": v(-11.52, 5.8) * mm, "end": v(-11.58, 5.8) * mm});
            skLineSegment(sketch, "E2382", {"start": v(-11.58, 5.8) * mm, "end": v(-11.64, 5.81) * mm});
            skLineSegment(sketch, "E2383", {"start": v(-11.64, 5.81) * mm, "end": v(-11.7, 5.82) * mm});
            skLineSegment(sketch, "E2384", {"start": v(-11.7, 5.82) * mm, "end": v(-11.78, 5.83) * mm});
            skLineSegment(sketch, "E2385", {"start": v(-11.78, 5.83) * mm, "end": v(-11.85, 5.83) * mm});
            skLineSegment(sketch, "E2386", {"start": v(-11.85, 5.83) * mm, "end": v(-11.93, 5.84) * mm});
            skLineSegment(sketch, "E2387", {"start": v(-11.93, 5.84) * mm, "end": v(-12, 5.84) * mm});
            skLineSegment(sketch, "E2388", {"start": v(-12, 5.84) * mm, "end": v(-12.09, 5.85) * mm});
            skLineSegment(sketch, "E2389", {"start": v(-12.09, 5.85) * mm, "end": v(-12.17, 5.85) * mm});
            skLineSegment(sketch, "E2390", {"start": v(-12.17, 5.85) * mm, "end": v(-12.26, 5.85) * mm});
            skLineSegment(sketch, "E2391", {"start": v(-12.26, 5.85) * mm, "end": v(-12.35, 5.85) * mm});
            skLineSegment(sketch, "E2392", {"start": v(-12.35, 5.85) * mm, "end": v(-12.45, 5.85) * mm});
            skLineSegment(sketch, "E2393", {"start": v(-12.45, 5.85) * mm, "end": v(-12.51, 5.85) * mm});
            skLineSegment(sketch, "E2394", {"start": v(-12.51, 5.85) * mm, "end": v(-12.64, 5.6) * mm});
            skLineSegment(sketch, "E2395", {"start": v(-12.64, 5.6) * mm, "end": v(-12.73, 5.33) * mm});
            skLineSegment(sketch, "E2396", {"start": v(-12.73, 5.33) * mm, "end": v(-12.69, 5.28) * mm});
            skLineSegment(sketch, "E2397", {"start": v(-12.69, 5.28) * mm, "end": v(-12.62, 5.2) * mm});
            skLineSegment(sketch, "E2398", {"start": v(-12.62, 5.2) * mm, "end": v(-12.55, 5.14) * mm});
            skLineSegment(sketch, "E2399", {"start": v(-12.55, 5.14) * mm, "end": v(-12.5, 5.08) * mm});
            skLineSegment(sketch, "E2400", {"start": v(-12.5, 5.08) * mm, "end": v(-12.43, 5.02) * mm});
            skLineSegment(sketch, "E2401", {"start": v(-12.43, 5.02) * mm, "end": v(-12.37, 4.97) * mm});
            skLineSegment(sketch, "E2402", {"start": v(-12.37, 4.97) * mm, "end": v(-12.3, 4.92) * mm});
            skLineSegment(sketch, "E2403", {"start": v(-12.3, 4.92) * mm, "end": v(-12.25, 4.87) * mm});
            skLineSegment(sketch, "E2404", {"start": v(-12.25, 4.87) * mm, "end": v(-12.2, 4.82) * mm});
            skLineSegment(sketch, "E2405", {"start": v(-12.2, 4.82) * mm, "end": v(-12.14, 4.78) * mm});
            skLineSegment(sketch, "E2406", {"start": v(-12.14, 4.78) * mm, "end": v(-12.09, 4.74) * mm});
            skLineSegment(sketch, "E2407", {"start": v(-12.09, 4.74) * mm, "end": v(-12.04, 4.7) * mm});
            skLineSegment(sketch, "E2408", {"start": v(-12.04, 4.7) * mm, "end": v(-11.99, 4.66) * mm});
            skLineSegment(sketch, "E2409", {"start": v(-11.99, 4.66) * mm, "end": v(-11.94, 4.63) * mm});
            skLineSegment(sketch, "E2410", {"start": v(-11.94, 4.63) * mm, "end": v(-11.9, 4.6) * mm});
            skLineSegment(sketch, "E2411", {"start": v(-11.9, 4.6) * mm, "end": v(-11.86, 4.57) * mm});
            skLineSegment(sketch, "E2412", {"start": v(-11.86, 4.57) * mm, "end": v(-11.82, 4.55) * mm});
            skLineSegment(sketch, "E2413", {"start": v(-11.82, 4.55) * mm, "end": v(-11.78, 4.53) * mm});
            skLineSegment(sketch, "E2414", {"start": v(-11.78, 4.53) * mm, "end": v(-11.75, 4.5) * mm});
            skLineSegment(sketch, "E2415", {"start": v(-11.75, 4.5) * mm, "end": v(-11.73, 4.5) * mm});
            skLineSegment(sketch, "E2416", {"start": v(-11.73, 4.5) * mm, "end": v(-11.7, 4.48) * mm});
            skLineSegment(sketch, "E2417", {"start": v(-11.7, 4.48) * mm, "end": v(-11.68, 4.46) * mm});
            skLineSegment(sketch, "E2418", {"start": v(-11.68, 4.46) * mm, "end": v(-11.66, 4.45) * mm});
            skLineSegment(sketch, "E2419", {"start": v(-11.66, 4.45) * mm, "end": v(-11.64, 4.43) * mm});
            skLineSegment(sketch, "E2420", {"start": v(-11.64, 4.43) * mm, "end": v(-11.63, 4.42) * mm});
            skLineSegment(sketch, "E2421", {"start": v(-11.63, 4.42) * mm, "end": v(-11.62, 4.4) * mm});
            skLineSegment(sketch, "E2422", {"start": v(-11.62, 4.4) * mm, "end": v(-11.61, 4.39) * mm});
            skLineSegment(sketch, "E2423", {"start": v(-11.61, 4.39) * mm, "end": v(-11.6, 4.38) * mm});
            skLineSegment(sketch, "E2424", {"start": v(-11.6, 4.38) * mm, "end": v(-11.6, 4.36) * mm});
            skLineSegment(sketch, "E2425", {"start": v(-11.6, 4.36) * mm, "end": v(-11.67, 4.18) * mm});
            skLineSegment(sketch, "E2426", {"start": v(-11.67, 4.18) * mm, "end": v(-11.74, 3.98) * mm});
            skLineSegment(sketch, "E2427", {"start": v(-11.74, 3.98) * mm, "end": v(-11.8, 3.8) * mm});
            skLineSegment(sketch, "E2428", {"start": v(-11.8, 3.8) * mm, "end": v(-11.8, 3.78) * mm});
            skLineSegment(sketch, "E2429", {"start": v(-11.8, 3.78) * mm, "end": v(-11.8, 3.78) * mm});
            skLineSegment(sketch, "E2430", {"start": v(-11.8, 3.78) * mm, "end": v(-11.82, 3.77) * mm});
            skLineSegment(sketch, "E2431", {"start": v(-11.82, 3.77) * mm, "end": v(-11.84, 3.76) * mm});
            skLineSegment(sketch, "E2432", {"start": v(-11.84, 3.76) * mm, "end": v(-11.86, 3.76) * mm});
            skLineSegment(sketch, "E2433", {"start": v(-11.86, 3.76) * mm, "end": v(-11.88, 3.76) * mm});
            skLineSegment(sketch, "E2434", {"start": v(-11.88, 3.76) * mm, "end": v(-11.9, 3.75) * mm});
            skLineSegment(sketch, "E2435", {"start": v(-11.9, 3.75) * mm, "end": v(-11.94, 3.76) * mm});
            skLineSegment(sketch, "E2436", {"start": v(-11.94, 3.76) * mm, "end": v(-11.97, 3.76) * mm});
            skLineSegment(sketch, "E2437", {"start": v(-11.97, 3.76) * mm, "end": v(-11.99, 3.76) * mm});
            skLineSegment(sketch, "E2438", {"start": v(-11.99, 3.76) * mm, "end": v(-12.03, 3.76) * mm});
            skLineSegment(sketch, "E2439", {"start": v(-12.03, 3.76) * mm, "end": v(-12.07, 3.77) * mm});
            skLineSegment(sketch, "E2440", {"start": v(-12.07, 3.77) * mm, "end": v(-12.12, 3.77) * mm});
            skLineSegment(sketch, "E2441", {"start": v(-12.12, 3.77) * mm, "end": v(-12.17, 3.77) * mm});
            skLineSegment(sketch, "E2442", {"start": v(-12.17, 3.77) * mm, "end": v(-12.22, 3.77) * mm});
            skLineSegment(sketch, "E2443", {"start": v(-12.22, 3.77) * mm, "end": v(-12.28, 3.78) * mm});
            skLineSegment(sketch, "E2444", {"start": v(-12.28, 3.78) * mm, "end": v(-12.34, 3.78) * mm});
            skLineSegment(sketch, "E2445", {"start": v(-12.34, 3.78) * mm, "end": v(-12.4, 3.77) * mm});
            skLineSegment(sketch, "E2446", {"start": v(-12.4, 3.77) * mm, "end": v(-12.47, 3.77) * mm});
            skLineSegment(sketch, "E2447", {"start": v(-12.47, 3.77) * mm, "end": v(-12.54, 3.77) * mm});
            skLineSegment(sketch, "E2448", {"start": v(-12.54, 3.77) * mm, "end": v(-12.6, 3.76) * mm});
            skLineSegment(sketch, "E2449", {"start": v(-12.6, 3.76) * mm, "end": v(-12.68, 3.76) * mm});
            skLineSegment(sketch, "E2450", {"start": v(-12.68, 3.76) * mm, "end": v(-12.76, 3.75) * mm});
            skLineSegment(sketch, "E2451", {"start": v(-12.76, 3.75) * mm, "end": v(-12.84, 3.74) * mm});
            skLineSegment(sketch, "E2452", {"start": v(-12.84, 3.74) * mm, "end": v(-12.93, 3.73) * mm});
            skLineSegment(sketch, "E2453", {"start": v(-12.93, 3.73) * mm, "end": v(-13.02, 3.72) * mm});
            skLineSegment(sketch, "E2454", {"start": v(-13.02, 3.72) * mm, "end": v(-13.1, 3.7) * mm});
            skLineSegment(sketch, "E2455", {"start": v(-13.1, 3.7) * mm, "end": v(-13.2, 3.69) * mm});
            skLineSegment(sketch, "E2456", {"start": v(-13.2, 3.69) * mm, "end": v(-13.27, 3.68) * mm});
            skLineSegment(sketch, "E2457", {"start": v(-13.27, 3.68) * mm, "end": v(-13.35, 3.4) * mm});
            skLineSegment(sketch, "E2458", {"start": v(-13.35, 3.4) * mm, "end": v(-13.4, 3.12) * mm});
            skLineSegment(sketch, "E2459", {"start": v(-13.4, 3.12) * mm, "end": v(-13.35, 3.09) * mm});
            skLineSegment(sketch, "E2460", {"start": v(-13.35, 3.09) * mm, "end": v(-13.27, 3.03) * mm});
            skLineSegment(sketch, "E2461", {"start": v(-13.27, 3.03) * mm, "end": v(-13.2, 2.97) * mm});
            skLineSegment(sketch, "E2462", {"start": v(-13.2, 2.97) * mm, "end": v(-13.12, 2.92) * mm});
            skLineSegment(sketch, "E2463", {"start": v(-13.12, 2.92) * mm, "end": v(-13.05, 2.87) * mm});
            skLineSegment(sketch, "E2464", {"start": v(-13.05, 2.87) * mm, "end": v(-12.98, 2.83) * mm});
            skLineSegment(sketch, "E2465", {"start": v(-12.98, 2.83) * mm, "end": v(-12.92, 2.79) * mm});
            skLineSegment(sketch, "E2466", {"start": v(-12.92, 2.79) * mm, "end": v(-12.85, 2.75) * mm});
            skLineSegment(sketch, "E2467", {"start": v(-12.85, 2.75) * mm, "end": v(-12.79, 2.71) * mm});
            skLineSegment(sketch, "E2468", {"start": v(-12.79, 2.71) * mm, "end": v(-12.73, 2.68) * mm});
            skLineSegment(sketch, "E2469", {"start": v(-12.73, 2.68) * mm, "end": v(-12.67, 2.64) * mm});
            skLineSegment(sketch, "E2470", {"start": v(-12.67, 2.64) * mm, "end": v(-12.62, 2.61) * mm});
            skLineSegment(sketch, "E2471", {"start": v(-12.62, 2.61) * mm, "end": v(-12.56, 2.59) * mm});
            skLineSegment(sketch, "E2472", {"start": v(-12.56, 2.59) * mm, "end": v(-12.51, 2.56) * mm});
            skLineSegment(sketch, "E2473", {"start": v(-12.51, 2.56) * mm, "end": v(-12.46, 2.54) * mm});
            skLineSegment(sketch, "E2474", {"start": v(-12.46, 2.54) * mm, "end": v(-12.42, 2.52) * mm});
            skLineSegment(sketch, "E2475", {"start": v(-12.42, 2.52) * mm, "end": v(-12.38, 2.5) * mm});
            skLineSegment(sketch, "E2476", {"start": v(-12.38, 2.5) * mm, "end": v(-12.34, 2.49) * mm});
            skLineSegment(sketch, "E2477", {"start": v(-12.34, 2.49) * mm, "end": v(-12.3, 2.47) * mm});
            skLineSegment(sketch, "E2478", {"start": v(-12.3, 2.47) * mm, "end": v(-12.28, 2.46) * mm});
            skLineSegment(sketch, "E2479", {"start": v(-12.28, 2.46) * mm, "end": v(-12.25, 2.45) * mm});
            skLineSegment(sketch, "E2480", {"start": v(-12.25, 2.45) * mm, "end": v(-12.22, 2.44) * mm});
            skLineSegment(sketch, "E2481", {"start": v(-12.22, 2.44) * mm, "end": v(-12.2, 2.43) * mm});
            skLineSegment(sketch, "E2482", {"start": v(-12.2, 2.43) * mm, "end": v(-12.18, 2.41) * mm});
            skLineSegment(sketch, "E2483", {"start": v(-12.18, 2.41) * mm, "end": v(-12.17, 2.4) * mm});
            skLineSegment(sketch, "E2484", {"start": v(-12.17, 2.4) * mm, "end": v(-12.15, 2.39) * mm});
            skLineSegment(sketch, "E2485", {"start": v(-12.15, 2.39) * mm, "end": v(-12.15, 2.38) * mm});
            skLineSegment(sketch, "E2486", {"start": v(-12.15, 2.38) * mm, "end": v(-12.14, 2.36) * mm});
            skLineSegment(sketch, "E2487", {"start": v(-12.14, 2.36) * mm, "end": v(-12.14, 2.35) * mm});
            skLineSegment(sketch, "E2488", {"start": v(-12.14, 2.35) * mm, "end": v(-12.17, 2.16) * mm});
            skLineSegment(sketch, "E2489", {"start": v(-12.17, 2.16) * mm, "end": v(-12.2, 1.95) * mm});
            skLineSegment(sketch, "E2490", {"start": v(-12.2, 1.95) * mm, "end": v(-12.23, 1.76) * mm});
            skLineSegment(sketch, "E2491", {"start": v(-12.23, 1.76) * mm, "end": v(-12.24, 1.75) * mm});
            skLineSegment(sketch, "E2492", {"start": v(-12.24, 1.75) * mm, "end": v(-12.25, 1.74) * mm});
            skLineSegment(sketch, "E2493", {"start": v(-12.25, 1.74) * mm, "end": v(-12.26, 1.73) * mm});
            skLineSegment(sketch, "E2494", {"start": v(-12.26, 1.73) * mm, "end": v(-12.27, 1.72) * mm});
            skLineSegment(sketch, "E2495", {"start": v(-12.27, 1.72) * mm, "end": v(-12.3, 1.71) * mm});
            skLineSegment(sketch, "E2496", {"start": v(-12.3, 1.71) * mm, "end": v(-12.32, 1.7) * mm});
            skLineSegment(sketch, "E2497", {"start": v(-12.32, 1.7) * mm, "end": v(-12.34, 1.7) * mm});
            skLineSegment(sketch, "E2498", {"start": v(-12.34, 1.7) * mm, "end": v(-12.37, 1.7) * mm});
            skLineSegment(sketch, "E2499", {"start": v(-12.37, 1.7) * mm, "end": v(-12.4, 1.7) * mm});
            skLineSegment(sketch, "E2500", {"start": v(-12.4, 1.7) * mm, "end": v(-12.42, 1.7) * mm});
            skLineSegment(sketch, "E2501", {"start": v(-12.42, 1.7) * mm, "end": v(-12.46, 1.7) * mm});
            skLineSegment(sketch, "E2502", {"start": v(-12.46, 1.7) * mm, "end": v(-12.5, 1.69) * mm});
            skLineSegment(sketch, "E2503", {"start": v(-12.5, 1.69) * mm, "end": v(-12.55, 1.68) * mm});
            skLineSegment(sketch, "E2504", {"start": v(-12.55, 1.68) * mm, "end": v(-12.6, 1.68) * mm});
            skLineSegment(sketch, "E2505", {"start": v(-12.6, 1.68) * mm, "end": v(-12.65, 1.67) * mm});
            skLineSegment(sketch, "E2506", {"start": v(-12.65, 1.67) * mm, "end": v(-12.7, 1.66) * mm});
            skLineSegment(sketch, "E2507", {"start": v(-12.7, 1.66) * mm, "end": v(-12.77, 1.66) * mm});
            skLineSegment(sketch, "E2508", {"start": v(-12.77, 1.66) * mm, "end": v(-12.83, 1.64) * mm});
            skLineSegment(sketch, "E2509", {"start": v(-12.83, 1.64) * mm, "end": v(-12.9, 1.63) * mm});
            skLineSegment(sketch, "E2510", {"start": v(-12.9, 1.63) * mm, "end": v(-12.96, 1.62) * mm});
            skLineSegment(sketch, "E2511", {"start": v(-12.96, 1.62) * mm, "end": v(-13.03, 1.6) * mm});
            skLineSegment(sketch, "E2512", {"start": v(-13.03, 1.6) * mm, "end": v(-13.1, 1.58) * mm});
            skLineSegment(sketch, "E2513", {"start": v(-13.1, 1.58) * mm, "end": v(-13.18, 1.57) * mm});
            skLineSegment(sketch, "E2514", {"start": v(-13.18, 1.57) * mm, "end": v(-13.26, 1.54) * mm});
            skLineSegment(sketch, "E2515", {"start": v(-13.26, 1.54) * mm, "end": v(-13.35, 1.52) * mm});
            skLineSegment(sketch, "E2516", {"start": v(-13.35, 1.52) * mm, "end": v(-13.43, 1.5) * mm});
            skLineSegment(sketch, "E2517", {"start": v(-13.43, 1.5) * mm, "end": v(-13.52, 1.47) * mm});
            skLineSegment(sketch, "E2518", {"start": v(-13.52, 1.47) * mm, "end": v(-13.6, 1.43) * mm});
            skLineSegment(sketch, "E2519", {"start": v(-13.6, 1.43) * mm, "end": v(-13.67, 1.41) * mm});
            skLineSegment(sketch, "E2520", {"start": v(-13.71, 1.13) * mm, "end": v(15.54, -1.17) * mm, "construction": true});
            skLineSegment(sketch, "E2521", {"start": v(-0.24, -14.65) * mm, "end": v(2.07, 14.6) * mm, "construction": true});
            skLineSegment(sketch, "E2522", {"start": v(10.44, -11.18) * mm, "end": v(-8.62, 11.14) * mm, "construction": true});
            skCircle(sketch, "E2523", {"center": v(0.91, -0.02) * mm, "radius": 2.67 * mm});
            skLineSegment(sketch, "E2524", {"start": v(-58.27, 57.68) * mm, "end": v(0, 57.68) * mm, "construction": true});
            skSolve(sketch);
        }
        {
            var Q0;
            Q0 = qSketchRegion(id + "F0", true);
            extrude(context, id + "F1", {"entities" : qUnion([Q0]), "endBound" : BoundingType.SYMMETRIC, "depth" : 35 * mm, "offsetDistance" : 25 * mm});
        }
        {
            var Q0;
            Q0=makeQuery(id+"F0.imprint","IMPRINT",FACE,{"disambiguationData":[TD([[makeQuery(id+"F0.imprint","IMPRINT",EDGE,{"derivedFrom":sQuery(id+"F0.wireOp",EDGE,"E2523")}),1.0]])]});
            extrude(context, id + "F2", {"entities" : qUnion([Q0]), "operationType" : NewBodyOperationType.ADD, "endBound" : BoundingType.SYMMETRIC, "depth" : 35 * mm, "offsetDistance" : 25 * mm});
        }
        {
            var Q0;
            Q0 = qSketchRegion(id + "F0", true);
            extrude(context, id + "F3", {"entities" : qUnion([Q0]), "operationType" : NewBodyOperationType.REMOVE, "endBound" : BoundingType.SYMMETRIC, "depth" : 25 * mm, "offsetDistance" : 25 * mm});
        }
    });
